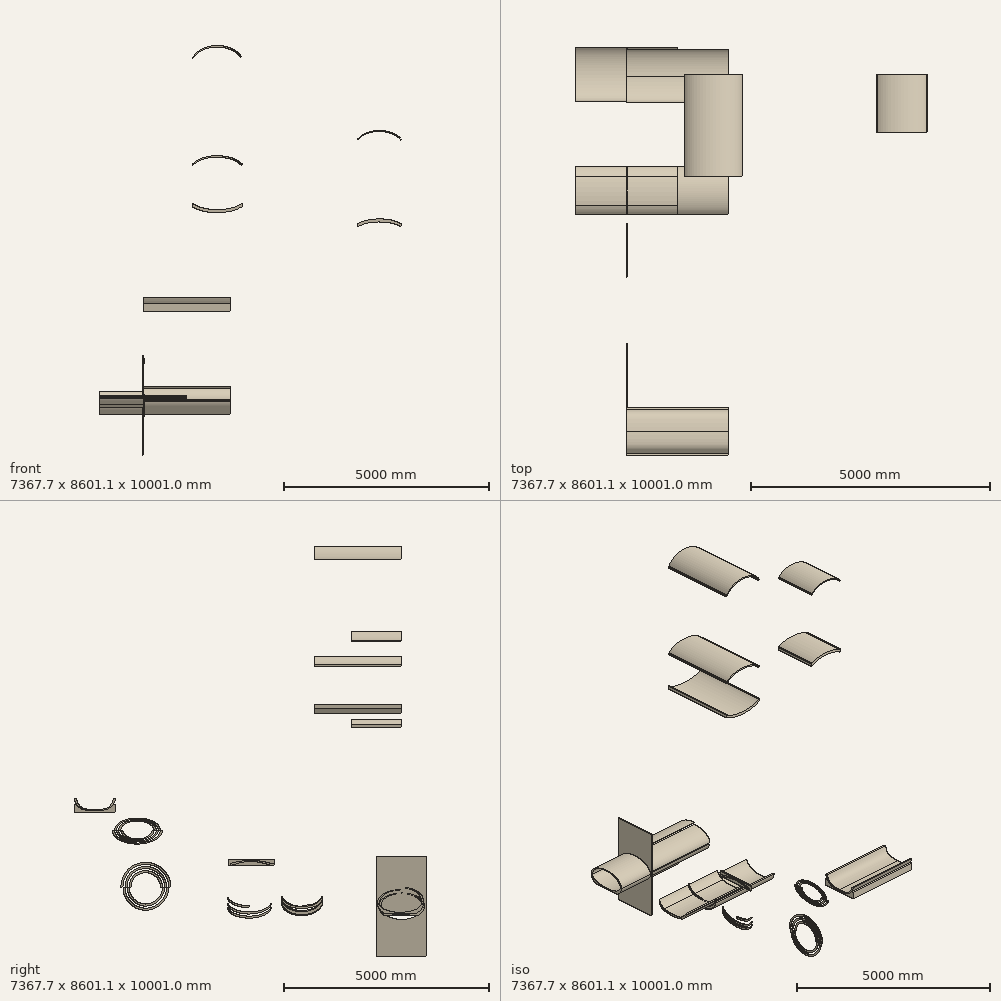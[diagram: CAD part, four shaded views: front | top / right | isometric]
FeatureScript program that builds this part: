
annotation { "Feature Type Name" : "Feature", "Feature Type Description" : "" }
export const myFeature = defineFeature(function(context is Context, id is Id, definition is map)
    precondition{}
    {
        {
            var Q0;
            Q0=qCreatedBy(makeId("Right.planeOp"),FACE);
            var sketch = newSketch(context, id + "F0", { "sketchPlane" : qUnion([Q0])});
            skLineSegment(sketch, "E0.bottom", {"start": v(-609.6, 1219.2) * mm, "end": v(609.6, 1219.2) * mm});
            skLineSegment(sketch, "E0.top", {"start": v(-609.6, -1219.2) * mm, "end": v(609.6, -1219.2) * mm});
            skLineSegment(sketch, "E0.left", {"start": v(-609.6, 1219.2) * mm, "end": v(-609.6, -1219.2) * mm});
            skLineSegment(sketch, "E0.right", {"start": v(609.6, 1219.2) * mm, "end": v(609.6, -1219.2) * mm});
            skPoint(sketch, "E0.middle", {"position": v(0, 0) * mm});
            skEllipse(sketch, "E1", {"center": v(0, 0) * mm, "majorRadius": 558.8 * mm, "minorRadius": 330.2 * mm, "majorAxis": v(1, 0)});
            skEllipse(sketch, "E2", {"center": v(0, 0) * mm, "majorRadius": 508 * mm, "minorRadius": 203.2 * mm, "majorAxis": v(1, 0)});
            skEllipse(sketch, "E3", {"center": v(0, 0) * mm, "majorRadius": 508 * mm, "minorRadius": 317.5 * mm, "majorAxis": v(1, 0)});
            skLineSegment(sketch, "E4", {"start": v(-558.8, 0) * mm, "end": v(558.8, 0) * mm, "construction": true});
            skLineSegment(sketch, "E5.bottom", {"start": v(571.5, -329.86) * mm, "end": v(-571.5, -329.86) * mm});
            skLineSegment(sketch, "E5.top", {"start": v(571.5, -228.26) * mm, "end": v(-571.5, -228.26) * mm});
            skLineSegment(sketch, "E5.left", {"start": v(571.5, -329.86) * mm, "end": v(571.5, -228.26) * mm});
            skLineSegment(sketch, "E5.right", {"start": v(-571.5, -329.86) * mm, "end": v(-571.5, -228.26) * mm});
            skPoint(sketch, "E5.middle", {"position": v(0, -279.06) * mm});
            skLineSegment(sketch, "E6", {"start": v(508, 0) * mm, "end": v(558.8, 0) * mm});
            skCircle(sketch, "E7", {"center": v(533.4, 0) * mm, "radius": 25.4 * mm});
            skLineSegment(sketch, "E8", {"start": v(-508, 0) * mm, "end": v(-558.8, 0) * mm});
            skSolve(sketch);
        }
        {
            var Q0;
            {var subQ0=sQuery(id+"F0.wireOp",EDGE,"E3");var subQ1=sQuery(id+"F0.wireOp",EDGE,"E2");var subQ2=makeQuery(id+"F0.imprint","INTERSECT",VERTEX,{"disambiguationData":[OD(0.0)],"derivedFrom":[subQ1,subQ0]});Q0=makeQuery(id+"F0.imprint","IMPRINT",FACE,{"disambiguationData":[TD([[makeQuery(id+"F0.imprint","IMPRINT",EDGE,{"disambiguationData":[TD([[subQ2,-1.0]])],"derivedFrom":subQ1}),-1.0]])]});}
            var Q1;
            {var subQ2=sQuery(id+"F0.wireOp",EDGE,"E1");var subQ4=sQuery(id+"F0.wireOp",EDGE,"E5.top");var subQ5=makeQuery(id+"F0.imprint","INTERSECT",VERTEX,{"disambiguationData":[OD(1.0)],"derivedFrom":[subQ2,subQ4]});Q1=makeQuery(id+"F0.imprint","IMPRINT",FACE,{"disambiguationData":[TD([[makeQuery(id+"F0.imprint","IMPRINT",EDGE,{"disambiguationData":[TD([[subQ5,-1.0]])],"derivedFrom":subQ4}),-1.0]])]});}
            var Q2;
            {var subQ0=sQuery(id+"F0.wireOp",EDGE,"E8");Q2=makeQuery(id+"F0.imprint","IMPRINT",FACE,{"disambiguationData":[TD([[makeQuery(id+"F0.imprint","IMPRINT",EDGE,{"derivedFrom":subQ0}),1.0]])]});}
            extrude(context, id + "F1", {"entities" : qUnion([Q0, Q1, Q2]), "endBound" : BoundingType.SYMMETRIC, "depth" : 2133.6 * mm});
        }
        {
            var Q0;
            {var subQ4=sQuery(id+"F0.wireOp",EDGE,"E8");Q0=makeQuery(id+"F0.imprint","IMPRINT",FACE,{"disambiguationData":[TD([[makeQuery(id+"F0.imprint","IMPRINT",EDGE,{"derivedFrom":subQ4}),-1.0]])]});}
            var Q1;
            {var subQ0=sQuery(id+"F0.wireOp",EDGE,"E6");Q1=makeQuery(id+"F0.imprint","IMPRINT",FACE,{"disambiguationData":[TD([[makeQuery(id+"F0.imprint","IMPRINT",EDGE,{"derivedFrom":subQ0}),1.0]])]});}
            var Q2;
            {var subQ0=sQuery(id+"F0.wireOp",EDGE,"E6");Q2=makeQuery(id+"F0.imprint","IMPRINT",FACE,{"disambiguationData":[TD([[makeQuery(id+"F0.imprint","IMPRINT",EDGE,{"derivedFrom":subQ0}),-1.0]])]});}
            extrude(context, id + "F2", {"entities" : qUnion([Q0, Q1, Q2]), "endBound" : BoundingType.SYMMETRIC, "depth" : 2133.6 * mm});
        }
        {
            var Q0;
            {var subQ5=sQuery(id+"F0.wireOp",EDGE,"E5.left");Q0=makeQuery(id+"F0.imprint","IMPRINT",FACE,{"disambiguationData":[TD([[makeQuery(id+"F0.imprint","IMPRINT",EDGE,{"derivedFrom":subQ5}),1.0]])]});}
            var Q1;
            {var subQ0=sQuery(id+"F0.wireOp",EDGE,"E3");var subQ1=sQuery(id+"F0.wireOp",EDGE,"E2");var subQ3=makeQuery(id+"F0.imprint","INTERSECT",VERTEX,{"derivedFrom":[subQ1,subQ0,sQuery(id+"F0.wireOp",EDGE,"E8")]});Q1=makeQuery(id+"F0.imprint","IMPRINT",FACE,{"disambiguationData":[TD([[makeQuery(id+"F0.imprint","IMPRINT",EDGE,{"disambiguationData":[TD([[subQ3,1.0]])],"derivedFrom":subQ1}),-1.0]])]});}
            var Q2;
            {var subQ0=sQuery(id+"F0.wireOp",EDGE,"E3");var subQ1=sQuery(id+"F0.wireOp",EDGE,"E2");var subQ3=makeQuery(id+"F0.imprint","INTERSECT",VERTEX,{"derivedFrom":[subQ1,subQ0,sQuery(id+"F0.wireOp",EDGE,"E8")]});Q2=makeQuery(id+"F0.imprint","IMPRINT",FACE,{"disambiguationData":[TD([[makeQuery(id+"F0.imprint","IMPRINT",EDGE,{"disambiguationData":[TD([[subQ3,1.0]])],"derivedFrom":subQ1}),1.0]])]});}
            var Q3;
            {var subQ0=sQuery(id+"F0.wireOp",EDGE,"E5.top");var subQ1=sQuery(id+"F0.wireOp",EDGE,"E3");var subQ2=makeQuery(id+"F0.imprint","INTERSECT",VERTEX,{"disambiguationData":[OD(0.0)],"derivedFrom":[subQ1,subQ0]});Q3=makeQuery(id+"F0.imprint","IMPRINT",FACE,{"disambiguationData":[TD([[makeQuery(id+"F0.imprint","IMPRINT",EDGE,{"disambiguationData":[TD([[subQ2,-1.0]])],"derivedFrom":subQ1}),1.0]])]});}
            var Q4;
            {var subQ5=sQuery(id+"F0.wireOp",EDGE,"E5.right");Q4=makeQuery(id+"F0.imprint","IMPRINT",FACE,{"disambiguationData":[TD([[makeQuery(id+"F0.imprint","IMPRINT",EDGE,{"derivedFrom":subQ5}),-1.0]])]});}
            var Q5;
            {var subQ1=sQuery(id+"F0.wireOp",EDGE,"E1");var subQ4=sQuery(id+"F0.wireOp",EDGE,"E5.top");var subQ5=makeQuery(id+"F0.imprint","INTERSECT",VERTEX,{"disambiguationData":[OD(0.0)],"derivedFrom":[subQ1,subQ4]});Q5=makeQuery(id+"F0.imprint","IMPRINT",FACE,{"disambiguationData":[TD([[makeQuery(id+"F0.imprint","IMPRINT",EDGE,{"disambiguationData":[TD([[subQ5,-1.0]])],"derivedFrom":subQ1}),1.0]])]});}
            var Q6;
            {var subQ4=sQuery(id+"F0.wireOp",EDGE,"E8");Q6=makeQuery(id+"F0.imprint","IMPRINT",FACE,{"disambiguationData":[TD([[makeQuery(id+"F0.imprint","IMPRINT",EDGE,{"derivedFrom":subQ4}),-1.0]])]});}
            var Q7;
            {var subQ0=sQuery(id+"F0.wireOp",EDGE,"E8");Q7=makeQuery(id+"F0.imprint","IMPRINT",FACE,{"disambiguationData":[TD([[makeQuery(id+"F0.imprint","IMPRINT",EDGE,{"derivedFrom":subQ0}),1.0]])]});}
            var Q8;
            {var subQ2=sQuery(id+"F0.wireOp",EDGE,"E1");var subQ4=sQuery(id+"F0.wireOp",EDGE,"E5.top");var subQ5=makeQuery(id+"F0.imprint","INTERSECT",VERTEX,{"disambiguationData":[OD(1.0)],"derivedFrom":[subQ2,subQ4]});Q8=makeQuery(id+"F0.imprint","IMPRINT",FACE,{"disambiguationData":[TD([[makeQuery(id+"F0.imprint","IMPRINT",EDGE,{"disambiguationData":[TD([[subQ5,-1.0]])],"derivedFrom":subQ4}),-1.0]])]});}
            var Q9;
            {var subQ0=sQuery(id+"F0.wireOp",EDGE,"E3");var subQ4=sQuery(id+"F0.wireOp",EDGE,"E5.top");var subQ5=makeQuery(id+"F0.imprint","INTERSECT",VERTEX,{"disambiguationData":[OD(0.0)],"derivedFrom":[subQ0,subQ4]});Q9=makeQuery(id+"F0.imprint","IMPRINT",FACE,{"disambiguationData":[TD([[makeQuery(id+"F0.imprint","IMPRINT",EDGE,{"disambiguationData":[TD([[subQ5,1.0]])],"derivedFrom":subQ4}),-1.0]])]});}
            var Q10;
            Q10=makeQuery(id+"F0.imprint","IMPRINT",FACE,{"disambiguationData":[TD([[makeQuery(id+"F0.imprint","IMPRINT",EDGE,{"derivedFrom":sQuery(id+"F0.wireOp",EDGE,"E0.bottom")}),-1.0]])]});
            var Q11;
            {var subQ0=sQuery(id+"F0.wireOp",EDGE,"E5.bottom");var subQ1=sQuery(id+"F0.wireOp",EDGE,"E1");var subQ2=makeQuery(id+"F0.imprint","INTERSECT",VERTEX,{"disambiguationData":[OD(0.0)],"derivedFrom":[subQ1,subQ0]});Q11=makeQuery(id+"F0.imprint","IMPRINT",FACE,{"disambiguationData":[TD([[makeQuery(id+"F0.imprint","IMPRINT",EDGE,{"disambiguationData":[TD([[subQ2,-1.0]])],"derivedFrom":subQ1}),1.0]])]});}
            var Q12;
            {var subQ0=sQuery(id+"F0.wireOp",EDGE,"E6");Q12=makeQuery(id+"F0.imprint","IMPRINT",FACE,{"disambiguationData":[TD([[makeQuery(id+"F0.imprint","IMPRINT",EDGE,{"derivedFrom":subQ0}),1.0]])]});}
            var Q13;
            {var subQ0=sQuery(id+"F0.wireOp",EDGE,"E6");Q13=makeQuery(id+"F0.imprint","IMPRINT",FACE,{"disambiguationData":[TD([[makeQuery(id+"F0.imprint","IMPRINT",EDGE,{"derivedFrom":subQ0}),-1.0]])]});}
            extrude(context, id + "F3", {"entities" : qUnion([Q0, Q1, Q2, Q3, Q4, Q5, Q6, Q7, Q8, Q9, Q10, Q11, Q12, Q13]), "oppositeDirection" : true, "depth" : 11.9 * mm});
        }
        {
            var Q0;
            {var subQ0=sQuery(id+"F0.wireOp",EDGE,"E8");Q0=makeQuery(id+"F0.imprint","IMPRINT",FACE,{"disambiguationData":[TD([[makeQuery(id+"F0.imprint","IMPRINT",EDGE,{"derivedFrom":subQ0}),1.0]])]});}
            var Q1;
            {var subQ0=sQuery(id+"F0.wireOp",EDGE,"E3");var subQ4=sQuery(id+"F0.wireOp",EDGE,"E5.top");var subQ5=makeQuery(id+"F0.imprint","INTERSECT",VERTEX,{"disambiguationData":[OD(0.0)],"derivedFrom":[subQ0,subQ4]});Q1=makeQuery(id+"F0.imprint","IMPRINT",FACE,{"disambiguationData":[TD([[makeQuery(id+"F0.imprint","IMPRINT",EDGE,{"disambiguationData":[TD([[subQ5,1.0]])],"derivedFrom":subQ4}),-1.0]])]});}
            var Q2;
            {var subQ2=sQuery(id+"F0.wireOp",EDGE,"E1");var subQ4=sQuery(id+"F0.wireOp",EDGE,"E5.top");var subQ5=makeQuery(id+"F0.imprint","INTERSECT",VERTEX,{"disambiguationData":[OD(1.0)],"derivedFrom":[subQ2,subQ4]});Q2=makeQuery(id+"F0.imprint","IMPRINT",FACE,{"disambiguationData":[TD([[makeQuery(id+"F0.imprint","IMPRINT",EDGE,{"disambiguationData":[TD([[subQ5,-1.0]])],"derivedFrom":subQ4}),-1.0]])]});}
            extrude(context, id + "F4", {"entities" : qUnion([Q0, Q1, Q2]), "depth" : 11.9 * mm});
        }
        {
            var Q0;
            {var subQ4=sQuery(id+"F0.wireOp",EDGE,"E8");Q0=makeQuery(id+"F0.imprint","IMPRINT",FACE,{"disambiguationData":[TD([[makeQuery(id+"F0.imprint","IMPRINT",EDGE,{"derivedFrom":subQ4}),-1.0]])]});}
            var Q1;
            {var subQ0=sQuery(id+"F0.wireOp",EDGE,"E6");Q1=makeQuery(id+"F0.imprint","IMPRINT",FACE,{"disambiguationData":[TD([[makeQuery(id+"F0.imprint","IMPRINT",EDGE,{"derivedFrom":subQ0}),1.0]])]});}
            var Q2;
            {var subQ0=sQuery(id+"F0.wireOp",EDGE,"E6");Q2=makeQuery(id+"F0.imprint","IMPRINT",FACE,{"disambiguationData":[TD([[makeQuery(id+"F0.imprint","IMPRINT",EDGE,{"derivedFrom":subQ0}),-1.0]])]});}
            extrude(context, id + "F5", {"entities" : qUnion([Q0, Q1, Q2]), "depth" : 11.9 * mm});
        }
        {
            var Q0;
            Q0=qCreatedBy(makeId("Right.planeOp"),FACE);
            var sketch = newSketch(context, id + "F6", { "sketchPlane" : qUnion([Q0])});
            skEllipse(sketch, "E9", {"center": v(-3717.75, -31.09) * mm, "majorRadius": 533.4 * mm, "minorRadius": 254 * mm, "majorAxis": v(1, 0)});
            skLineSegment(sketch, "E10", {"start": v(-3717.75, -31.09) * mm, "end": v(-3717.75, 922.12) * mm});
            skEllipse(sketch, "E11.0.1.0", {"center": v(-3717.75, 19.71) * mm, "majorRadius": 533.4 * mm, "minorRadius": 254 * mm, "majorAxis": v(1, 0)});
            skEllipse(sketch, "E11.0.2.0", {"center": v(-3717.75, 70.51) * mm, "majorRadius": 533.4 * mm, "minorRadius": 254 * mm, "majorAxis": v(1, 0)});
            skEllipse(sketch, "E11.0.3.0", {"center": v(-3717.75, 121.31) * mm, "majorRadius": 533.4 * mm, "minorRadius": 254 * mm, "majorAxis": v(1, 0)});
            skEllipse(sketch, "E11.0.4.0", {"center": v(-3717.75, 172.11) * mm, "majorRadius": 533.4 * mm, "minorRadius": 254 * mm, "majorAxis": v(1, 0)});
            skEllipse(sketch, "E11.0.5.0", {"center": v(-3717.75, 222.91) * mm, "majorRadius": 533.4 * mm, "minorRadius": 254 * mm, "majorAxis": v(1, 0)});
            skEllipse(sketch, "E11.0.6.0", {"center": v(-3717.75, 273.71) * mm, "majorRadius": 533.4 * mm, "minorRadius": 254 * mm, "majorAxis": v(1, 0)});
            skEllipse(sketch, "E11.0.7.0", {"center": v(-3717.75, 324.51) * mm, "majorRadius": 533.4 * mm, "minorRadius": 254 * mm, "majorAxis": v(1, 0)});
            skEllipse(sketch, "E11.0.8.0", {"center": v(-3717.75, 375.31) * mm, "majorRadius": 533.4 * mm, "minorRadius": 254 * mm, "majorAxis": v(1, 0)});
            skEllipse(sketch, "E11.0.9.0", {"center": v(-3717.75, 426.11) * mm, "majorRadius": 533.4 * mm, "minorRadius": 254 * mm, "majorAxis": v(1, 0)});
            skLineSegment(sketch, "E11.direction1", {"start": v(-3717.75, -31.09) * mm, "end": v(-3743.15, -31.09) * mm, "construction": true});
            skLineSegment(sketch, "E11.direction2", {"start": v(-3717.75, -31.09) * mm, "end": v(-3717.75, 19.71) * mm, "construction": true});
            skSolve(sketch);
        }
        {
            var Q0;
            {var subQ0=sQuery(id+"F6.wireOp",EDGE,"E11.0.1.0");var subQ1=sQuery(id+"F6.wireOp",EDGE,"E9");var subQ2=makeQuery(id+"F6.imprint","INTERSECT",VERTEX,{"disambiguationData":[OD(0.0)],"derivedFrom":[subQ1,subQ0]});Q0=makeQuery(id+"F6.imprint","IMPRINT",FACE,{"disambiguationData":[TD([[makeQuery(id+"F6.imprint","IMPRINT",EDGE,{"disambiguationData":[TD([[subQ2,1.0]])],"derivedFrom":subQ1}),1.0]])]});}
            extrude(context, id + "F7", {"entities" : qUnion([Q0]), "depth" : 25.4 * mm});
        }
        {
            var Q0;
            {var subQ0=sQuery(id+"F6.wireOp",EDGE,"E11.0.2.0");var subQ1=sQuery(id+"F6.wireOp",EDGE,"E9");var subQ2=makeQuery(id+"F6.imprint","INTERSECT",VERTEX,{"disambiguationData":[OD(0.0)],"derivedFrom":[subQ1,subQ0]});Q0=makeQuery(id+"F6.imprint","IMPRINT",FACE,{"disambiguationData":[TD([[makeQuery(id+"F6.imprint","IMPRINT",EDGE,{"disambiguationData":[TD([[subQ2,-1.0]])],"derivedFrom":subQ1}),1.0]])]});}
            var Q1;
            {var subQ0=sQuery(id+"F6.wireOp",EDGE,"E11.0.3.0");var subQ1=sQuery(id+"F6.wireOp",EDGE,"E9");var subQ2=makeQuery(id+"F6.imprint","INTERSECT",VERTEX,{"disambiguationData":[OD(1.0)],"derivedFrom":[subQ1,subQ0]});Q1=makeQuery(id+"F6.imprint","IMPRINT",FACE,{"disambiguationData":[TD([[makeQuery(id+"F6.imprint","IMPRINT",EDGE,{"disambiguationData":[TD([[subQ2,-1.0]])],"derivedFrom":subQ1}),-1.0]])]});}
            var Q2;
            {var subQ0=sQuery(id+"F6.wireOp",EDGE,"E11.0.2.0");var subQ1=sQuery(id+"F6.wireOp",EDGE,"E11.0.1.0");var subQ2=makeQuery(id+"F6.imprint","INTERSECT",VERTEX,{"disambiguationData":[OD(1.0)],"derivedFrom":[subQ1,subQ0]});Q2=makeQuery(id+"F6.imprint","IMPRINT",FACE,{"disambiguationData":[TD([[makeQuery(id+"F6.imprint","IMPRINT",EDGE,{"disambiguationData":[TD([[subQ2,1.0]])],"derivedFrom":subQ1}),-1.0]])]});}
            var Q3;
            {var subQ0=sQuery(id+"F6.wireOp",EDGE,"E11.0.2.0");var subQ1=sQuery(id+"F6.wireOp",EDGE,"E9");var subQ2=makeQuery(id+"F6.imprint","INTERSECT",VERTEX,{"disambiguationData":[OD(0.0)],"derivedFrom":[subQ1,subQ0]});Q3=makeQuery(id+"F6.imprint","IMPRINT",FACE,{"disambiguationData":[TD([[makeQuery(id+"F6.imprint","IMPRINT",EDGE,{"disambiguationData":[TD([[subQ2,-1.0]])],"derivedFrom":subQ1}),-1.0]])]});}
            var Q4;
            {var subQ0=sQuery(id+"F6.wireOp",EDGE,"E11.0.2.0");var subQ1=sQuery(id+"F6.wireOp",EDGE,"E11.0.1.0");var subQ2=makeQuery(id+"F6.imprint","INTERSECT",VERTEX,{"disambiguationData":[OD(0.0)],"derivedFrom":[subQ1,subQ0]});Q4=makeQuery(id+"F6.imprint","IMPRINT",FACE,{"disambiguationData":[TD([[makeQuery(id+"F6.imprint","IMPRINT",EDGE,{"disambiguationData":[TD([[subQ2,-1.0]])],"derivedFrom":subQ1}),-1.0]])]});}
            extrude(context, id + "F8", {"entities" : qUnion([Q0, Q1, Q2, Q3, Q4]), "depth" : 25.4 * mm});
        }
        {
            var Q0;
            Q0=qCreatedBy(makeId("Right.planeOp"),FACE);
            var sketch = newSketch(context, id + "F9", { "sketchPlane" : qUnion([Q0])});
            skLineSegment(sketch, "E12", {"start": v(-2434.14, 662.12) * mm, "end": v(-2434.14, -346.82) * mm, "construction": true});
            skEllipse(sketch, "E13", {"center": v(-2434.14, 104.15) * mm, "majorRadius": 508 * mm, "minorRadius": 203.2 * mm, "majorAxis": v(1, 0)});
            skEllipse(sketch, "E14.0.1.0", {"center": v(-2434.14, 129.55) * mm, "majorRadius": 508 * mm, "minorRadius": 203.2 * mm, "majorAxis": v(1, 0)});
            skEllipse(sketch, "E14.0.2.0", {"center": v(-2434.14, 154.95) * mm, "majorRadius": 508 * mm, "minorRadius": 203.2 * mm, "majorAxis": v(1, 0)});
            skEllipse(sketch, "E14.0.3.0", {"center": v(-2434.14, 180.35) * mm, "majorRadius": 508 * mm, "minorRadius": 203.2 * mm, "majorAxis": v(1, 0)});
            skLineSegment(sketch, "E14.direction1", {"start": v(-2434.14, 104.15) * mm, "end": v(-2434.14, 104.15) * mm});
            skLineSegment(sketch, "E14.direction2", {"start": v(-2434.14, 104.15) * mm, "end": v(-2434.14, 129.55) * mm, "construction": true});
            skEllipse(sketch, "E15", {"center": v(-2434.14, 104.15) * mm, "majorRadius": 508 * mm, "minorRadius": 330.2 * mm, "majorAxis": v(1, 0)});
            skEllipse(sketch, "E16.0.1.0", {"center": v(-2434.14, 129.55) * mm, "majorRadius": 508 * mm, "minorRadius": 330.2 * mm, "majorAxis": v(1, 0)});
            skEllipse(sketch, "E16.0.2.0", {"center": v(-2434.14, 154.95) * mm, "majorRadius": 508 * mm, "minorRadius": 330.2 * mm, "majorAxis": v(1, 0)});
            skEllipse(sketch, "E16.0.3.0", {"center": v(-2434.14, 180.35) * mm, "majorRadius": 508 * mm, "minorRadius": 330.2 * mm, "majorAxis": v(1, 0)});
            skEllipse(sketch, "E17.0.0.4", {"center": v(-2434.14, 205.75) * mm, "majorRadius": 508 * mm, "minorRadius": 330.2 * mm, "majorAxis": v(1, 0)});
            skEllipse(sketch, "E17.0.0.5", {"center": v(-2434.14, 231.15) * mm, "majorRadius": 508 * mm, "minorRadius": 330.2 * mm, "majorAxis": v(1, 0)});
            skEllipse(sketch, "E17.0.0.6", {"center": v(-2434.14, 256.55) * mm, "majorRadius": 508 * mm, "minorRadius": 330.2 * mm, "majorAxis": v(1, 0)});
            skEllipse(sketch, "E17.0.0.7", {"center": v(-2434.14, 281.95) * mm, "majorRadius": 508 * mm, "minorRadius": 330.2 * mm, "majorAxis": v(1, 0)});
            skEllipse(sketch, "E17.0.0.8", {"center": v(-2434.14, 307.35) * mm, "majorRadius": 508 * mm, "minorRadius": 330.2 * mm, "majorAxis": v(1, 0)});
            skEllipse(sketch, "E17.0.0.9", {"center": v(-2434.14, 332.75) * mm, "majorRadius": 508 * mm, "minorRadius": 330.2 * mm, "majorAxis": v(1, 0)});
            skEllipse(sketch, "E18.0.0.4", {"center": v(-2434.14, 205.75) * mm, "majorRadius": 508 * mm, "minorRadius": 203.2 * mm, "majorAxis": v(1, 0)});
            skEllipse(sketch, "E18.0.0.5", {"center": v(-2434.14, 231.15) * mm, "majorRadius": 508 * mm, "minorRadius": 203.2 * mm, "majorAxis": v(1, 0)});
            skEllipse(sketch, "E18.0.0.6", {"center": v(-2434.14, 256.55) * mm, "majorRadius": 508 * mm, "minorRadius": 203.2 * mm, "majorAxis": v(1, 0)});
            skEllipse(sketch, "E18.0.0.7", {"center": v(-2434.14, 281.95) * mm, "majorRadius": 508 * mm, "minorRadius": 203.2 * mm, "majorAxis": v(1, 0)});
            skEllipse(sketch, "E18.0.0.8", {"center": v(-2434.14, 307.35) * mm, "majorRadius": 508 * mm, "minorRadius": 203.2 * mm, "majorAxis": v(1, 0)});
            skEllipse(sketch, "E18.0.0.9", {"center": v(-2434.14, 332.75) * mm, "majorRadius": 508 * mm, "minorRadius": 203.2 * mm, "majorAxis": v(1, 0)});
            skLineSegment(sketch, "E19", {"start": v(-2434.14, 27.95) * mm, "end": v(-2434.14, 2.55) * mm});
            skSolve(sketch);
        }
        {
            var Q0;
            {var subQ0=sQuery(id+"F9.wireOp",EDGE,"E15");var subQ1=sQuery(id+"F9.wireOp",EDGE,"E13");var subQ2=makeQuery(id+"F9.imprint","INTERSECT",VERTEX,{"disambiguationData":[OD(1.0)],"derivedFrom":[subQ1,subQ0]});Q0=makeQuery(id+"F9.imprint","IMPRINT",FACE,{"disambiguationData":[TD([[makeQuery(id+"F9.imprint","IMPRINT",EDGE,{"disambiguationData":[TD([[subQ2,-1.0]])],"derivedFrom":subQ1}),-1.0]])]});}
            var Q1;
            {var subQ0=sQuery(id+"F9.wireOp",EDGE,"E13");var subQ1=makeQuery(id+"F9.imprint","INTERSECT",VERTEX,{"disambiguationData":[OD(0.0)],"derivedFrom":[subQ0,sQuery(id+"F9.wireOp",EDGE,"E15")]});Q1=makeQuery(id+"F9.imprint","IMPRINT",FACE,{"disambiguationData":[TD([[makeQuery(id+"F9.imprint","IMPRINT",EDGE,{"disambiguationData":[TD([[subQ1,-1.0]])],"derivedFrom":subQ0}),1.0]])]});}
            var Q2;
            {var subQ0=sQuery(id+"F9.wireOp",EDGE,"E13");var subQ1=makeQuery(id+"F9.imprint","INTERSECT",VERTEX,{"disambiguationData":[OD(1.0)],"derivedFrom":[subQ0,sQuery(id+"F9.wireOp",EDGE,"E15")]});Q2=makeQuery(id+"F9.imprint","IMPRINT",FACE,{"disambiguationData":[TD([[makeQuery(id+"F9.imprint","IMPRINT",EDGE,{"disambiguationData":[TD([[subQ1,1.0]])],"derivedFrom":subQ0}),1.0]])]});}
            extrude(context, id + "F10", {"entities" : qUnion([Q0, Q1, Q2]), "depth" : 2133.6 * mm});
        }
        {
            var Q0;
            {var subQ0=sQuery(id+"F9.wireOp",EDGE,"E16.0.1.0");var subQ1=sQuery(id+"F9.wireOp",EDGE,"E13");var subQ2=makeQuery(id+"F9.imprint","INTERSECT",VERTEX,{"disambiguationData":[OD(0.0)],"derivedFrom":[subQ1,subQ0]});Q0=makeQuery(id+"F9.imprint","IMPRINT",FACE,{"disambiguationData":[TD([[makeQuery(id+"F9.imprint","IMPRINT",EDGE,{"disambiguationData":[TD([[subQ2,-1.0]])],"derivedFrom":subQ1}),1.0]])]});}
            var Q1;
            {var subQ0=sQuery(id+"F9.wireOp",EDGE,"E16.0.3.0");var subQ1=sQuery(id+"F9.wireOp",EDGE,"E13");var subQ2=makeQuery(id+"F9.imprint","INTERSECT",VERTEX,{"disambiguationData":[OD(3.0)],"derivedFrom":[subQ1,subQ0]});Q1=makeQuery(id+"F9.imprint","IMPRINT",FACE,{"disambiguationData":[TD([[makeQuery(id+"F9.imprint","IMPRINT",EDGE,{"disambiguationData":[TD([[subQ2,-1.0]])],"derivedFrom":subQ1}),1.0]])]});}
            var Q2;
            {var subQ0=sQuery(id+"F9.wireOp",EDGE,"E16.0.1.0");var subQ1=sQuery(id+"F9.wireOp",EDGE,"E13");var subQ2=makeQuery(id+"F9.imprint","INTERSECT",VERTEX,{"disambiguationData":[OD(2.0)],"derivedFrom":[subQ1,subQ0]});Q2=makeQuery(id+"F9.imprint","IMPRINT",FACE,{"disambiguationData":[TD([[makeQuery(id+"F9.imprint","IMPRINT",EDGE,{"disambiguationData":[TD([[subQ2,-1.0]])],"derivedFrom":subQ1}),-1.0]])]});}
            var Q3;
            {var subQ0=sQuery(id+"F9.wireOp",EDGE,"E16.0.2.0");var subQ1=sQuery(id+"F9.wireOp",EDGE,"E13");var subQ2=makeQuery(id+"F9.imprint","INTERSECT",VERTEX,{"disambiguationData":[OD(2.0)],"derivedFrom":[subQ1,subQ0]});Q3=makeQuery(id+"F9.imprint","IMPRINT",FACE,{"disambiguationData":[TD([[makeQuery(id+"F9.imprint","IMPRINT",EDGE,{"disambiguationData":[TD([[subQ2,-1.0]])],"derivedFrom":subQ1}),-1.0]])]});}
            var Q4;
            {var subQ0=sQuery(id+"F9.wireOp",EDGE,"E16.0.2.0");var subQ1=sQuery(id+"F9.wireOp",EDGE,"E13");var subQ2=makeQuery(id+"F9.imprint","INTERSECT",VERTEX,{"disambiguationData":[OD(2.0)],"derivedFrom":[subQ1,subQ0]});Q4=makeQuery(id+"F9.imprint","IMPRINT",FACE,{"disambiguationData":[TD([[makeQuery(id+"F9.imprint","IMPRINT",EDGE,{"disambiguationData":[TD([[subQ2,-1.0]])],"derivedFrom":subQ1}),1.0]])]});}
            var Q5;
            {var subQ1=sQuery(id+"F9.wireOp",EDGE,"E13");var subQ6=sQuery(id+"F9.wireOp",EDGE,"E14.0.1.0");var subQ7=makeQuery(id+"F9.imprint","INTERSECT",VERTEX,{"disambiguationData":[OD(1.0)],"derivedFrom":[subQ1,subQ6]});Q5=makeQuery(id+"F9.imprint","IMPRINT",FACE,{"disambiguationData":[TD([[makeQuery(id+"F9.imprint","IMPRINT",EDGE,{"disambiguationData":[TD([[subQ7,-1.0]])],"derivedFrom":subQ1}),1.0]])]});}
            var Q6;
            {var subQ0=sQuery(id+"F9.wireOp",EDGE,"E16.0.2.0");var subQ1=sQuery(id+"F9.wireOp",EDGE,"E13");var subQ2=makeQuery(id+"F9.imprint","INTERSECT",VERTEX,{"disambiguationData":[OD(0.0)],"derivedFrom":[subQ1,subQ0]});Q6=makeQuery(id+"F9.imprint","IMPRINT",FACE,{"disambiguationData":[TD([[makeQuery(id+"F9.imprint","IMPRINT",EDGE,{"disambiguationData":[TD([[subQ2,-1.0]])],"derivedFrom":subQ1}),1.0]])]});}
            var Q7;
            {var subQ0=sQuery(id+"F9.wireOp",EDGE,"E14.0.1.0");var subQ1=sQuery(id+"F9.wireOp",EDGE,"E13");var subQ2=makeQuery(id+"F9.imprint","INTERSECT",VERTEX,{"disambiguationData":[OD(0.0)],"derivedFrom":[subQ1,subQ0]});Q7=makeQuery(id+"F9.imprint","IMPRINT",FACE,{"disambiguationData":[TD([[makeQuery(id+"F9.imprint","IMPRINT",EDGE,{"disambiguationData":[TD([[subQ2,-1.0]])],"derivedFrom":subQ1}),1.0]])]});}
            var Q8;
            {var subQ0=sQuery(id+"F9.wireOp",EDGE,"E14.0.2.0");var subQ1=sQuery(id+"F9.wireOp",EDGE,"E13");var subQ2=makeQuery(id+"F9.imprint","INTERSECT",VERTEX,{"disambiguationData":[OD(0.0)],"derivedFrom":[subQ1,subQ0]});Q8=makeQuery(id+"F9.imprint","IMPRINT",FACE,{"disambiguationData":[TD([[makeQuery(id+"F9.imprint","IMPRINT",EDGE,{"disambiguationData":[TD([[subQ2,-1.0]])],"derivedFrom":subQ1}),1.0]])]});}
            var Q9;
            {var subQ5=sQuery(id+"F9.wireOp",EDGE,"E13");var subQ7=sQuery(id+"F9.wireOp",EDGE,"E14.0.2.0");var subQ8=makeQuery(id+"F9.imprint","INTERSECT",VERTEX,{"disambiguationData":[OD(1.0)],"derivedFrom":[subQ5,subQ7]});Q9=makeQuery(id+"F9.imprint","IMPRINT",FACE,{"disambiguationData":[TD([[makeQuery(id+"F9.imprint","IMPRINT",EDGE,{"disambiguationData":[TD([[subQ8,-1.0]])],"derivedFrom":subQ5}),1.0]])]});}
            var Q10;
            {var subQ0=sQuery(id+"F9.wireOp",EDGE,"E16.0.2.0");var subQ1=sQuery(id+"F9.wireOp",EDGE,"E13");var subQ2=makeQuery(id+"F9.imprint","INTERSECT",VERTEX,{"disambiguationData":[OD(1.0)],"derivedFrom":[subQ1,subQ0]});Q10=makeQuery(id+"F9.imprint","IMPRINT",FACE,{"disambiguationData":[TD([[makeQuery(id+"F9.imprint","IMPRINT",EDGE,{"disambiguationData":[TD([[subQ2,-1.0]])],"derivedFrom":subQ1}),1.0]])]});}
            var Q11;
            {var subQ0=sQuery(id+"F9.wireOp",EDGE,"E16.0.3.0");var subQ1=sQuery(id+"F9.wireOp",EDGE,"E13");var subQ2=makeQuery(id+"F9.imprint","INTERSECT",VERTEX,{"disambiguationData":[OD(2.0)],"derivedFrom":[subQ1,subQ0]});Q11=makeQuery(id+"F9.imprint","IMPRINT",FACE,{"disambiguationData":[TD([[makeQuery(id+"F9.imprint","IMPRINT",EDGE,{"disambiguationData":[TD([[subQ2,-1.0]])],"derivedFrom":subQ1}),-1.0]])]});}
            var Q12;
            {var subQ0=sQuery(id+"F9.wireOp",EDGE,"E16.0.3.0");var subQ1=sQuery(id+"F9.wireOp",EDGE,"E13");var subQ2=makeQuery(id+"F9.imprint","INTERSECT",VERTEX,{"disambiguationData":[OD(2.0)],"derivedFrom":[subQ1,subQ0]});Q12=makeQuery(id+"F9.imprint","IMPRINT",FACE,{"disambiguationData":[TD([[makeQuery(id+"F9.imprint","IMPRINT",EDGE,{"disambiguationData":[TD([[subQ2,-1.0]])],"derivedFrom":subQ1}),1.0]])]});}
            var Q13;
            {var subQ0=sQuery(id+"F9.wireOp",EDGE,"E16.0.3.0");var subQ1=sQuery(id+"F9.wireOp",EDGE,"E14.0.1.0");var subQ2=makeQuery(id+"F9.imprint","INTERSECT",VERTEX,{"disambiguationData":[OD(2.0)],"derivedFrom":[subQ1,subQ0]});Q13=makeQuery(id+"F9.imprint","IMPRINT",FACE,{"disambiguationData":[TD([[makeQuery(id+"F9.imprint","IMPRINT",EDGE,{"disambiguationData":[TD([[subQ2,-1.0]])],"derivedFrom":subQ1}),1.0]])]});}
            var Q14;
            {var subQ1=sQuery(id+"F9.wireOp",EDGE,"E13");var subQ7=sQuery(id+"F9.wireOp",EDGE,"E14.0.3.0");var subQ8=makeQuery(id+"F9.imprint","INTERSECT",VERTEX,{"disambiguationData":[OD(1.0)],"derivedFrom":[subQ1,subQ7]});Q14=makeQuery(id+"F9.imprint","IMPRINT",FACE,{"disambiguationData":[TD([[makeQuery(id+"F9.imprint","IMPRINT",EDGE,{"disambiguationData":[TD([[subQ8,-1.0]])],"derivedFrom":subQ1}),1.0]])]});}
            var Q15;
            {var subQ0=sQuery(id+"F9.wireOp",EDGE,"E16.0.3.0");var subQ1=sQuery(id+"F9.wireOp",EDGE,"E13");var subQ2=makeQuery(id+"F9.imprint","INTERSECT",VERTEX,{"disambiguationData":[OD(1.0)],"derivedFrom":[subQ1,subQ0]});Q15=makeQuery(id+"F9.imprint","IMPRINT",FACE,{"disambiguationData":[TD([[makeQuery(id+"F9.imprint","IMPRINT",EDGE,{"disambiguationData":[TD([[subQ2,-1.0]])],"derivedFrom":subQ1}),1.0]])]});}
            var Q16;
            {var subQ0=sQuery(id+"F9.wireOp",EDGE,"E17.0.0.4");var subQ1=sQuery(id+"F9.wireOp",EDGE,"E13");var subQ2=makeQuery(id+"F9.imprint","INTERSECT",VERTEX,{"disambiguationData":[OD(3.0)],"derivedFrom":[subQ1,subQ0]});Q16=makeQuery(id+"F9.imprint","IMPRINT",FACE,{"disambiguationData":[TD([[makeQuery(id+"F9.imprint","IMPRINT",EDGE,{"disambiguationData":[TD([[subQ2,-1.0]])],"derivedFrom":subQ1}),1.0]])]});}
            var Q17;
            {var subQ0=sQuery(id+"F9.wireOp",EDGE,"E17.0.0.4");var subQ1=sQuery(id+"F9.wireOp",EDGE,"E14.0.1.0");var subQ2=makeQuery(id+"F9.imprint","INTERSECT",VERTEX,{"disambiguationData":[OD(3.0)],"derivedFrom":[subQ1,subQ0]});Q17=makeQuery(id+"F9.imprint","IMPRINT",FACE,{"disambiguationData":[TD([[makeQuery(id+"F9.imprint","IMPRINT",EDGE,{"disambiguationData":[TD([[subQ2,-1.0]])],"derivedFrom":subQ1}),1.0]])]});}
            var Q18;
            {var subQ0=sQuery(id+"F9.wireOp",EDGE,"E16.0.3.0");var subQ1=sQuery(id+"F9.wireOp",EDGE,"E13");var subQ2=makeQuery(id+"F9.imprint","INTERSECT",VERTEX,{"disambiguationData":[OD(0.0)],"derivedFrom":[subQ1,subQ0]});Q18=makeQuery(id+"F9.imprint","IMPRINT",FACE,{"disambiguationData":[TD([[makeQuery(id+"F9.imprint","IMPRINT",EDGE,{"disambiguationData":[TD([[subQ2,-1.0]])],"derivedFrom":subQ1}),1.0]])]});}
            extrude(context, id + "F11", {"entities" : qUnion([Q0, Q1, Q2, Q3, Q4, Q5, Q6, Q7, Q8, Q9, Q10, Q11, Q12, Q13, Q14, Q15, Q16, Q17, Q18]), "depth" : 2133.6 * mm});
        }
        {
            var Q0;
            {var subQ0=sQuery(id+"F9.wireOp",EDGE,"E17.0.0.4");var subQ1=sQuery(id+"F9.wireOp",EDGE,"E14.0.2.0");var subQ2=makeQuery(id+"F9.imprint","INTERSECT",VERTEX,{"disambiguationData":[OD(2.0)],"derivedFrom":[subQ1,subQ0]});Q0=makeQuery(id+"F9.imprint","IMPRINT",FACE,{"disambiguationData":[TD([[makeQuery(id+"F9.imprint","IMPRINT",EDGE,{"disambiguationData":[TD([[subQ2,-1.0]])],"derivedFrom":subQ1}),1.0]])]});}
            var Q1;
            {var subQ0=sQuery(id+"F9.wireOp",EDGE,"E17.0.0.5");var subQ1=sQuery(id+"F9.wireOp",EDGE,"E13");var subQ2=makeQuery(id+"F9.imprint","INTERSECT",VERTEX,{"disambiguationData":[OD(1.0)],"derivedFrom":[subQ1,subQ0]});Q1=makeQuery(id+"F9.imprint","IMPRINT",FACE,{"disambiguationData":[TD([[makeQuery(id+"F9.imprint","IMPRINT",EDGE,{"disambiguationData":[TD([[subQ2,-1.0]])],"derivedFrom":subQ1}),1.0]])]});}
            var Q2;
            {var subQ0=sQuery(id+"F9.wireOp",EDGE,"E18.0.0.4");var subQ1=sQuery(id+"F9.wireOp",EDGE,"E14.0.1.0");var subQ2=makeQuery(id+"F9.imprint","INTERSECT",VERTEX,{"disambiguationData":[OD(1.0)],"derivedFrom":[subQ1,subQ0]});Q2=makeQuery(id+"F9.imprint","IMPRINT",FACE,{"disambiguationData":[TD([[makeQuery(id+"F9.imprint","IMPRINT",EDGE,{"disambiguationData":[TD([[subQ2,-1.0]])],"derivedFrom":subQ1}),-1.0]])]});}
            var Q3;
            {var subQ0=sQuery(id+"F9.wireOp",EDGE,"E17.0.0.4");var subQ1=sQuery(id+"F9.wireOp",EDGE,"E14.0.1.0");var subQ2=makeQuery(id+"F9.imprint","INTERSECT",VERTEX,{"disambiguationData":[OD(2.0)],"derivedFrom":[subQ1,subQ0]});Q3=makeQuery(id+"F9.imprint","IMPRINT",FACE,{"disambiguationData":[TD([[makeQuery(id+"F9.imprint","IMPRINT",EDGE,{"disambiguationData":[TD([[subQ2,-1.0]])],"derivedFrom":subQ1}),1.0]])]});}
            var Q4;
            {var subQ0=sQuery(id+"F9.wireOp",EDGE,"E17.0.0.4");var subQ1=sQuery(id+"F9.wireOp",EDGE,"E13");var subQ2=makeQuery(id+"F9.imprint","INTERSECT",VERTEX,{"disambiguationData":[OD(2.0)],"derivedFrom":[subQ1,subQ0]});Q4=makeQuery(id+"F9.imprint","IMPRINT",FACE,{"disambiguationData":[TD([[makeQuery(id+"F9.imprint","IMPRINT",EDGE,{"disambiguationData":[TD([[subQ2,-1.0]])],"derivedFrom":subQ1}),1.0]])]});}
            var Q5;
            {var subQ0=sQuery(id+"F9.wireOp",EDGE,"E17.0.0.4");var subQ1=sQuery(id+"F9.wireOp",EDGE,"E13");var subQ2=makeQuery(id+"F9.imprint","INTERSECT",VERTEX,{"disambiguationData":[OD(2.0)],"derivedFrom":[subQ1,subQ0]});Q5=makeQuery(id+"F9.imprint","IMPRINT",FACE,{"disambiguationData":[TD([[makeQuery(id+"F9.imprint","IMPRINT",EDGE,{"disambiguationData":[TD([[subQ2,-1.0]])],"derivedFrom":subQ1}),-1.0]])]});}
            var Q6;
            {var subQ0=sQuery(id+"F9.wireOp",EDGE,"E17.0.0.5");var subQ1=sQuery(id+"F9.wireOp",EDGE,"E13");var subQ2=makeQuery(id+"F9.imprint","INTERSECT",VERTEX,{"disambiguationData":[OD(2.0)],"derivedFrom":[subQ1,subQ0]});Q6=makeQuery(id+"F9.imprint","IMPRINT",FACE,{"disambiguationData":[TD([[makeQuery(id+"F9.imprint","IMPRINT",EDGE,{"disambiguationData":[TD([[subQ2,-1.0]])],"derivedFrom":subQ1}),1.0]])]});}
            var Q7;
            {var subQ0=sQuery(id+"F9.wireOp",EDGE,"E17.0.0.5");var subQ1=sQuery(id+"F9.wireOp",EDGE,"E14.0.1.0");var subQ2=makeQuery(id+"F9.imprint","INTERSECT",VERTEX,{"disambiguationData":[OD(3.0)],"derivedFrom":[subQ1,subQ0]});Q7=makeQuery(id+"F9.imprint","IMPRINT",FACE,{"disambiguationData":[TD([[makeQuery(id+"F9.imprint","IMPRINT",EDGE,{"disambiguationData":[TD([[subQ2,-1.0]])],"derivedFrom":subQ1}),1.0]])]});}
            var Q8;
            {var subQ0=sQuery(id+"F9.wireOp",EDGE,"E17.0.0.5");var subQ1=sQuery(id+"F9.wireOp",EDGE,"E14.0.2.0");var subQ2=makeQuery(id+"F9.imprint","INTERSECT",VERTEX,{"disambiguationData":[OD(3.0)],"derivedFrom":[subQ1,subQ0]});Q8=makeQuery(id+"F9.imprint","IMPRINT",FACE,{"disambiguationData":[TD([[makeQuery(id+"F9.imprint","IMPRINT",EDGE,{"disambiguationData":[TD([[subQ2,-1.0]])],"derivedFrom":subQ1}),1.0]])]});}
            var Q9;
            {var subQ0=sQuery(id+"F9.wireOp",EDGE,"E17.0.0.4");var subQ1=sQuery(id+"F9.wireOp",EDGE,"E13");var subQ2=makeQuery(id+"F9.imprint","INTERSECT",VERTEX,{"disambiguationData":[OD(0.0)],"derivedFrom":[subQ1,subQ0]});Q9=makeQuery(id+"F9.imprint","IMPRINT",FACE,{"disambiguationData":[TD([[makeQuery(id+"F9.imprint","IMPRINT",EDGE,{"disambiguationData":[TD([[subQ2,-1.0]])],"derivedFrom":subQ1}),1.0]])]});}
            var Q10;
            {var subQ1=sQuery(id+"F9.wireOp",EDGE,"E13");var subQ5=sQuery(id+"F9.wireOp",EDGE,"E17.0.0.4");var subQ6=makeQuery(id+"F9.imprint","INTERSECT",VERTEX,{"disambiguationData":[OD(0.0)],"derivedFrom":[subQ1,subQ5]});Q10=makeQuery(id+"F9.imprint","IMPRINT",FACE,{"disambiguationData":[TD([[makeQuery(id+"F9.imprint","IMPRINT",EDGE,{"disambiguationData":[TD([[subQ6,-1.0]])],"derivedFrom":subQ1}),-1.0]])]});}
            var Q11;
            {var subQ0=sQuery(id+"F9.wireOp",EDGE,"E17.0.0.5");var subQ1=sQuery(id+"F9.wireOp",EDGE,"E13");var subQ2=makeQuery(id+"F9.imprint","INTERSECT",VERTEX,{"disambiguationData":[OD(1.0)],"derivedFrom":[subQ1,subQ0]});Q11=makeQuery(id+"F9.imprint","IMPRINT",FACE,{"disambiguationData":[TD([[makeQuery(id+"F9.imprint","IMPRINT",EDGE,{"disambiguationData":[TD([[subQ2,-1.0]])],"derivedFrom":subQ1}),-1.0]])]});}
            var Q12;
            {var subQ0=sQuery(id+"F9.wireOp",EDGE,"E18.0.0.4");var subQ1=sQuery(id+"F9.wireOp",EDGE,"E14.0.1.0");var subQ2=makeQuery(id+"F9.imprint","INTERSECT",VERTEX,{"disambiguationData":[OD(1.0)],"derivedFrom":[subQ1,subQ0]});Q12=makeQuery(id+"F9.imprint","IMPRINT",FACE,{"disambiguationData":[TD([[makeQuery(id+"F9.imprint","IMPRINT",EDGE,{"disambiguationData":[TD([[subQ2,-1.0]])],"derivedFrom":subQ1}),1.0]])]});}
            var Q13;
            {var subQ0=sQuery(id+"F9.wireOp",EDGE,"E18.0.0.4");var subQ1=sQuery(id+"F9.wireOp",EDGE,"E14.0.2.0");var subQ2=makeQuery(id+"F9.imprint","INTERSECT",VERTEX,{"disambiguationData":[OD(1.0)],"derivedFrom":[subQ1,subQ0]});Q13=makeQuery(id+"F9.imprint","IMPRINT",FACE,{"disambiguationData":[TD([[makeQuery(id+"F9.imprint","IMPRINT",EDGE,{"disambiguationData":[TD([[subQ2,-1.0]])],"derivedFrom":subQ1}),1.0]])]});}
            var Q14;
            {var subQ0=sQuery(id+"F9.wireOp",EDGE,"E17.0.0.4");var subQ1=sQuery(id+"F9.wireOp",EDGE,"E14.0.1.0");var subQ2=makeQuery(id+"F9.imprint","INTERSECT",VERTEX,{"disambiguationData":[OD(0.0)],"derivedFrom":[subQ1,subQ0]});Q14=makeQuery(id+"F9.imprint","IMPRINT",FACE,{"disambiguationData":[TD([[makeQuery(id+"F9.imprint","IMPRINT",EDGE,{"disambiguationData":[TD([[subQ2,-1.0]])],"derivedFrom":subQ1}),-1.0]])]});}
            var Q15;
            {var subQ0=sQuery(id+"F9.wireOp",EDGE,"E17.0.0.4");var subQ1=sQuery(id+"F9.wireOp",EDGE,"E14.0.1.0");var subQ2=makeQuery(id+"F9.imprint","INTERSECT",VERTEX,{"disambiguationData":[OD(0.0)],"derivedFrom":[subQ1,subQ0]});Q15=makeQuery(id+"F9.imprint","IMPRINT",FACE,{"disambiguationData":[TD([[makeQuery(id+"F9.imprint","IMPRINT",EDGE,{"disambiguationData":[TD([[subQ2,-1.0]])],"derivedFrom":subQ1}),1.0]])]});}
            var Q16;
            {var subQ0=sQuery(id+"F9.wireOp",EDGE,"E17.0.0.4");var subQ1=sQuery(id+"F9.wireOp",EDGE,"E14.0.2.0");var subQ2=makeQuery(id+"F9.imprint","INTERSECT",VERTEX,{"disambiguationData":[OD(0.0)],"derivedFrom":[subQ1,subQ0]});Q16=makeQuery(id+"F9.imprint","IMPRINT",FACE,{"disambiguationData":[TD([[makeQuery(id+"F9.imprint","IMPRINT",EDGE,{"disambiguationData":[TD([[subQ2,-1.0]])],"derivedFrom":subQ1}),1.0]])]});}
            var Q17;
            {var subQ0=sQuery(id+"F9.wireOp",EDGE,"E18.0.0.4");var subQ1=sQuery(id+"F9.wireOp",EDGE,"E14.0.1.0");var subQ2=makeQuery(id+"F9.imprint","INTERSECT",VERTEX,{"disambiguationData":[OD(0.0)],"derivedFrom":[subQ1,subQ0]});Q17=makeQuery(id+"F9.imprint","IMPRINT",FACE,{"disambiguationData":[TD([[makeQuery(id+"F9.imprint","IMPRINT",EDGE,{"disambiguationData":[TD([[subQ2,-1.0]])],"derivedFrom":subQ1}),-1.0]])]});}
            var Q18;
            {var subQ0=sQuery(id+"F9.wireOp",EDGE,"E18.0.0.4");var subQ1=sQuery(id+"F9.wireOp",EDGE,"E14.0.1.0");var subQ2=makeQuery(id+"F9.imprint","INTERSECT",VERTEX,{"disambiguationData":[OD(0.0)],"derivedFrom":[subQ1,subQ0]});Q18=makeQuery(id+"F9.imprint","IMPRINT",FACE,{"disambiguationData":[TD([[makeQuery(id+"F9.imprint","IMPRINT",EDGE,{"disambiguationData":[TD([[subQ2,-1.0]])],"derivedFrom":subQ1}),1.0]])]});}
            var Q19;
            {var subQ0=sQuery(id+"F9.wireOp",EDGE,"E18.0.0.4");var subQ1=sQuery(id+"F9.wireOp",EDGE,"E15");var subQ2=makeQuery(id+"F9.imprint","INTERSECT",VERTEX,{"disambiguationData":[OD(0.0)],"derivedFrom":[subQ1,subQ0]});Q19=makeQuery(id+"F9.imprint","IMPRINT",FACE,{"disambiguationData":[TD([[makeQuery(id+"F9.imprint","IMPRINT",EDGE,{"disambiguationData":[TD([[subQ2,-1.0]])],"derivedFrom":subQ1}),1.0]])]});}
            var Q20;
            {var subQ0=sQuery(id+"F9.wireOp",EDGE,"E18.0.0.4");var subQ1=sQuery(id+"F9.wireOp",EDGE,"E14.0.2.0");var subQ2=makeQuery(id+"F9.imprint","INTERSECT",VERTEX,{"disambiguationData":[OD(0.0)],"derivedFrom":[subQ1,subQ0]});Q20=makeQuery(id+"F9.imprint","IMPRINT",FACE,{"disambiguationData":[TD([[makeQuery(id+"F9.imprint","IMPRINT",EDGE,{"disambiguationData":[TD([[subQ2,-1.0]])],"derivedFrom":subQ1}),1.0]])]});}
            var Q21;
            {var subQ0=sQuery(id+"F9.wireOp",EDGE,"E17.0.0.4");var subQ1=sQuery(id+"F9.wireOp",EDGE,"E14.0.2.0");var subQ2=makeQuery(id+"F9.imprint","INTERSECT",VERTEX,{"disambiguationData":[OD(0.0)],"derivedFrom":[subQ1,subQ0]});Q21=makeQuery(id+"F9.imprint","IMPRINT",FACE,{"disambiguationData":[TD([[makeQuery(id+"F9.imprint","IMPRINT",EDGE,{"disambiguationData":[TD([[subQ2,-1.0]])],"derivedFrom":subQ1}),-1.0]])]});}
            var Q22;
            {var subQ0=sQuery(id+"F9.wireOp",EDGE,"E18.0.0.4");var subQ1=sQuery(id+"F9.wireOp",EDGE,"E14.0.2.0");var subQ2=makeQuery(id+"F9.imprint","INTERSECT",VERTEX,{"disambiguationData":[OD(0.0)],"derivedFrom":[subQ1,subQ0]});Q22=makeQuery(id+"F9.imprint","IMPRINT",FACE,{"disambiguationData":[TD([[makeQuery(id+"F9.imprint","IMPRINT",EDGE,{"disambiguationData":[TD([[subQ2,-1.0]])],"derivedFrom":subQ1}),-1.0]])]});}
            var Q23;
            {var subQ0=sQuery(id+"F9.wireOp",EDGE,"E17.0.0.4");var subQ1=sQuery(id+"F9.wireOp",EDGE,"E14.0.3.0");var subQ2=makeQuery(id+"F9.imprint","INTERSECT",VERTEX,{"disambiguationData":[OD(0.0)],"derivedFrom":[subQ1,subQ0]});Q23=makeQuery(id+"F9.imprint","IMPRINT",FACE,{"disambiguationData":[TD([[makeQuery(id+"F9.imprint","IMPRINT",EDGE,{"disambiguationData":[TD([[subQ2,-1.0]])],"derivedFrom":subQ1}),1.0]])]});}
            var Q24;
            {var subQ0=sQuery(id+"F9.wireOp",EDGE,"E18.0.0.4");var subQ1=sQuery(id+"F9.wireOp",EDGE,"E14.0.3.0");var subQ2=makeQuery(id+"F9.imprint","INTERSECT",VERTEX,{"disambiguationData":[OD(0.0)],"derivedFrom":[subQ1,subQ0]});Q24=makeQuery(id+"F9.imprint","IMPRINT",FACE,{"disambiguationData":[TD([[makeQuery(id+"F9.imprint","IMPRINT",EDGE,{"disambiguationData":[TD([[subQ2,-1.0]])],"derivedFrom":subQ1}),1.0]])]});}
            var Q25;
            {var subQ0=sQuery(id+"F9.wireOp",EDGE,"E17.0.0.5");var subQ1=sQuery(id+"F9.wireOp",EDGE,"E14.0.2.0");var subQ2=makeQuery(id+"F9.imprint","INTERSECT",VERTEX,{"disambiguationData":[OD(1.0)],"derivedFrom":[subQ1,subQ0]});Q25=makeQuery(id+"F9.imprint","IMPRINT",FACE,{"disambiguationData":[TD([[makeQuery(id+"F9.imprint","IMPRINT",EDGE,{"disambiguationData":[TD([[subQ2,-1.0]])],"derivedFrom":subQ1}),1.0]])]});}
            var Q26;
            {var subQ0=sQuery(id+"F9.wireOp",EDGE,"E17.0.0.5");var subQ1=sQuery(id+"F9.wireOp",EDGE,"E14.0.1.0");var subQ2=makeQuery(id+"F9.imprint","INTERSECT",VERTEX,{"disambiguationData":[OD(1.0)],"derivedFrom":[subQ1,subQ0]});Q26=makeQuery(id+"F9.imprint","IMPRINT",FACE,{"disambiguationData":[TD([[makeQuery(id+"F9.imprint","IMPRINT",EDGE,{"disambiguationData":[TD([[subQ2,-1.0]])],"derivedFrom":subQ1}),-1.0]])]});}
            var Q27;
            {var subQ0=sQuery(id+"F9.wireOp",EDGE,"E17.0.0.5");var subQ1=sQuery(id+"F9.wireOp",EDGE,"E14.0.1.0");var subQ2=makeQuery(id+"F9.imprint","INTERSECT",VERTEX,{"disambiguationData":[OD(1.0)],"derivedFrom":[subQ1,subQ0]});Q27=makeQuery(id+"F9.imprint","IMPRINT",FACE,{"disambiguationData":[TD([[makeQuery(id+"F9.imprint","IMPRINT",EDGE,{"disambiguationData":[TD([[subQ2,-1.0]])],"derivedFrom":subQ1}),1.0]])]});}
            var Q28;
            {var subQ0=sQuery(id+"F9.wireOp",EDGE,"E17.0.0.5");var subQ1=sQuery(id+"F9.wireOp",EDGE,"E15");var subQ2=makeQuery(id+"F9.imprint","INTERSECT",VERTEX,{"disambiguationData":[OD(1.0)],"derivedFrom":[subQ1,subQ0]});Q28=makeQuery(id+"F9.imprint","IMPRINT",FACE,{"disambiguationData":[TD([[makeQuery(id+"F9.imprint","IMPRINT",EDGE,{"disambiguationData":[TD([[subQ2,-1.0]])],"derivedFrom":subQ1}),1.0]])]});}
            var Q29;
            {var subQ0=sQuery(id+"F9.wireOp",EDGE,"E18.0.0.4");var subQ1=sQuery(id+"F9.wireOp",EDGE,"E14.0.2.0");var subQ2=makeQuery(id+"F9.imprint","INTERSECT",VERTEX,{"disambiguationData":[OD(1.0)],"derivedFrom":[subQ1,subQ0]});Q29=makeQuery(id+"F9.imprint","IMPRINT",FACE,{"disambiguationData":[TD([[makeQuery(id+"F9.imprint","IMPRINT",EDGE,{"disambiguationData":[TD([[subQ2,-1.0]])],"derivedFrom":subQ1}),-1.0]])]});}
            var Q30;
            {var subQ0=sQuery(id+"F9.wireOp",EDGE,"E17.0.0.5");var subQ1=sQuery(id+"F9.wireOp",EDGE,"E14.0.2.0");var subQ2=makeQuery(id+"F9.imprint","INTERSECT",VERTEX,{"disambiguationData":[OD(1.0)],"derivedFrom":[subQ1,subQ0]});Q30=makeQuery(id+"F9.imprint","IMPRINT",FACE,{"disambiguationData":[TD([[makeQuery(id+"F9.imprint","IMPRINT",EDGE,{"disambiguationData":[TD([[subQ2,-1.0]])],"derivedFrom":subQ1}),-1.0]])]});}
            var Q31;
            {var subQ0=sQuery(id+"F9.wireOp",EDGE,"E17.0.0.5");var subQ1=sQuery(id+"F9.wireOp",EDGE,"E14.0.3.0");var subQ2=makeQuery(id+"F9.imprint","INTERSECT",VERTEX,{"disambiguationData":[OD(1.0)],"derivedFrom":[subQ1,subQ0]});Q31=makeQuery(id+"F9.imprint","IMPRINT",FACE,{"disambiguationData":[TD([[makeQuery(id+"F9.imprint","IMPRINT",EDGE,{"disambiguationData":[TD([[subQ2,-1.0]])],"derivedFrom":subQ1}),1.0]])]});}
            var Q32;
            {var subQ0=sQuery(id+"F9.wireOp",EDGE,"E18.0.0.4");var subQ1=sQuery(id+"F9.wireOp",EDGE,"E14.0.3.0");var subQ2=makeQuery(id+"F9.imprint","INTERSECT",VERTEX,{"disambiguationData":[OD(1.0)],"derivedFrom":[subQ1,subQ0]});Q32=makeQuery(id+"F9.imprint","IMPRINT",FACE,{"disambiguationData":[TD([[makeQuery(id+"F9.imprint","IMPRINT",EDGE,{"disambiguationData":[TD([[subQ2,-1.0]])],"derivedFrom":subQ1}),1.0]])]});}
            extrude(context, id + "F12", {"entities" : qUnion([Q0, Q1, Q2, Q3, Q4, Q5, Q6, Q7, Q8, Q9, Q10, Q11, Q12, Q13, Q14, Q15, Q16, Q17, Q18, Q19, Q20, Q21, Q22, Q23, Q24, Q25, Q26, Q27, Q28, Q29, Q30, Q31, Q32]), "depth" : 25.4 * mm});
        }
        {
            var Q0;
            {var subQ0=sQuery(id+"F9.wireOp",EDGE,"E17.0.0.7");var subQ1=sQuery(id+"F9.wireOp",EDGE,"E14.0.3.0");var subQ2=makeQuery(id+"F9.imprint","INTERSECT",VERTEX,{"disambiguationData":[OD(2.0)],"derivedFrom":[subQ1,subQ0]});Q0=makeQuery(id+"F9.imprint","IMPRINT",FACE,{"disambiguationData":[TD([[makeQuery(id+"F9.imprint","IMPRINT",EDGE,{"disambiguationData":[TD([[subQ2,-1.0]])],"derivedFrom":subQ1}),-1.0]])]});}
            var Q1;
            {var subQ0=sQuery(id+"F9.wireOp",EDGE,"E17.0.0.7");var subQ1=sQuery(id+"F9.wireOp",EDGE,"E14.0.2.0");var subQ2=makeQuery(id+"F9.imprint","INTERSECT",VERTEX,{"disambiguationData":[OD(2.0)],"derivedFrom":[subQ1,subQ0]});Q1=makeQuery(id+"F9.imprint","IMPRINT",FACE,{"disambiguationData":[TD([[makeQuery(id+"F9.imprint","IMPRINT",EDGE,{"disambiguationData":[TD([[subQ2,-1.0]])],"derivedFrom":subQ1}),1.0]])]});}
            var Q2;
            {var subQ0=sQuery(id+"F9.wireOp",EDGE,"E17.0.0.8");var subQ1=sQuery(id+"F9.wireOp",EDGE,"E14.0.3.0");var subQ2=makeQuery(id+"F9.imprint","INTERSECT",VERTEX,{"disambiguationData":[OD(2.0)],"derivedFrom":[subQ1,subQ0]});Q2=makeQuery(id+"F9.imprint","IMPRINT",FACE,{"disambiguationData":[TD([[makeQuery(id+"F9.imprint","IMPRINT",EDGE,{"disambiguationData":[TD([[subQ2,-1.0]])],"derivedFrom":subQ1}),1.0]])]});}
            var Q3;
            {var subQ0=sQuery(id+"F9.wireOp",EDGE,"E17.0.0.7");var subQ1=sQuery(id+"F9.wireOp",EDGE,"E14.0.3.0");var subQ2=makeQuery(id+"F9.imprint","INTERSECT",VERTEX,{"disambiguationData":[OD(3.0)],"derivedFrom":[subQ1,subQ0]});Q3=makeQuery(id+"F9.imprint","IMPRINT",FACE,{"disambiguationData":[TD([[makeQuery(id+"F9.imprint","IMPRINT",EDGE,{"disambiguationData":[TD([[subQ2,-1.0]])],"derivedFrom":subQ1}),1.0]])]});}
            var Q4;
            {var subQ3=sQuery(id+"F9.wireOp",EDGE,"E17.0.0.5");var subQ7=sQuery(id+"F9.wireOp",EDGE,"E13");var subQ8=makeQuery(id+"F9.imprint","INTERSECT",VERTEX,{"disambiguationData":[OD(0.0)],"derivedFrom":[subQ7,subQ3]});Q4=makeQuery(id+"F9.imprint","IMPRINT",FACE,{"disambiguationData":[TD([[makeQuery(id+"F9.imprint","IMPRINT",EDGE,{"disambiguationData":[TD([[subQ8,-1.0]])],"derivedFrom":subQ7}),1.0]])]});}
            var Q5;
            {var subQ0=sQuery(id+"F9.wireOp",EDGE,"E18.0.0.4");var subQ1=sQuery(id+"F9.wireOp",EDGE,"E17.0.0.7");var subQ2=makeQuery(id+"F9.imprint","INTERSECT",VERTEX,{"disambiguationData":[OD(2.0)],"derivedFrom":[subQ1,subQ0]});Q5=makeQuery(id+"F9.imprint","IMPRINT",FACE,{"disambiguationData":[TD([[makeQuery(id+"F9.imprint","IMPRINT",EDGE,{"disambiguationData":[TD([[subQ2,-1.0]])],"derivedFrom":subQ1}),1.0]])]});}
            var Q6;
            {var subQ5=sQuery(id+"F9.wireOp",EDGE,"E17.0.0.6");var subQ7=sQuery(id+"F9.wireOp",EDGE,"E13");var subQ8=makeQuery(id+"F9.imprint","INTERSECT",VERTEX,{"disambiguationData":[OD(0.0)],"derivedFrom":[subQ7,subQ5]});Q6=makeQuery(id+"F9.imprint","IMPRINT",FACE,{"disambiguationData":[TD([[makeQuery(id+"F9.imprint","IMPRINT",EDGE,{"disambiguationData":[TD([[subQ8,-1.0]])],"derivedFrom":subQ7}),1.0]])]});}
            var Q7;
            {var subQ0=sQuery(id+"F9.wireOp",EDGE,"E17.0.0.6");var subQ1=sQuery(id+"F9.wireOp",EDGE,"E14.0.2.0");var subQ2=makeQuery(id+"F9.imprint","INTERSECT",VERTEX,{"disambiguationData":[OD(3.0)],"derivedFrom":[subQ1,subQ0]});Q7=makeQuery(id+"F9.imprint","IMPRINT",FACE,{"disambiguationData":[TD([[makeQuery(id+"F9.imprint","IMPRINT",EDGE,{"disambiguationData":[TD([[subQ2,-1.0]])],"derivedFrom":subQ1}),1.0]])]});}
            var Q8;
            {var subQ0=sQuery(id+"F9.wireOp",EDGE,"E17.0.0.6");var subQ1=sQuery(id+"F9.wireOp",EDGE,"E14.0.2.0");var subQ2=makeQuery(id+"F9.imprint","INTERSECT",VERTEX,{"disambiguationData":[OD(2.0)],"derivedFrom":[subQ1,subQ0]});Q8=makeQuery(id+"F9.imprint","IMPRINT",FACE,{"disambiguationData":[TD([[makeQuery(id+"F9.imprint","IMPRINT",EDGE,{"disambiguationData":[TD([[subQ2,-1.0]])],"derivedFrom":subQ1}),1.0]])]});}
            var Q9;
            {var subQ0=sQuery(id+"F9.wireOp",EDGE,"E17.0.0.7");var subQ1=sQuery(id+"F9.wireOp",EDGE,"E14.0.3.0");var subQ2=makeQuery(id+"F9.imprint","INTERSECT",VERTEX,{"disambiguationData":[OD(2.0)],"derivedFrom":[subQ1,subQ0]});Q9=makeQuery(id+"F9.imprint","IMPRINT",FACE,{"disambiguationData":[TD([[makeQuery(id+"F9.imprint","IMPRINT",EDGE,{"disambiguationData":[TD([[subQ2,-1.0]])],"derivedFrom":subQ1}),1.0]])]});}
            var Q10;
            {var subQ0=sQuery(id+"F9.wireOp",EDGE,"E17.0.0.5");var subQ1=sQuery(id+"F9.wireOp",EDGE,"E14.0.2.0");var subQ2=makeQuery(id+"F9.imprint","INTERSECT",VERTEX,{"disambiguationData":[OD(2.0)],"derivedFrom":[subQ1,subQ0]});Q10=makeQuery(id+"F9.imprint","IMPRINT",FACE,{"disambiguationData":[TD([[makeQuery(id+"F9.imprint","IMPRINT",EDGE,{"disambiguationData":[TD([[subQ2,-1.0]])],"derivedFrom":subQ1}),1.0]])]});}
            var Q11;
            {var subQ0=sQuery(id+"F9.wireOp",EDGE,"E17.0.0.6");var subQ1=sQuery(id+"F9.wireOp",EDGE,"E14.0.3.0");var subQ2=makeQuery(id+"F9.imprint","INTERSECT",VERTEX,{"disambiguationData":[OD(2.0)],"derivedFrom":[subQ1,subQ0]});Q11=makeQuery(id+"F9.imprint","IMPRINT",FACE,{"disambiguationData":[TD([[makeQuery(id+"F9.imprint","IMPRINT",EDGE,{"disambiguationData":[TD([[subQ2,-1.0]])],"derivedFrom":subQ1}),1.0]])]});}
            var Q12;
            {var subQ0=sQuery(id+"F9.wireOp",EDGE,"E18.0.0.5");var subQ1=sQuery(id+"F9.wireOp",EDGE,"E17.0.0.7");var subQ2=makeQuery(id+"F9.imprint","INTERSECT",VERTEX,{"disambiguationData":[OD(1.0)],"derivedFrom":[subQ1,subQ0]});Q12=makeQuery(id+"F9.imprint","IMPRINT",FACE,{"disambiguationData":[TD([[makeQuery(id+"F9.imprint","IMPRINT",EDGE,{"disambiguationData":[TD([[subQ2,-1.0]])],"derivedFrom":subQ1}),1.0]])]});}
            var Q13;
            {var subQ0=sQuery(id+"F9.wireOp",EDGE,"E18.0.0.4");var subQ1=sQuery(id+"F9.wireOp",EDGE,"E13");var subQ2=makeQuery(id+"F9.imprint","INTERSECT",VERTEX,{"disambiguationData":[OD(0.0)],"derivedFrom":[subQ1,subQ0]});Q13=makeQuery(id+"F9.imprint","IMPRINT",FACE,{"disambiguationData":[TD([[makeQuery(id+"F9.imprint","IMPRINT",EDGE,{"disambiguationData":[TD([[subQ2,-1.0]])],"derivedFrom":subQ1}),1.0]])]});}
            var Q14;
            {var subQ0=sQuery(id+"F9.wireOp",EDGE,"E18.0.0.5");var subQ1=sQuery(id+"F9.wireOp",EDGE,"E13");var subQ2=makeQuery(id+"F9.imprint","INTERSECT",VERTEX,{"disambiguationData":[OD(0.0)],"derivedFrom":[subQ1,subQ0]});Q14=makeQuery(id+"F9.imprint","IMPRINT",FACE,{"disambiguationData":[TD([[makeQuery(id+"F9.imprint","IMPRINT",EDGE,{"disambiguationData":[TD([[subQ2,-1.0]])],"derivedFrom":subQ1}),1.0]])]});}
            var Q15;
            {var subQ0=sQuery(id+"F9.wireOp",EDGE,"E17.0.0.7");var subQ1=sQuery(id+"F9.wireOp",EDGE,"E13");var subQ2=makeQuery(id+"F9.imprint","INTERSECT",VERTEX,{"disambiguationData":[OD(0.0)],"derivedFrom":[subQ1,subQ0]});Q15=makeQuery(id+"F9.imprint","IMPRINT",FACE,{"disambiguationData":[TD([[makeQuery(id+"F9.imprint","IMPRINT",EDGE,{"disambiguationData":[TD([[subQ2,-1.0]])],"derivedFrom":subQ1}),-1.0]])]});}
            var Q16;
            {var subQ0=sQuery(id+"F9.wireOp",EDGE,"E18.0.0.6");var subQ1=sQuery(id+"F9.wireOp",EDGE,"E13");var subQ2=makeQuery(id+"F9.imprint","INTERSECT",VERTEX,{"disambiguationData":[OD(0.0)],"derivedFrom":[subQ1,subQ0]});Q16=makeQuery(id+"F9.imprint","IMPRINT",FACE,{"disambiguationData":[TD([[makeQuery(id+"F9.imprint","IMPRINT",EDGE,{"disambiguationData":[TD([[subQ2,-1.0]])],"derivedFrom":subQ1}),-1.0]])]});}
            var Q17;
            {var subQ0=sQuery(id+"F9.wireOp",EDGE,"E18.0.0.5");var subQ1=sQuery(id+"F9.wireOp",EDGE,"E13");var subQ2=makeQuery(id+"F9.imprint","INTERSECT",VERTEX,{"disambiguationData":[OD(0.0)],"derivedFrom":[subQ1,subQ0]});Q17=makeQuery(id+"F9.imprint","IMPRINT",FACE,{"disambiguationData":[TD([[makeQuery(id+"F9.imprint","IMPRINT",EDGE,{"disambiguationData":[TD([[subQ2,-1.0]])],"derivedFrom":subQ1}),-1.0]])]});}
            var Q18;
            {var subQ0=sQuery(id+"F9.wireOp",EDGE,"E17.0.0.6");var subQ1=sQuery(id+"F9.wireOp",EDGE,"E13");var subQ2=makeQuery(id+"F9.imprint","INTERSECT",VERTEX,{"disambiguationData":[OD(0.0)],"derivedFrom":[subQ1,subQ0]});Q18=makeQuery(id+"F9.imprint","IMPRINT",FACE,{"disambiguationData":[TD([[makeQuery(id+"F9.imprint","IMPRINT",EDGE,{"disambiguationData":[TD([[subQ2,-1.0]])],"derivedFrom":subQ1}),-1.0]])]});}
            var Q19;
            {var subQ3=sQuery(id+"F9.wireOp",EDGE,"E18.0.0.4");var subQ9=sQuery(id+"F9.wireOp",EDGE,"E13");var subQ11=makeQuery(id+"F9.imprint","INTERSECT",VERTEX,{"disambiguationData":[OD(0.0)],"derivedFrom":[subQ9,subQ3]});Q19=makeQuery(id+"F9.imprint","IMPRINT",FACE,{"disambiguationData":[TD([[makeQuery(id+"F9.imprint","IMPRINT",EDGE,{"disambiguationData":[TD([[subQ11,-1.0]])],"derivedFrom":subQ9}),-1.0]])]});}
            var Q20;
            {var subQ0=sQuery(id+"F9.wireOp",EDGE,"E17.0.0.5");var subQ1=sQuery(id+"F9.wireOp",EDGE,"E13");var subQ2=makeQuery(id+"F9.imprint","INTERSECT",VERTEX,{"disambiguationData":[OD(0.0)],"derivedFrom":[subQ1,subQ0]});Q20=makeQuery(id+"F9.imprint","IMPRINT",FACE,{"disambiguationData":[TD([[makeQuery(id+"F9.imprint","IMPRINT",EDGE,{"disambiguationData":[TD([[subQ2,-1.0]])],"derivedFrom":subQ1}),-1.0]])]});}
            var Q21;
            {var subQ0=sQuery(id+"F9.wireOp",EDGE,"E18.0.0.6");var subQ1=sQuery(id+"F9.wireOp",EDGE,"E13");var subQ2=makeQuery(id+"F9.imprint","INTERSECT",VERTEX,{"disambiguationData":[OD(0.0)],"derivedFrom":[subQ1,subQ0]});Q21=makeQuery(id+"F9.imprint","IMPRINT",FACE,{"disambiguationData":[TD([[makeQuery(id+"F9.imprint","IMPRINT",EDGE,{"disambiguationData":[TD([[subQ2,-1.0]])],"derivedFrom":subQ1}),1.0]])]});}
            var Q22;
            {var subQ1=sQuery(id+"F9.wireOp",EDGE,"E13");var subQ7=sQuery(id+"F9.wireOp",EDGE,"E18.0.0.4");var subQ9=makeQuery(id+"F9.imprint","INTERSECT",VERTEX,{"disambiguationData":[OD(1.0)],"derivedFrom":[subQ1,subQ7]});Q22=makeQuery(id+"F9.imprint","IMPRINT",FACE,{"disambiguationData":[TD([[makeQuery(id+"F9.imprint","IMPRINT",EDGE,{"disambiguationData":[TD([[subQ9,-1.0]])],"derivedFrom":subQ1}),1.0]])]});}
            var Q23;
            {var subQ5=sQuery(id+"F9.wireOp",EDGE,"E18.0.0.5");var subQ7=sQuery(id+"F9.wireOp",EDGE,"E13");var subQ9=makeQuery(id+"F9.imprint","INTERSECT",VERTEX,{"disambiguationData":[OD(1.0)],"derivedFrom":[subQ7,subQ5]});Q23=makeQuery(id+"F9.imprint","IMPRINT",FACE,{"disambiguationData":[TD([[makeQuery(id+"F9.imprint","IMPRINT",EDGE,{"disambiguationData":[TD([[subQ9,-1.0]])],"derivedFrom":subQ7}),1.0]])]});}
            var Q24;
            {var subQ5=sQuery(id+"F9.wireOp",EDGE,"E13");var subQ7=sQuery(id+"F9.wireOp",EDGE,"E18.0.0.6");var subQ8=makeQuery(id+"F9.imprint","INTERSECT",VERTEX,{"disambiguationData":[OD(1.0)],"derivedFrom":[subQ5,subQ7]});Q24=makeQuery(id+"F9.imprint","IMPRINT",FACE,{"disambiguationData":[TD([[makeQuery(id+"F9.imprint","IMPRINT",EDGE,{"disambiguationData":[TD([[subQ8,-1.0]])],"derivedFrom":subQ5}),1.0]])]});}
            var Q25;
            {var subQ0=sQuery(id+"F9.wireOp",EDGE,"E17.0.0.7");var subQ1=sQuery(id+"F9.wireOp",EDGE,"E13");var subQ2=makeQuery(id+"F9.imprint","INTERSECT",VERTEX,{"disambiguationData":[OD(1.0)],"derivedFrom":[subQ1,subQ0]});Q25=makeQuery(id+"F9.imprint","IMPRINT",FACE,{"disambiguationData":[TD([[makeQuery(id+"F9.imprint","IMPRINT",EDGE,{"disambiguationData":[TD([[subQ2,-1.0]])],"derivedFrom":subQ1}),1.0]])]});}
            var Q26;
            {var subQ0=sQuery(id+"F9.wireOp",EDGE,"E17.0.0.6");var subQ1=sQuery(id+"F9.wireOp",EDGE,"E13");var subQ2=makeQuery(id+"F9.imprint","INTERSECT",VERTEX,{"disambiguationData":[OD(1.0)],"derivedFrom":[subQ1,subQ0]});Q26=makeQuery(id+"F9.imprint","IMPRINT",FACE,{"disambiguationData":[TD([[makeQuery(id+"F9.imprint","IMPRINT",EDGE,{"disambiguationData":[TD([[subQ2,-1.0]])],"derivedFrom":subQ1}),1.0]])]});}
            var Q27;
            {var subQ0=sQuery(id+"F9.wireOp",EDGE,"E18.0.0.4");var subQ1=sQuery(id+"F9.wireOp",EDGE,"E13");var subQ2=makeQuery(id+"F9.imprint","INTERSECT",VERTEX,{"disambiguationData":[OD(1.0)],"derivedFrom":[subQ1,subQ0]});Q27=makeQuery(id+"F9.imprint","IMPRINT",FACE,{"disambiguationData":[TD([[makeQuery(id+"F9.imprint","IMPRINT",EDGE,{"disambiguationData":[TD([[subQ2,-1.0]])],"derivedFrom":subQ1}),-1.0]])]});}
            var Q28;
            {var subQ7=sQuery(id+"F9.wireOp",EDGE,"E17.0.0.6");var subQ8=sQuery(id+"F9.wireOp",EDGE,"E13");var subQ9=makeQuery(id+"F9.imprint","INTERSECT",VERTEX,{"disambiguationData":[OD(1.0)],"derivedFrom":[subQ8,subQ7]});Q28=makeQuery(id+"F9.imprint","IMPRINT",FACE,{"disambiguationData":[TD([[makeQuery(id+"F9.imprint","IMPRINT",EDGE,{"disambiguationData":[TD([[subQ9,-1.0]])],"derivedFrom":subQ8}),-1.0]])]});}
            var Q29;
            {var subQ0=sQuery(id+"F9.wireOp",EDGE,"E18.0.0.5");var subQ1=sQuery(id+"F9.wireOp",EDGE,"E13");var subQ2=makeQuery(id+"F9.imprint","INTERSECT",VERTEX,{"disambiguationData":[OD(1.0)],"derivedFrom":[subQ1,subQ0]});Q29=makeQuery(id+"F9.imprint","IMPRINT",FACE,{"disambiguationData":[TD([[makeQuery(id+"F9.imprint","IMPRINT",EDGE,{"disambiguationData":[TD([[subQ2,-1.0]])],"derivedFrom":subQ1}),-1.0]])]});}
            var Q30;
            {var subQ0=sQuery(id+"F9.wireOp",EDGE,"E17.0.0.7");var subQ1=sQuery(id+"F9.wireOp",EDGE,"E13");var subQ2=makeQuery(id+"F9.imprint","INTERSECT",VERTEX,{"disambiguationData":[OD(1.0)],"derivedFrom":[subQ1,subQ0]});Q30=makeQuery(id+"F9.imprint","IMPRINT",FACE,{"disambiguationData":[TD([[makeQuery(id+"F9.imprint","IMPRINT",EDGE,{"disambiguationData":[TD([[subQ2,-1.0]])],"derivedFrom":subQ1}),-1.0]])]});}
            var Q31;
            {var subQ0=sQuery(id+"F9.wireOp",EDGE,"E18.0.0.6");var subQ1=sQuery(id+"F9.wireOp",EDGE,"E13");var subQ2=makeQuery(id+"F9.imprint","INTERSECT",VERTEX,{"disambiguationData":[OD(1.0)],"derivedFrom":[subQ1,subQ0]});Q31=makeQuery(id+"F9.imprint","IMPRINT",FACE,{"disambiguationData":[TD([[makeQuery(id+"F9.imprint","IMPRINT",EDGE,{"disambiguationData":[TD([[subQ2,-1.0]])],"derivedFrom":subQ1}),-1.0]])]});}
            var Q32;
            {var subQ0=sQuery(id+"F9.wireOp",EDGE,"E17.0.0.8");var subQ1=sQuery(id+"F9.wireOp",EDGE,"E13");var subQ2=makeQuery(id+"F9.imprint","INTERSECT",VERTEX,{"disambiguationData":[OD(1.0)],"derivedFrom":[subQ1,subQ0]});Q32=makeQuery(id+"F9.imprint","IMPRINT",FACE,{"disambiguationData":[TD([[makeQuery(id+"F9.imprint","IMPRINT",EDGE,{"disambiguationData":[TD([[subQ2,-1.0]])],"derivedFrom":subQ1}),1.0]])]});}
            var Q33;
            {var subQ0=sQuery(id+"F9.wireOp",EDGE,"E17.0.0.8");var subQ1=sQuery(id+"F9.wireOp",EDGE,"E13");var subQ2=makeQuery(id+"F9.imprint","INTERSECT",VERTEX,{"disambiguationData":[OD(1.0)],"derivedFrom":[subQ1,subQ0]});Q33=makeQuery(id+"F9.imprint","IMPRINT",FACE,{"disambiguationData":[TD([[makeQuery(id+"F9.imprint","IMPRINT",EDGE,{"disambiguationData":[TD([[subQ2,-1.0]])],"derivedFrom":subQ1}),-1.0]])]});}
            var Q34;
            {var subQ0=sQuery(id+"F9.wireOp",EDGE,"E17.0.0.8");var subQ1=sQuery(id+"F9.wireOp",EDGE,"E14.0.1.0");var subQ2=makeQuery(id+"F9.imprint","INTERSECT",VERTEX,{"disambiguationData":[OD(1.0)],"derivedFrom":[subQ1,subQ0]});Q34=makeQuery(id+"F9.imprint","IMPRINT",FACE,{"disambiguationData":[TD([[makeQuery(id+"F9.imprint","IMPRINT",EDGE,{"disambiguationData":[TD([[subQ2,-1.0]])],"derivedFrom":subQ1}),-1.0]])]});}
            var Q35;
            {var subQ0=sQuery(id+"F9.wireOp",EDGE,"E18.0.0.6");var subQ1=sQuery(id+"F9.wireOp",EDGE,"E14.0.1.0");var subQ2=makeQuery(id+"F9.imprint","INTERSECT",VERTEX,{"disambiguationData":[OD(1.0)],"derivedFrom":[subQ1,subQ0]});Q35=makeQuery(id+"F9.imprint","IMPRINT",FACE,{"disambiguationData":[TD([[makeQuery(id+"F9.imprint","IMPRINT",EDGE,{"disambiguationData":[TD([[subQ2,-1.0]])],"derivedFrom":subQ1}),-1.0]])]});}
            var Q36;
            {var subQ0=sQuery(id+"F9.wireOp",EDGE,"E17.0.0.7");var subQ1=sQuery(id+"F9.wireOp",EDGE,"E14.0.1.0");var subQ2=makeQuery(id+"F9.imprint","INTERSECT",VERTEX,{"disambiguationData":[OD(1.0)],"derivedFrom":[subQ1,subQ0]});Q36=makeQuery(id+"F9.imprint","IMPRINT",FACE,{"disambiguationData":[TD([[makeQuery(id+"F9.imprint","IMPRINT",EDGE,{"disambiguationData":[TD([[subQ2,-1.0]])],"derivedFrom":subQ1}),-1.0]])]});}
            var Q37;
            {var subQ0=sQuery(id+"F9.wireOp",EDGE,"E18.0.0.5");var subQ1=sQuery(id+"F9.wireOp",EDGE,"E14.0.1.0");var subQ2=makeQuery(id+"F9.imprint","INTERSECT",VERTEX,{"disambiguationData":[OD(1.0)],"derivedFrom":[subQ1,subQ0]});Q37=makeQuery(id+"F9.imprint","IMPRINT",FACE,{"disambiguationData":[TD([[makeQuery(id+"F9.imprint","IMPRINT",EDGE,{"disambiguationData":[TD([[subQ2,-1.0]])],"derivedFrom":subQ1}),-1.0]])]});}
            var Q38;
            {var subQ0=sQuery(id+"F9.wireOp",EDGE,"E17.0.0.6");var subQ1=sQuery(id+"F9.wireOp",EDGE,"E14.0.1.0");var subQ2=makeQuery(id+"F9.imprint","INTERSECT",VERTEX,{"disambiguationData":[OD(1.0)],"derivedFrom":[subQ1,subQ0]});Q38=makeQuery(id+"F9.imprint","IMPRINT",FACE,{"disambiguationData":[TD([[makeQuery(id+"F9.imprint","IMPRINT",EDGE,{"disambiguationData":[TD([[subQ2,-1.0]])],"derivedFrom":subQ1}),-1.0]])]});}
            var Q39;
            {var subQ1=sQuery(id+"F9.wireOp",EDGE,"E14.0.1.0");var subQ9=sQuery(id+"F9.wireOp",EDGE,"E15");var subQ10=makeQuery(id+"F9.imprint","INTERSECT",VERTEX,{"disambiguationData":[OD(1.0)],"derivedFrom":[subQ1,subQ9]});Q39=makeQuery(id+"F9.imprint","IMPRINT",FACE,{"disambiguationData":[TD([[makeQuery(id+"F9.imprint","IMPRINT",EDGE,{"disambiguationData":[TD([[subQ10,-1.0]])],"derivedFrom":subQ1}),-1.0]])]});}
            var Q40;
            {var subQ1=sQuery(id+"F9.wireOp",EDGE,"E14.0.2.0");var subQ7=sQuery(id+"F9.wireOp",EDGE,"E17.0.0.7");var subQ8=makeQuery(id+"F9.imprint","INTERSECT",VERTEX,{"disambiguationData":[OD(1.0)],"derivedFrom":[subQ1,subQ7]});Q40=makeQuery(id+"F9.imprint","IMPRINT",FACE,{"disambiguationData":[TD([[makeQuery(id+"F9.imprint","IMPRINT",EDGE,{"disambiguationData":[TD([[subQ8,-1.0]])],"derivedFrom":subQ1}),1.0]])]});}
            var Q41;
            {var subQ0=sQuery(id+"F9.wireOp",EDGE,"E18.0.0.6");var subQ1=sQuery(id+"F9.wireOp",EDGE,"E14.0.2.0");var subQ2=makeQuery(id+"F9.imprint","INTERSECT",VERTEX,{"disambiguationData":[OD(1.0)],"derivedFrom":[subQ1,subQ0]});Q41=makeQuery(id+"F9.imprint","IMPRINT",FACE,{"disambiguationData":[TD([[makeQuery(id+"F9.imprint","IMPRINT",EDGE,{"disambiguationData":[TD([[subQ2,-1.0]])],"derivedFrom":subQ1}),1.0]])]});}
            var Q42;
            {var subQ0=sQuery(id+"F9.wireOp",EDGE,"E17.0.0.8");var subQ1=sQuery(id+"F9.wireOp",EDGE,"E14.0.2.0");var subQ2=makeQuery(id+"F9.imprint","INTERSECT",VERTEX,{"disambiguationData":[OD(1.0)],"derivedFrom":[subQ1,subQ0]});Q42=makeQuery(id+"F9.imprint","IMPRINT",FACE,{"disambiguationData":[TD([[makeQuery(id+"F9.imprint","IMPRINT",EDGE,{"disambiguationData":[TD([[subQ2,-1.0]])],"derivedFrom":subQ1}),1.0]])]});}
            var Q43;
            {var subQ0=sQuery(id+"F9.wireOp",EDGE,"E17.0.0.8");var subQ1=sQuery(id+"F9.wireOp",EDGE,"E14.0.2.0");var subQ2=makeQuery(id+"F9.imprint","INTERSECT",VERTEX,{"disambiguationData":[OD(1.0)],"derivedFrom":[subQ1,subQ0]});Q43=makeQuery(id+"F9.imprint","IMPRINT",FACE,{"disambiguationData":[TD([[makeQuery(id+"F9.imprint","IMPRINT",EDGE,{"disambiguationData":[TD([[subQ2,-1.0]])],"derivedFrom":subQ1}),-1.0]])]});}
            var Q44;
            {var subQ5=sQuery(id+"F9.wireOp",EDGE,"E17.0.0.8");var subQ9=sQuery(id+"F9.wireOp",EDGE,"E14.0.3.0");var subQ11=makeQuery(id+"F9.imprint","INTERSECT",VERTEX,{"disambiguationData":[OD(1.0)],"derivedFrom":[subQ9,subQ5]});Q44=makeQuery(id+"F9.imprint","IMPRINT",FACE,{"disambiguationData":[TD([[makeQuery(id+"F9.imprint","IMPRINT",EDGE,{"disambiguationData":[TD([[subQ11,-1.0]])],"derivedFrom":subQ9}),1.0]])]});}
            var Q45;
            {var subQ0=sQuery(id+"F9.wireOp",EDGE,"E18.0.0.6");var subQ1=sQuery(id+"F9.wireOp",EDGE,"E14.0.2.0");var subQ2=makeQuery(id+"F9.imprint","INTERSECT",VERTEX,{"disambiguationData":[OD(1.0)],"derivedFrom":[subQ1,subQ0]});Q45=makeQuery(id+"F9.imprint","IMPRINT",FACE,{"disambiguationData":[TD([[makeQuery(id+"F9.imprint","IMPRINT",EDGE,{"disambiguationData":[TD([[subQ2,-1.0]])],"derivedFrom":subQ1}),-1.0]])]});}
            var Q46;
            {var subQ0=sQuery(id+"F9.wireOp",EDGE,"E18.0.0.6");var subQ1=sQuery(id+"F9.wireOp",EDGE,"E16.0.1.0");var subQ2=makeQuery(id+"F9.imprint","INTERSECT",VERTEX,{"disambiguationData":[OD(2.0)],"derivedFrom":[subQ1,subQ0]});Q46=makeQuery(id+"F9.imprint","IMPRINT",FACE,{"disambiguationData":[TD([[makeQuery(id+"F9.imprint","IMPRINT",EDGE,{"disambiguationData":[TD([[subQ2,-1.0]])],"derivedFrom":subQ1}),-1.0]])]});}
            var Q47;
            {var subQ0=sQuery(id+"F9.wireOp",EDGE,"E16.0.1.0");var subQ1=sQuery(id+"F9.wireOp",EDGE,"E14.0.2.0");var subQ2=makeQuery(id+"F9.imprint","INTERSECT",VERTEX,{"disambiguationData":[OD(1.0)],"derivedFrom":[subQ1,subQ0]});Q47=makeQuery(id+"F9.imprint","IMPRINT",FACE,{"disambiguationData":[TD([[makeQuery(id+"F9.imprint","IMPRINT",EDGE,{"disambiguationData":[TD([[subQ2,-1.0]])],"derivedFrom":subQ1}),-1.0]])]});}
            var Q48;
            {var subQ0=sQuery(id+"F9.wireOp",EDGE,"E17.0.0.7");var subQ1=sQuery(id+"F9.wireOp",EDGE,"E14.0.2.0");var subQ2=makeQuery(id+"F9.imprint","INTERSECT",VERTEX,{"disambiguationData":[OD(1.0)],"derivedFrom":[subQ1,subQ0]});Q48=makeQuery(id+"F9.imprint","IMPRINT",FACE,{"disambiguationData":[TD([[makeQuery(id+"F9.imprint","IMPRINT",EDGE,{"disambiguationData":[TD([[subQ2,-1.0]])],"derivedFrom":subQ1}),-1.0]])]});}
            var Q49;
            {var subQ0=sQuery(id+"F9.wireOp",EDGE,"E18.0.0.5");var subQ1=sQuery(id+"F9.wireOp",EDGE,"E15");var subQ2=makeQuery(id+"F9.imprint","INTERSECT",VERTEX,{"disambiguationData":[OD(2.0)],"derivedFrom":[subQ1,subQ0]});Q49=makeQuery(id+"F9.imprint","IMPRINT",FACE,{"disambiguationData":[TD([[makeQuery(id+"F9.imprint","IMPRINT",EDGE,{"disambiguationData":[TD([[subQ2,-1.0]])],"derivedFrom":subQ1}),-1.0]])]});}
            var Q50;
            {var subQ0=sQuery(id+"F9.wireOp",EDGE,"E18.0.0.5");var subQ1=sQuery(id+"F9.wireOp",EDGE,"E14.0.2.0");var subQ2=makeQuery(id+"F9.imprint","INTERSECT",VERTEX,{"disambiguationData":[OD(1.0)],"derivedFrom":[subQ1,subQ0]});Q50=makeQuery(id+"F9.imprint","IMPRINT",FACE,{"disambiguationData":[TD([[makeQuery(id+"F9.imprint","IMPRINT",EDGE,{"disambiguationData":[TD([[subQ2,-1.0]])],"derivedFrom":subQ1}),-1.0]])]});}
            var Q51;
            {var subQ0=sQuery(id+"F9.wireOp",EDGE,"E17.0.0.6");var subQ1=sQuery(id+"F9.wireOp",EDGE,"E14.0.2.0");var subQ2=makeQuery(id+"F9.imprint","INTERSECT",VERTEX,{"disambiguationData":[OD(1.0)],"derivedFrom":[subQ1,subQ0]});Q51=makeQuery(id+"F9.imprint","IMPRINT",FACE,{"disambiguationData":[TD([[makeQuery(id+"F9.imprint","IMPRINT",EDGE,{"disambiguationData":[TD([[subQ2,-1.0]])],"derivedFrom":subQ1}),-1.0]])]});}
            var Q52;
            {var subQ0=sQuery(id+"F9.wireOp",EDGE,"E18.0.0.5");var subQ1=sQuery(id+"F9.wireOp",EDGE,"E14.0.2.0");var subQ2=makeQuery(id+"F9.imprint","INTERSECT",VERTEX,{"disambiguationData":[OD(1.0)],"derivedFrom":[subQ1,subQ0]});Q52=makeQuery(id+"F9.imprint","IMPRINT",FACE,{"disambiguationData":[TD([[makeQuery(id+"F9.imprint","IMPRINT",EDGE,{"disambiguationData":[TD([[subQ2,-1.0]])],"derivedFrom":subQ1}),1.0]])]});}
            var Q53;
            {var subQ0=sQuery(id+"F9.wireOp",EDGE,"E18.0.0.5");var subQ1=sQuery(id+"F9.wireOp",EDGE,"E14.0.3.0");var subQ2=makeQuery(id+"F9.imprint","INTERSECT",VERTEX,{"disambiguationData":[OD(1.0)],"derivedFrom":[subQ1,subQ0]});Q53=makeQuery(id+"F9.imprint","IMPRINT",FACE,{"disambiguationData":[TD([[makeQuery(id+"F9.imprint","IMPRINT",EDGE,{"disambiguationData":[TD([[subQ2,-1.0]])],"derivedFrom":subQ1}),1.0]])]});}
            var Q54;
            {var subQ0=sQuery(id+"F9.wireOp",EDGE,"E17.0.0.6");var subQ1=sQuery(id+"F9.wireOp",EDGE,"E14.0.3.0");var subQ2=makeQuery(id+"F9.imprint","INTERSECT",VERTEX,{"disambiguationData":[OD(1.0)],"derivedFrom":[subQ1,subQ0]});Q54=makeQuery(id+"F9.imprint","IMPRINT",FACE,{"disambiguationData":[TD([[makeQuery(id+"F9.imprint","IMPRINT",EDGE,{"disambiguationData":[TD([[subQ2,-1.0]])],"derivedFrom":subQ1}),1.0]])]});}
            var Q55;
            {var subQ0=sQuery(id+"F9.wireOp",EDGE,"E18.0.0.6");var subQ1=sQuery(id+"F9.wireOp",EDGE,"E14.0.3.0");var subQ2=makeQuery(id+"F9.imprint","INTERSECT",VERTEX,{"disambiguationData":[OD(1.0)],"derivedFrom":[subQ1,subQ0]});Q55=makeQuery(id+"F9.imprint","IMPRINT",FACE,{"disambiguationData":[TD([[makeQuery(id+"F9.imprint","IMPRINT",EDGE,{"disambiguationData":[TD([[subQ2,-1.0]])],"derivedFrom":subQ1}),1.0]])]});}
            var Q56;
            {var subQ0=sQuery(id+"F9.wireOp",EDGE,"E17.0.0.6");var subQ1=sQuery(id+"F9.wireOp",EDGE,"E14.0.2.0");var subQ2=makeQuery(id+"F9.imprint","INTERSECT",VERTEX,{"disambiguationData":[OD(1.0)],"derivedFrom":[subQ1,subQ0]});Q56=makeQuery(id+"F9.imprint","IMPRINT",FACE,{"disambiguationData":[TD([[makeQuery(id+"F9.imprint","IMPRINT",EDGE,{"disambiguationData":[TD([[subQ2,-1.0]])],"derivedFrom":subQ1}),1.0]])]});}
            var Q57;
            {var subQ0=sQuery(id+"F9.wireOp",EDGE,"E16.0.1.0");var subQ1=sQuery(id+"F9.wireOp",EDGE,"E14.0.2.0");var subQ2=makeQuery(id+"F9.imprint","INTERSECT",VERTEX,{"disambiguationData":[OD(1.0)],"derivedFrom":[subQ1,subQ0]});Q57=makeQuery(id+"F9.imprint","IMPRINT",FACE,{"disambiguationData":[TD([[makeQuery(id+"F9.imprint","IMPRINT",EDGE,{"disambiguationData":[TD([[subQ2,-1.0]])],"derivedFrom":subQ1}),1.0]])]});}
            var Q58;
            {var subQ0=sQuery(id+"F9.wireOp",EDGE,"E17.0.0.6");var subQ1=sQuery(id+"F9.wireOp",EDGE,"E16.0.1.0");var subQ2=makeQuery(id+"F9.imprint","INTERSECT",VERTEX,{"disambiguationData":[OD(1.0)],"derivedFrom":[subQ1,subQ0]});Q58=makeQuery(id+"F9.imprint","IMPRINT",FACE,{"disambiguationData":[TD([[makeQuery(id+"F9.imprint","IMPRINT",EDGE,{"disambiguationData":[TD([[subQ2,-1.0]])],"derivedFrom":subQ1}),1.0]])]});}
            var Q59;
            {var subQ0=sQuery(id+"F9.wireOp",EDGE,"E17.0.0.7");var subQ1=sQuery(id+"F9.wireOp",EDGE,"E14.0.3.0");var subQ2=makeQuery(id+"F9.imprint","INTERSECT",VERTEX,{"disambiguationData":[OD(1.0)],"derivedFrom":[subQ1,subQ0]});Q59=makeQuery(id+"F9.imprint","IMPRINT",FACE,{"disambiguationData":[TD([[makeQuery(id+"F9.imprint","IMPRINT",EDGE,{"disambiguationData":[TD([[subQ2,-1.0]])],"derivedFrom":subQ1}),1.0]])]});}
            var Q60;
            {var subQ0=sQuery(id+"F9.wireOp",EDGE,"E16.0.2.0");var subQ1=sQuery(id+"F9.wireOp",EDGE,"E14.0.3.0");var subQ2=makeQuery(id+"F9.imprint","INTERSECT",VERTEX,{"disambiguationData":[OD(1.0)],"derivedFrom":[subQ1,subQ0]});Q60=makeQuery(id+"F9.imprint","IMPRINT",FACE,{"disambiguationData":[TD([[makeQuery(id+"F9.imprint","IMPRINT",EDGE,{"disambiguationData":[TD([[subQ2,-1.0]])],"derivedFrom":subQ1}),1.0]])]});}
            var Q61;
            {var subQ0=sQuery(id+"F9.wireOp",EDGE,"E17.0.0.7");var subQ1=sQuery(id+"F9.wireOp",EDGE,"E16.0.2.0");var subQ2=makeQuery(id+"F9.imprint","INTERSECT",VERTEX,{"disambiguationData":[OD(1.0)],"derivedFrom":[subQ1,subQ0]});Q61=makeQuery(id+"F9.imprint","IMPRINT",FACE,{"disambiguationData":[TD([[makeQuery(id+"F9.imprint","IMPRINT",EDGE,{"disambiguationData":[TD([[subQ2,-1.0]])],"derivedFrom":subQ1}),1.0]])]});}
            var Q62;
            {var subQ0=sQuery(id+"F9.wireOp",EDGE,"E18.0.0.6");var subQ1=sQuery(id+"F9.wireOp",EDGE,"E14.0.1.0");var subQ2=makeQuery(id+"F9.imprint","INTERSECT",VERTEX,{"disambiguationData":[OD(0.0)],"derivedFrom":[subQ1,subQ0]});Q62=makeQuery(id+"F9.imprint","IMPRINT",FACE,{"disambiguationData":[TD([[makeQuery(id+"F9.imprint","IMPRINT",EDGE,{"disambiguationData":[TD([[subQ2,-1.0]])],"derivedFrom":subQ1}),-1.0]])]});}
            var Q63;
            {var subQ0=sQuery(id+"F9.wireOp",EDGE,"E18.0.0.6");var subQ1=sQuery(id+"F9.wireOp",EDGE,"E14.0.2.0");var subQ2=makeQuery(id+"F9.imprint","INTERSECT",VERTEX,{"disambiguationData":[OD(0.0)],"derivedFrom":[subQ1,subQ0]});Q63=makeQuery(id+"F9.imprint","IMPRINT",FACE,{"disambiguationData":[TD([[makeQuery(id+"F9.imprint","IMPRINT",EDGE,{"disambiguationData":[TD([[subQ2,-1.0]])],"derivedFrom":subQ1}),1.0]])]});}
            var Q64;
            {var subQ0=sQuery(id+"F9.wireOp",EDGE,"E17.0.0.7");var subQ1=sQuery(id+"F9.wireOp",EDGE,"E14.0.2.0");var subQ2=makeQuery(id+"F9.imprint","INTERSECT",VERTEX,{"disambiguationData":[OD(0.0)],"derivedFrom":[subQ1,subQ0]});Q64=makeQuery(id+"F9.imprint","IMPRINT",FACE,{"disambiguationData":[TD([[makeQuery(id+"F9.imprint","IMPRINT",EDGE,{"disambiguationData":[TD([[subQ2,-1.0]])],"derivedFrom":subQ1}),1.0]])]});}
            var Q65;
            {var subQ1=sQuery(id+"F9.wireOp",EDGE,"E16.0.1.0");var subQ5=sQuery(id+"F9.wireOp",EDGE,"E14.0.2.0");var subQ6=makeQuery(id+"F9.imprint","INTERSECT",VERTEX,{"disambiguationData":[OD(0.0)],"derivedFrom":[subQ5,subQ1]});Q65=makeQuery(id+"F9.imprint","IMPRINT",FACE,{"disambiguationData":[TD([[makeQuery(id+"F9.imprint","IMPRINT",EDGE,{"disambiguationData":[TD([[subQ6,-1.0]])],"derivedFrom":subQ5}),1.0]])]});}
            var Q66;
            {var subQ0=sQuery(id+"F9.wireOp",EDGE,"E18.0.0.5");var subQ1=sQuery(id+"F9.wireOp",EDGE,"E14.0.1.0");var subQ2=makeQuery(id+"F9.imprint","INTERSECT",VERTEX,{"disambiguationData":[OD(0.0)],"derivedFrom":[subQ1,subQ0]});Q66=makeQuery(id+"F9.imprint","IMPRINT",FACE,{"disambiguationData":[TD([[makeQuery(id+"F9.imprint","IMPRINT",EDGE,{"disambiguationData":[TD([[subQ2,-1.0]])],"derivedFrom":subQ1}),-1.0]])]});}
            var Q67;
            {var subQ0=sQuery(id+"F9.wireOp",EDGE,"E17.0.0.6");var subQ1=sQuery(id+"F9.wireOp",EDGE,"E14.0.1.0");var subQ2=makeQuery(id+"F9.imprint","INTERSECT",VERTEX,{"disambiguationData":[OD(0.0)],"derivedFrom":[subQ1,subQ0]});Q67=makeQuery(id+"F9.imprint","IMPRINT",FACE,{"disambiguationData":[TD([[makeQuery(id+"F9.imprint","IMPRINT",EDGE,{"disambiguationData":[TD([[subQ2,-1.0]])],"derivedFrom":subQ1}),-1.0]])]});}
            var Q68;
            {var subQ0=sQuery(id+"F9.wireOp",EDGE,"E17.0.0.6");var subQ1=sQuery(id+"F9.wireOp",EDGE,"E15");var subQ2=makeQuery(id+"F9.imprint","INTERSECT",VERTEX,{"disambiguationData":[OD(0.0)],"derivedFrom":[subQ1,subQ0]});Q68=makeQuery(id+"F9.imprint","IMPRINT",FACE,{"disambiguationData":[TD([[makeQuery(id+"F9.imprint","IMPRINT",EDGE,{"disambiguationData":[TD([[subQ2,-1.0]])],"derivedFrom":subQ1}),-1.0]])]});}
            var Q69;
            {var subQ0=sQuery(id+"F9.wireOp",EDGE,"E17.0.0.5");var subQ1=sQuery(id+"F9.wireOp",EDGE,"E14.0.1.0");var subQ2=makeQuery(id+"F9.imprint","INTERSECT",VERTEX,{"disambiguationData":[OD(0.0)],"derivedFrom":[subQ1,subQ0]});Q69=makeQuery(id+"F9.imprint","IMPRINT",FACE,{"disambiguationData":[TD([[makeQuery(id+"F9.imprint","IMPRINT",EDGE,{"disambiguationData":[TD([[subQ2,-1.0]])],"derivedFrom":subQ1}),-1.0]])]});}
            var Q70;
            {var subQ0=sQuery(id+"F9.wireOp",EDGE,"E15");var subQ1=sQuery(id+"F9.wireOp",EDGE,"E14.0.1.0");var subQ2=makeQuery(id+"F9.imprint","INTERSECT",VERTEX,{"disambiguationData":[OD(0.0)],"derivedFrom":[subQ1,subQ0]});Q70=makeQuery(id+"F9.imprint","IMPRINT",FACE,{"disambiguationData":[TD([[makeQuery(id+"F9.imprint","IMPRINT",EDGE,{"disambiguationData":[TD([[subQ2,-1.0]])],"derivedFrom":subQ1}),-1.0]])]});}
            var Q71;
            {var subQ0=sQuery(id+"F9.wireOp",EDGE,"E17.0.0.7");var subQ1=sQuery(id+"F9.wireOp",EDGE,"E14.0.1.0");var subQ2=makeQuery(id+"F9.imprint","INTERSECT",VERTEX,{"disambiguationData":[OD(0.0)],"derivedFrom":[subQ1,subQ0]});Q71=makeQuery(id+"F9.imprint","IMPRINT",FACE,{"disambiguationData":[TD([[makeQuery(id+"F9.imprint","IMPRINT",EDGE,{"disambiguationData":[TD([[subQ2,-1.0]])],"derivedFrom":subQ1}),-1.0]])]});}
            var Q72;
            {var subQ1=sQuery(id+"F9.wireOp",EDGE,"E16.0.2.0");var subQ9=sQuery(id+"F9.wireOp",EDGE,"E14.0.3.0");var subQ10=makeQuery(id+"F9.imprint","INTERSECT",VERTEX,{"disambiguationData":[OD(0.0)],"derivedFrom":[subQ9,subQ1]});Q72=makeQuery(id+"F9.imprint","IMPRINT",FACE,{"disambiguationData":[TD([[makeQuery(id+"F9.imprint","IMPRINT",EDGE,{"disambiguationData":[TD([[subQ10,-1.0]])],"derivedFrom":subQ9}),1.0]])]});}
            var Q73;
            {var subQ0=sQuery(id+"F9.wireOp",EDGE,"E18.0.0.5");var subQ1=sQuery(id+"F9.wireOp",EDGE,"E14.0.3.0");var subQ2=makeQuery(id+"F9.imprint","INTERSECT",VERTEX,{"disambiguationData":[OD(0.0)],"derivedFrom":[subQ1,subQ0]});Q73=makeQuery(id+"F9.imprint","IMPRINT",FACE,{"disambiguationData":[TD([[makeQuery(id+"F9.imprint","IMPRINT",EDGE,{"disambiguationData":[TD([[subQ2,-1.0]])],"derivedFrom":subQ1}),1.0]])]});}
            var Q74;
            {var subQ0=sQuery(id+"F9.wireOp",EDGE,"E17.0.0.7");var subQ1=sQuery(id+"F9.wireOp",EDGE,"E14.0.2.0");var subQ2=makeQuery(id+"F9.imprint","INTERSECT",VERTEX,{"disambiguationData":[OD(0.0)],"derivedFrom":[subQ1,subQ0]});Q74=makeQuery(id+"F9.imprint","IMPRINT",FACE,{"disambiguationData":[TD([[makeQuery(id+"F9.imprint","IMPRINT",EDGE,{"disambiguationData":[TD([[subQ2,-1.0]])],"derivedFrom":subQ1}),-1.0]])]});}
            var Q75;
            {var subQ0=sQuery(id+"F9.wireOp",EDGE,"E17.0.0.6");var subQ1=sQuery(id+"F9.wireOp",EDGE,"E14.0.3.0");var subQ2=makeQuery(id+"F9.imprint","INTERSECT",VERTEX,{"disambiguationData":[OD(0.0)],"derivedFrom":[subQ1,subQ0]});Q75=makeQuery(id+"F9.imprint","IMPRINT",FACE,{"disambiguationData":[TD([[makeQuery(id+"F9.imprint","IMPRINT",EDGE,{"disambiguationData":[TD([[subQ2,-1.0]])],"derivedFrom":subQ1}),1.0]])]});}
            var Q76;
            {var subQ0=sQuery(id+"F9.wireOp",EDGE,"E18.0.0.6");var subQ1=sQuery(id+"F9.wireOp",EDGE,"E14.0.2.0");var subQ2=makeQuery(id+"F9.imprint","INTERSECT",VERTEX,{"disambiguationData":[OD(0.0)],"derivedFrom":[subQ1,subQ0]});Q76=makeQuery(id+"F9.imprint","IMPRINT",FACE,{"disambiguationData":[TD([[makeQuery(id+"F9.imprint","IMPRINT",EDGE,{"disambiguationData":[TD([[subQ2,-1.0]])],"derivedFrom":subQ1}),-1.0]])]});}
            var Q77;
            {var subQ0=sQuery(id+"F9.wireOp",EDGE,"E17.0.0.7");var subQ1=sQuery(id+"F9.wireOp",EDGE,"E16.0.1.0");var subQ2=makeQuery(id+"F9.imprint","INTERSECT",VERTEX,{"disambiguationData":[OD(0.0)],"derivedFrom":[subQ1,subQ0]});Q77=makeQuery(id+"F9.imprint","IMPRINT",FACE,{"disambiguationData":[TD([[makeQuery(id+"F9.imprint","IMPRINT",EDGE,{"disambiguationData":[TD([[subQ2,-1.0]])],"derivedFrom":subQ1}),-1.0]])]});}
            var Q78;
            {var subQ0=sQuery(id+"F9.wireOp",EDGE,"E18.0.0.5");var subQ1=sQuery(id+"F9.wireOp",EDGE,"E14.0.2.0");var subQ2=makeQuery(id+"F9.imprint","INTERSECT",VERTEX,{"disambiguationData":[OD(0.0)],"derivedFrom":[subQ1,subQ0]});Q78=makeQuery(id+"F9.imprint","IMPRINT",FACE,{"disambiguationData":[TD([[makeQuery(id+"F9.imprint","IMPRINT",EDGE,{"disambiguationData":[TD([[subQ2,-1.0]])],"derivedFrom":subQ1}),-1.0]])]});}
            var Q79;
            {var subQ0=sQuery(id+"F9.wireOp",EDGE,"E16.0.1.0");var subQ1=sQuery(id+"F9.wireOp",EDGE,"E14.0.2.0");var subQ2=makeQuery(id+"F9.imprint","INTERSECT",VERTEX,{"disambiguationData":[OD(0.0)],"derivedFrom":[subQ1,subQ0]});Q79=makeQuery(id+"F9.imprint","IMPRINT",FACE,{"disambiguationData":[TD([[makeQuery(id+"F9.imprint","IMPRINT",EDGE,{"disambiguationData":[TD([[subQ2,-1.0]])],"derivedFrom":subQ1}),-1.0]])]});}
            var Q80;
            {var subQ0=sQuery(id+"F9.wireOp",EDGE,"E17.0.0.6");var subQ1=sQuery(id+"F9.wireOp",EDGE,"E14.0.2.0");var subQ2=makeQuery(id+"F9.imprint","INTERSECT",VERTEX,{"disambiguationData":[OD(0.0)],"derivedFrom":[subQ1,subQ0]});Q80=makeQuery(id+"F9.imprint","IMPRINT",FACE,{"disambiguationData":[TD([[makeQuery(id+"F9.imprint","IMPRINT",EDGE,{"disambiguationData":[TD([[subQ2,-1.0]])],"derivedFrom":subQ1}),-1.0]])]});}
            var Q81;
            {var subQ0=sQuery(id+"F9.wireOp",EDGE,"E17.0.0.6");var subQ1=sQuery(id+"F9.wireOp",EDGE,"E14.0.3.0");var subQ2=makeQuery(id+"F9.imprint","INTERSECT",VERTEX,{"disambiguationData":[OD(0.0)],"derivedFrom":[subQ1,subQ0]});Q81=makeQuery(id+"F9.imprint","IMPRINT",FACE,{"disambiguationData":[TD([[makeQuery(id+"F9.imprint","IMPRINT",EDGE,{"disambiguationData":[TD([[subQ2,-1.0]])],"derivedFrom":subQ1}),-1.0]])]});}
            var Q82;
            {var subQ0=sQuery(id+"F9.wireOp",EDGE,"E17.0.0.5");var subQ1=sQuery(id+"F9.wireOp",EDGE,"E14.0.2.0");var subQ2=makeQuery(id+"F9.imprint","INTERSECT",VERTEX,{"disambiguationData":[OD(0.0)],"derivedFrom":[subQ1,subQ0]});Q82=makeQuery(id+"F9.imprint","IMPRINT",FACE,{"disambiguationData":[TD([[makeQuery(id+"F9.imprint","IMPRINT",EDGE,{"disambiguationData":[TD([[subQ2,-1.0]])],"derivedFrom":subQ1}),-1.0]])]});}
            var Q83;
            {var subQ0=sQuery(id+"F9.wireOp",EDGE,"E18.0.0.6");var subQ1=sQuery(id+"F9.wireOp",EDGE,"E16.0.2.0");var subQ2=makeQuery(id+"F9.imprint","INTERSECT",VERTEX,{"disambiguationData":[OD(0.0)],"derivedFrom":[subQ1,subQ0]});Q83=makeQuery(id+"F9.imprint","IMPRINT",FACE,{"disambiguationData":[TD([[makeQuery(id+"F9.imprint","IMPRINT",EDGE,{"disambiguationData":[TD([[subQ2,-1.0]])],"derivedFrom":subQ1}),1.0]])]});}
            var Q84;
            {var subQ0=sQuery(id+"F9.wireOp",EDGE,"E18.0.0.6");var subQ1=sQuery(id+"F9.wireOp",EDGE,"E14.0.3.0");var subQ2=makeQuery(id+"F9.imprint","INTERSECT",VERTEX,{"disambiguationData":[OD(0.0)],"derivedFrom":[subQ1,subQ0]});Q84=makeQuery(id+"F9.imprint","IMPRINT",FACE,{"disambiguationData":[TD([[makeQuery(id+"F9.imprint","IMPRINT",EDGE,{"disambiguationData":[TD([[subQ2,-1.0]])],"derivedFrom":subQ1}),1.0]])]});}
            var Q85;
            {var subQ0=sQuery(id+"F9.wireOp",EDGE,"E18.0.0.5");var subQ1=sQuery(id+"F9.wireOp",EDGE,"E14.0.3.0");var subQ2=makeQuery(id+"F9.imprint","INTERSECT",VERTEX,{"disambiguationData":[OD(0.0)],"derivedFrom":[subQ1,subQ0]});Q85=makeQuery(id+"F9.imprint","IMPRINT",FACE,{"disambiguationData":[TD([[makeQuery(id+"F9.imprint","IMPRINT",EDGE,{"disambiguationData":[TD([[subQ2,-1.0]])],"derivedFrom":subQ1}),-1.0]])]});}
            var Q86;
            {var subQ0=sQuery(id+"F9.wireOp",EDGE,"E17.0.0.5");var subQ1=sQuery(id+"F9.wireOp",EDGE,"E14.0.2.0");var subQ2=makeQuery(id+"F9.imprint","INTERSECT",VERTEX,{"disambiguationData":[OD(0.0)],"derivedFrom":[subQ1,subQ0]});Q86=makeQuery(id+"F9.imprint","IMPRINT",FACE,{"disambiguationData":[TD([[makeQuery(id+"F9.imprint","IMPRINT",EDGE,{"disambiguationData":[TD([[subQ2,-1.0]])],"derivedFrom":subQ1}),1.0]])]});}
            var Q87;
            {var subQ0=sQuery(id+"F9.wireOp",EDGE,"E17.0.0.6");var subQ1=sQuery(id+"F9.wireOp",EDGE,"E14.0.2.0");var subQ2=makeQuery(id+"F9.imprint","INTERSECT",VERTEX,{"disambiguationData":[OD(0.0)],"derivedFrom":[subQ1,subQ0]});Q87=makeQuery(id+"F9.imprint","IMPRINT",FACE,{"disambiguationData":[TD([[makeQuery(id+"F9.imprint","IMPRINT",EDGE,{"disambiguationData":[TD([[subQ2,-1.0]])],"derivedFrom":subQ1}),1.0]])]});}
            var Q88;
            {var subQ0=sQuery(id+"F9.wireOp",EDGE,"E18.0.0.5");var subQ1=sQuery(id+"F9.wireOp",EDGE,"E14.0.2.0");var subQ2=makeQuery(id+"F9.imprint","INTERSECT",VERTEX,{"disambiguationData":[OD(0.0)],"derivedFrom":[subQ1,subQ0]});Q88=makeQuery(id+"F9.imprint","IMPRINT",FACE,{"disambiguationData":[TD([[makeQuery(id+"F9.imprint","IMPRINT",EDGE,{"disambiguationData":[TD([[subQ2,-1.0]])],"derivedFrom":subQ1}),1.0]])]});}
            var Q89;
            {var subQ0=sQuery(id+"F9.wireOp",EDGE,"E17.0.0.5");var subQ1=sQuery(id+"F9.wireOp",EDGE,"E14.0.3.0");var subQ2=makeQuery(id+"F9.imprint","INTERSECT",VERTEX,{"disambiguationData":[OD(0.0)],"derivedFrom":[subQ1,subQ0]});Q89=makeQuery(id+"F9.imprint","IMPRINT",FACE,{"disambiguationData":[TD([[makeQuery(id+"F9.imprint","IMPRINT",EDGE,{"disambiguationData":[TD([[subQ2,-1.0]])],"derivedFrom":subQ1}),1.0]])]});}
            var Q90;
            {var subQ0=sQuery(id+"F9.wireOp",EDGE,"E18.0.0.5");var subQ1=sQuery(id+"F9.wireOp",EDGE,"E16.0.1.0");var subQ2=makeQuery(id+"F9.imprint","INTERSECT",VERTEX,{"disambiguationData":[OD(0.0)],"derivedFrom":[subQ1,subQ0]});Q90=makeQuery(id+"F9.imprint","IMPRINT",FACE,{"disambiguationData":[TD([[makeQuery(id+"F9.imprint","IMPRINT",EDGE,{"disambiguationData":[TD([[subQ2,-1.0]])],"derivedFrom":subQ1}),1.0]])]});}
            var Q91;
            {var subQ0=sQuery(id+"F9.wireOp",EDGE,"E18.0.0.6");var subQ1=sQuery(id+"F9.wireOp",EDGE,"E14.0.3.0");var subQ2=makeQuery(id+"F9.imprint","INTERSECT",VERTEX,{"disambiguationData":[OD(0.0)],"derivedFrom":[subQ1,subQ0]});Q91=makeQuery(id+"F9.imprint","IMPRINT",FACE,{"disambiguationData":[TD([[makeQuery(id+"F9.imprint","IMPRINT",EDGE,{"disambiguationData":[TD([[subQ2,-1.0]])],"derivedFrom":subQ1}),-1.0]])]});}
            var Q92;
            {var subQ0=sQuery(id+"F9.wireOp",EDGE,"E17.0.0.7");var subQ1=sQuery(id+"F9.wireOp",EDGE,"E14.0.3.0");var subQ2=makeQuery(id+"F9.imprint","INTERSECT",VERTEX,{"disambiguationData":[OD(0.0)],"derivedFrom":[subQ1,subQ0]});Q92=makeQuery(id+"F9.imprint","IMPRINT",FACE,{"disambiguationData":[TD([[makeQuery(id+"F9.imprint","IMPRINT",EDGE,{"disambiguationData":[TD([[subQ2,-1.0]])],"derivedFrom":subQ1}),1.0]])]});}
            var Q93;
            {var subQ0=sQuery(id+"F9.wireOp",EDGE,"E17.0.0.7");var subQ1=sQuery(id+"F9.wireOp",EDGE,"E14.0.3.0");var subQ2=makeQuery(id+"F9.imprint","INTERSECT",VERTEX,{"disambiguationData":[OD(0.0)],"derivedFrom":[subQ1,subQ0]});Q93=makeQuery(id+"F9.imprint","IMPRINT",FACE,{"disambiguationData":[TD([[makeQuery(id+"F9.imprint","IMPRINT",EDGE,{"disambiguationData":[TD([[subQ2,-1.0]])],"derivedFrom":subQ1}),-1.0]])]});}
            var Q94;
            {var subQ0=sQuery(id+"F9.wireOp",EDGE,"E16.0.2.0");var subQ1=sQuery(id+"F9.wireOp",EDGE,"E14.0.3.0");var subQ2=makeQuery(id+"F9.imprint","INTERSECT",VERTEX,{"disambiguationData":[OD(0.0)],"derivedFrom":[subQ1,subQ0]});Q94=makeQuery(id+"F9.imprint","IMPRINT",FACE,{"disambiguationData":[TD([[makeQuery(id+"F9.imprint","IMPRINT",EDGE,{"disambiguationData":[TD([[subQ2,-1.0]])],"derivedFrom":subQ1}),-1.0]])]});}
            var Q95;
            {var subQ0=sQuery(id+"F9.wireOp",EDGE,"E17.0.0.5");var subQ1=sQuery(id+"F9.wireOp",EDGE,"E14.0.3.0");var subQ2=makeQuery(id+"F9.imprint","INTERSECT",VERTEX,{"disambiguationData":[OD(0.0)],"derivedFrom":[subQ1,subQ0]});Q95=makeQuery(id+"F9.imprint","IMPRINT",FACE,{"disambiguationData":[TD([[makeQuery(id+"F9.imprint","IMPRINT",EDGE,{"disambiguationData":[TD([[subQ2,-1.0]])],"derivedFrom":subQ1}),-1.0]])]});}
            var Q96;
            {var subQ0=sQuery(id+"F9.wireOp",EDGE,"E17.0.0.8");var subQ1=makeQuery(id+"F9.imprint","INTERSECT",VERTEX,{"disambiguationData":[OD(2.0)],"derivedFrom":[sQuery(id+"F9.wireOp",EDGE,"E14.0.3.0"),subQ0]});Q96=makeQuery(id+"F9.imprint","IMPRINT",FACE,{"disambiguationData":[TD([[makeQuery(id+"F9.imprint","IMPRINT",EDGE,{"disambiguationData":[TD([[subQ1,1.0]])],"derivedFrom":subQ0}),1.0]])]});}
            var Q97;
            {var subQ5=sQuery(id+"F9.wireOp",EDGE,"E17.0.0.7");var subQ7=sQuery(id+"F9.wireOp",EDGE,"E13");var subQ8=makeQuery(id+"F9.imprint","INTERSECT",VERTEX,{"disambiguationData":[OD(0.0)],"derivedFrom":[subQ7,subQ5]});Q97=makeQuery(id+"F9.imprint","IMPRINT",FACE,{"disambiguationData":[TD([[makeQuery(id+"F9.imprint","IMPRINT",EDGE,{"disambiguationData":[TD([[subQ8,-1.0]])],"derivedFrom":subQ7}),1.0]])]});}
            extrude(context, id + "F13", {"entities" : qUnion([Q0, Q1, Q2, Q3, Q4, Q5, Q6, Q7, Q8, Q9, Q10, Q11, Q12, Q13, Q14, Q15, Q16, Q17, Q18, Q19, Q20, Q21, Q22, Q23, Q24, Q25, Q26, Q27, Q28, Q29, Q30, Q31, Q32, Q33, Q34, Q35, Q36, Q37, Q38, Q39, Q40, Q41, Q42, Q43, Q44, Q45, Q46, Q47, Q48, Q49, Q50, Q51, Q52, Q53, Q54, Q55, Q56, Q57, Q58, Q59, Q60, Q61, Q62, Q63, Q64, Q65, Q66, Q67, Q68, Q69, Q70, Q71, Q72, Q73, Q74, Q75, Q76, Q77, Q78, Q79, Q80, Q81, Q82, Q83, Q84, Q85, Q86, Q87, Q88, Q89, Q90, Q91, Q92, Q93, Q94, Q95, Q96, Q97]), "endBound" : BoundingType.SYMMETRIC, "depth" : 2133.6 * mm});
        }
        {
            var Q0;
            {var subQ0=sQuery(id+"F9.wireOp",EDGE,"E19");Q0=makeQuery(id+"F9.imprint","IMPRINT",FACE,{"disambiguationData":[TD([[makeQuery(id+"F9.imprint","IMPRINT",EDGE,{"derivedFrom":subQ0}),1.0]])]});}
            var Q1;
            {var subQ0=sQuery(id+"F9.wireOp",EDGE,"E18.0.0.4");var subQ1=sQuery(id+"F9.wireOp",EDGE,"E17.0.0.8");var subQ2=makeQuery(id+"F9.imprint","INTERSECT",VERTEX,{"disambiguationData":[OD(2.0)],"derivedFrom":[subQ1,subQ0]});Q1=makeQuery(id+"F9.imprint","IMPRINT",FACE,{"disambiguationData":[TD([[makeQuery(id+"F9.imprint","IMPRINT",EDGE,{"disambiguationData":[TD([[subQ2,-1.0]])],"derivedFrom":subQ1}),1.0]])]});}
            var Q2;
            {var subQ0=sQuery(id+"F9.wireOp",EDGE,"E18.0.0.5");var subQ1=sQuery(id+"F9.wireOp",EDGE,"E17.0.0.8");var subQ2=makeQuery(id+"F9.imprint","INTERSECT",VERTEX,{"disambiguationData":[OD(2.0)],"derivedFrom":[subQ1,subQ0]});Q2=makeQuery(id+"F9.imprint","IMPRINT",FACE,{"disambiguationData":[TD([[makeQuery(id+"F9.imprint","IMPRINT",EDGE,{"disambiguationData":[TD([[subQ2,-1.0]])],"derivedFrom":subQ1}),1.0]])]});}
            var Q3;
            {var subQ0=sQuery(id+"F9.wireOp",EDGE,"E17.0.0.8");var subQ1=sQuery(id+"F9.wireOp",EDGE,"E13");var subQ2=makeQuery(id+"F9.imprint","INTERSECT",VERTEX,{"disambiguationData":[OD(0.0)],"derivedFrom":[subQ1,subQ0]});Q3=makeQuery(id+"F9.imprint","IMPRINT",FACE,{"disambiguationData":[TD([[makeQuery(id+"F9.imprint","IMPRINT",EDGE,{"disambiguationData":[TD([[subQ2,-1.0]])],"derivedFrom":subQ1}),1.0]])]});}
            var Q4;
            {var subQ0=sQuery(id+"F9.wireOp",EDGE,"E17.0.0.8");var subQ1=sQuery(id+"F9.wireOp",EDGE,"E13");var subQ2=makeQuery(id+"F9.imprint","INTERSECT",VERTEX,{"disambiguationData":[OD(0.0)],"derivedFrom":[subQ1,subQ0]});Q4=makeQuery(id+"F9.imprint","IMPRINT",FACE,{"disambiguationData":[TD([[makeQuery(id+"F9.imprint","IMPRINT",EDGE,{"disambiguationData":[TD([[subQ2,-1.0]])],"derivedFrom":subQ1}),-1.0]])]});}
            var Q5;
            {var subQ0=sQuery(id+"F9.wireOp",EDGE,"E18.0.0.7");var subQ1=sQuery(id+"F9.wireOp",EDGE,"E14.0.1.0");var subQ2=makeQuery(id+"F9.imprint","INTERSECT",VERTEX,{"disambiguationData":[OD(0.0)],"derivedFrom":[subQ1,subQ0]});Q5=makeQuery(id+"F9.imprint","IMPRINT",FACE,{"disambiguationData":[TD([[makeQuery(id+"F9.imprint","IMPRINT",EDGE,{"disambiguationData":[TD([[subQ2,-1.0]])],"derivedFrom":subQ1}),1.0]])]});}
            var Q6;
            {var subQ0=sQuery(id+"F9.wireOp",EDGE,"E18.0.0.7");var subQ1=sQuery(id+"F9.wireOp",EDGE,"E14.0.1.0");var subQ2=makeQuery(id+"F9.imprint","INTERSECT",VERTEX,{"disambiguationData":[OD(0.0)],"derivedFrom":[subQ1,subQ0]});Q6=makeQuery(id+"F9.imprint","IMPRINT",FACE,{"disambiguationData":[TD([[makeQuery(id+"F9.imprint","IMPRINT",EDGE,{"disambiguationData":[TD([[subQ2,-1.0]])],"derivedFrom":subQ1}),-1.0]])]});}
            var Q7;
            {var subQ0=sQuery(id+"F9.wireOp",EDGE,"E17.0.0.8");var subQ1=sQuery(id+"F9.wireOp",EDGE,"E14.0.1.0");var subQ2=makeQuery(id+"F9.imprint","INTERSECT",VERTEX,{"disambiguationData":[OD(0.0)],"derivedFrom":[subQ1,subQ0]});Q7=makeQuery(id+"F9.imprint","IMPRINT",FACE,{"disambiguationData":[TD([[makeQuery(id+"F9.imprint","IMPRINT",EDGE,{"disambiguationData":[TD([[subQ2,-1.0]])],"derivedFrom":subQ1}),-1.0]])]});}
            var Q8;
            {var subQ0=sQuery(id+"F9.wireOp",EDGE,"E17.0.0.8");var subQ1=sQuery(id+"F9.wireOp",EDGE,"E14.0.2.0");var subQ2=makeQuery(id+"F9.imprint","INTERSECT",VERTEX,{"disambiguationData":[OD(0.0)],"derivedFrom":[subQ1,subQ0]});Q8=makeQuery(id+"F9.imprint","IMPRINT",FACE,{"disambiguationData":[TD([[makeQuery(id+"F9.imprint","IMPRINT",EDGE,{"disambiguationData":[TD([[subQ2,-1.0]])],"derivedFrom":subQ1}),1.0]])]});}
            var Q9;
            {var subQ0=sQuery(id+"F9.wireOp",EDGE,"E18.0.0.7");var subQ1=sQuery(id+"F9.wireOp",EDGE,"E14.0.2.0");var subQ2=makeQuery(id+"F9.imprint","INTERSECT",VERTEX,{"disambiguationData":[OD(0.0)],"derivedFrom":[subQ1,subQ0]});Q9=makeQuery(id+"F9.imprint","IMPRINT",FACE,{"disambiguationData":[TD([[makeQuery(id+"F9.imprint","IMPRINT",EDGE,{"disambiguationData":[TD([[subQ2,-1.0]])],"derivedFrom":subQ1}),1.0]])]});}
            var Q10;
            {var subQ0=sQuery(id+"F9.wireOp",EDGE,"E18.0.0.7");var subQ1=sQuery(id+"F9.wireOp",EDGE,"E14.0.2.0");var subQ2=makeQuery(id+"F9.imprint","INTERSECT",VERTEX,{"disambiguationData":[OD(0.0)],"derivedFrom":[subQ1,subQ0]});Q10=makeQuery(id+"F9.imprint","IMPRINT",FACE,{"disambiguationData":[TD([[makeQuery(id+"F9.imprint","IMPRINT",EDGE,{"disambiguationData":[TD([[subQ2,-1.0]])],"derivedFrom":subQ1}),-1.0]])]});}
            var Q11;
            {var subQ0=sQuery(id+"F9.wireOp",EDGE,"E17.0.0.8");var subQ1=sQuery(id+"F9.wireOp",EDGE,"E14.0.2.0");var subQ2=makeQuery(id+"F9.imprint","INTERSECT",VERTEX,{"disambiguationData":[OD(0.0)],"derivedFrom":[subQ1,subQ0]});Q11=makeQuery(id+"F9.imprint","IMPRINT",FACE,{"disambiguationData":[TD([[makeQuery(id+"F9.imprint","IMPRINT",EDGE,{"disambiguationData":[TD([[subQ2,-1.0]])],"derivedFrom":subQ1}),-1.0]])]});}
            var Q12;
            {var subQ0=sQuery(id+"F9.wireOp",EDGE,"E17.0.0.8");var subQ1=sQuery(id+"F9.wireOp",EDGE,"E14.0.3.0");var subQ2=makeQuery(id+"F9.imprint","INTERSECT",VERTEX,{"disambiguationData":[OD(0.0)],"derivedFrom":[subQ1,subQ0]});Q12=makeQuery(id+"F9.imprint","IMPRINT",FACE,{"disambiguationData":[TD([[makeQuery(id+"F9.imprint","IMPRINT",EDGE,{"disambiguationData":[TD([[subQ2,-1.0]])],"derivedFrom":subQ1}),1.0]])]});}
            var Q13;
            {var subQ0=sQuery(id+"F9.wireOp",EDGE,"E18.0.0.7");var subQ1=sQuery(id+"F9.wireOp",EDGE,"E14.0.3.0");var subQ2=makeQuery(id+"F9.imprint","INTERSECT",VERTEX,{"disambiguationData":[OD(0.0)],"derivedFrom":[subQ1,subQ0]});Q13=makeQuery(id+"F9.imprint","IMPRINT",FACE,{"disambiguationData":[TD([[makeQuery(id+"F9.imprint","IMPRINT",EDGE,{"disambiguationData":[TD([[subQ2,-1.0]])],"derivedFrom":subQ1}),1.0]])]});}
            var Q14;
            {var subQ0=sQuery(id+"F9.wireOp",EDGE,"E17.0.0.8");var subQ1=sQuery(id+"F9.wireOp",EDGE,"E14.0.3.0");var subQ2=makeQuery(id+"F9.imprint","INTERSECT",VERTEX,{"disambiguationData":[OD(0.0)],"derivedFrom":[subQ1,subQ0]});Q14=makeQuery(id+"F9.imprint","IMPRINT",FACE,{"disambiguationData":[TD([[makeQuery(id+"F9.imprint","IMPRINT",EDGE,{"disambiguationData":[TD([[subQ2,-1.0]])],"derivedFrom":subQ1}),-1.0]])]});}
            var Q15;
            {var subQ0=sQuery(id+"F9.wireOp",EDGE,"E18.0.0.7");var subQ1=sQuery(id+"F9.wireOp",EDGE,"E14.0.3.0");var subQ2=makeQuery(id+"F9.imprint","INTERSECT",VERTEX,{"disambiguationData":[OD(0.0)],"derivedFrom":[subQ1,subQ0]});Q15=makeQuery(id+"F9.imprint","IMPRINT",FACE,{"disambiguationData":[TD([[makeQuery(id+"F9.imprint","IMPRINT",EDGE,{"disambiguationData":[TD([[subQ2,-1.0]])],"derivedFrom":subQ1}),-1.0]])]});}
            var Q16;
            {var subQ1=sQuery(id+"F9.wireOp",EDGE,"E16.0.2.0");var subQ9=sQuery(id+"F9.wireOp",EDGE,"E18.0.0.7");var subQ11=makeQuery(id+"F9.imprint","INTERSECT",VERTEX,{"disambiguationData":[OD(0.0)],"derivedFrom":[subQ1,subQ9]});Q16=makeQuery(id+"F9.imprint","IMPRINT",FACE,{"disambiguationData":[TD([[makeQuery(id+"F9.imprint","IMPRINT",EDGE,{"disambiguationData":[TD([[subQ11,-1.0]])],"derivedFrom":subQ1}),-1.0]])]});}
            var Q17;
            {var subQ0=sQuery(id+"F9.wireOp",EDGE,"E18.0.0.4");var subQ1=sQuery(id+"F9.wireOp",EDGE,"E16.0.3.0");var subQ2=makeQuery(id+"F9.imprint","INTERSECT",VERTEX,{"disambiguationData":[OD(1.0)],"derivedFrom":[subQ1,subQ0]});Q17=makeQuery(id+"F9.imprint","IMPRINT",FACE,{"disambiguationData":[TD([[makeQuery(id+"F9.imprint","IMPRINT",EDGE,{"disambiguationData":[TD([[subQ2,-1.0]])],"derivedFrom":subQ1}),1.0]])]});}
            var Q18;
            {var subQ1=sQuery(id+"F9.wireOp",EDGE,"E16.0.3.0");var subQ8=sQuery(id+"F9.wireOp",EDGE,"E18.0.0.4");var subQ11=makeQuery(id+"F9.imprint","INTERSECT",VERTEX,{"disambiguationData":[OD(1.0)],"derivedFrom":[subQ1,subQ8]});Q18=makeQuery(id+"F9.imprint","IMPRINT",FACE,{"disambiguationData":[TD([[makeQuery(id+"F9.imprint","IMPRINT",EDGE,{"disambiguationData":[TD([[subQ11,-1.0]])],"derivedFrom":subQ1}),-1.0]])]});}
            var Q19;
            {var subQ0=sQuery(id+"F9.wireOp",EDGE,"E17.0.0.8");var subQ1=sQuery(id+"F9.wireOp",EDGE,"E16.0.2.0");var subQ2=makeQuery(id+"F9.imprint","INTERSECT",VERTEX,{"disambiguationData":[OD(0.0)],"derivedFrom":[subQ1,subQ0]});Q19=makeQuery(id+"F9.imprint","IMPRINT",FACE,{"disambiguationData":[TD([[makeQuery(id+"F9.imprint","IMPRINT",EDGE,{"disambiguationData":[TD([[subQ2,-1.0]])],"derivedFrom":subQ1}),-1.0]])]});}
            var Q20;
            {var subQ0=sQuery(id+"F9.wireOp",EDGE,"E17.0.0.8");var subQ1=sQuery(id+"F9.wireOp",EDGE,"E16.0.3.0");var subQ2=makeQuery(id+"F9.imprint","INTERSECT",VERTEX,{"disambiguationData":[OD(0.0)],"derivedFrom":[subQ1,subQ0]});Q20=makeQuery(id+"F9.imprint","IMPRINT",FACE,{"disambiguationData":[TD([[makeQuery(id+"F9.imprint","IMPRINT",EDGE,{"disambiguationData":[TD([[subQ2,-1.0]])],"derivedFrom":subQ1}),-1.0]])]});}
            var Q21;
            {var subQ0=sQuery(id+"F9.wireOp",EDGE,"E17.0.0.8");var subQ1=sQuery(id+"F9.wireOp",EDGE,"E17.0.0.4");var subQ2=makeQuery(id+"F9.imprint","INTERSECT",VERTEX,{"disambiguationData":[OD(0.0)],"derivedFrom":[subQ1,subQ0]});Q21=makeQuery(id+"F9.imprint","IMPRINT",FACE,{"disambiguationData":[TD([[makeQuery(id+"F9.imprint","IMPRINT",EDGE,{"disambiguationData":[TD([[subQ2,-1.0]])],"derivedFrom":subQ1}),-1.0]])]});}
            extrude(context, id + "F14", {"entities" : qUnion([Q0, Q1, Q2, Q3, Q4, Q5, Q6, Q7, Q8, Q9, Q10, Q11, Q12, Q13, Q14, Q15, Q16, Q17, Q18, Q19, Q20, Q21]), "depth" : 25.4 * mm});
        }
        {
            var Q0;
            {var subQ0=sQuery(id+"F9.wireOp",EDGE,"E17.0.0.8");var subQ1=makeQuery(id+"F9.imprint","INTERSECT",VERTEX,{"disambiguationData":[OD(2.0)],"derivedFrom":[sQuery(id+"F9.wireOp",EDGE,"E14.0.3.0"),subQ0]});Q0=makeQuery(id+"F9.imprint","IMPRINT",FACE,{"disambiguationData":[TD([[makeQuery(id+"F9.imprint","IMPRINT",EDGE,{"disambiguationData":[TD([[subQ1,1.0]])],"derivedFrom":subQ0}),1.0]])]});}
            var Q1;
            {var subQ0=sQuery(id+"F9.wireOp",EDGE,"E17.0.0.8");var subQ1=sQuery(id+"F9.wireOp",EDGE,"E14.0.3.0");var subQ2=makeQuery(id+"F9.imprint","INTERSECT",VERTEX,{"disambiguationData":[OD(2.0)],"derivedFrom":[subQ1,subQ0]});Q1=makeQuery(id+"F9.imprint","IMPRINT",FACE,{"disambiguationData":[TD([[makeQuery(id+"F9.imprint","IMPRINT",EDGE,{"disambiguationData":[TD([[subQ2,-1.0]])],"derivedFrom":subQ1}),1.0]])]});}
            var Q2;
            {var subQ0=sQuery(id+"F9.wireOp",EDGE,"E17.0.0.7");var subQ1=sQuery(id+"F9.wireOp",EDGE,"E14.0.3.0");var subQ2=makeQuery(id+"F9.imprint","INTERSECT",VERTEX,{"disambiguationData":[OD(3.0)],"derivedFrom":[subQ1,subQ0]});Q2=makeQuery(id+"F9.imprint","IMPRINT",FACE,{"disambiguationData":[TD([[makeQuery(id+"F9.imprint","IMPRINT",EDGE,{"disambiguationData":[TD([[subQ2,-1.0]])],"derivedFrom":subQ1}),1.0]])]});}
            var Q3;
            {var subQ0=sQuery(id+"F9.wireOp",EDGE,"E18.0.0.4");var subQ1=sQuery(id+"F9.wireOp",EDGE,"E17.0.0.7");var subQ2=makeQuery(id+"F9.imprint","INTERSECT",VERTEX,{"disambiguationData":[OD(2.0)],"derivedFrom":[subQ1,subQ0]});Q3=makeQuery(id+"F9.imprint","IMPRINT",FACE,{"disambiguationData":[TD([[makeQuery(id+"F9.imprint","IMPRINT",EDGE,{"disambiguationData":[TD([[subQ2,-1.0]])],"derivedFrom":subQ1}),1.0]])]});}
            var Q4;
            {var subQ5=sQuery(id+"F9.wireOp",EDGE,"E17.0.0.6");var subQ7=sQuery(id+"F9.wireOp",EDGE,"E13");var subQ9=makeQuery(id+"F9.imprint","INTERSECT",VERTEX,{"disambiguationData":[OD(0.0)],"derivedFrom":[subQ7,subQ5]});Q4=makeQuery(id+"F9.imprint","IMPRINT",FACE,{"disambiguationData":[TD([[makeQuery(id+"F9.imprint","IMPRINT",EDGE,{"disambiguationData":[TD([[subQ9,-1.0]])],"derivedFrom":subQ7}),1.0]])]});}
            var Q5;
            {var subQ5=sQuery(id+"F9.wireOp",EDGE,"E17.0.0.7");var subQ7=sQuery(id+"F9.wireOp",EDGE,"E13");var subQ8=makeQuery(id+"F9.imprint","INTERSECT",VERTEX,{"disambiguationData":[OD(0.0)],"derivedFrom":[subQ7,subQ5]});Q5=makeQuery(id+"F9.imprint","IMPRINT",FACE,{"disambiguationData":[TD([[makeQuery(id+"F9.imprint","IMPRINT",EDGE,{"disambiguationData":[TD([[subQ8,-1.0]])],"derivedFrom":subQ7}),1.0]])]});}
            var Q6;
            {var subQ0=sQuery(id+"F9.wireOp",EDGE,"E17.0.0.7");var subQ1=sQuery(id+"F9.wireOp",EDGE,"E14.0.3.0");var subQ2=makeQuery(id+"F9.imprint","INTERSECT",VERTEX,{"disambiguationData":[OD(2.0)],"derivedFrom":[subQ1,subQ0]});Q6=makeQuery(id+"F9.imprint","IMPRINT",FACE,{"disambiguationData":[TD([[makeQuery(id+"F9.imprint","IMPRINT",EDGE,{"disambiguationData":[TD([[subQ2,-1.0]])],"derivedFrom":subQ1}),1.0]])]});}
            var Q7;
            {var subQ0=sQuery(id+"F9.wireOp",EDGE,"E18.0.0.5");var subQ1=sQuery(id+"F9.wireOp",EDGE,"E17.0.0.8");var subQ2=makeQuery(id+"F9.imprint","INTERSECT",VERTEX,{"disambiguationData":[OD(1.0)],"derivedFrom":[subQ1,subQ0]});Q7=makeQuery(id+"F9.imprint","IMPRINT",FACE,{"disambiguationData":[TD([[makeQuery(id+"F9.imprint","IMPRINT",EDGE,{"disambiguationData":[TD([[subQ2,-1.0]])],"derivedFrom":subQ1}),1.0]])]});}
            var Q8;
            {var subQ0=sQuery(id+"F9.wireOp",EDGE,"E18.0.0.5");var subQ1=sQuery(id+"F9.wireOp",EDGE,"E13");var subQ2=makeQuery(id+"F9.imprint","INTERSECT",VERTEX,{"disambiguationData":[OD(0.0)],"derivedFrom":[subQ1,subQ0]});Q8=makeQuery(id+"F9.imprint","IMPRINT",FACE,{"disambiguationData":[TD([[makeQuery(id+"F9.imprint","IMPRINT",EDGE,{"disambiguationData":[TD([[subQ2,-1.0]])],"derivedFrom":subQ1}),1.0]])]});}
            var Q9;
            {var subQ0=sQuery(id+"F9.wireOp",EDGE,"E18.0.0.5");var subQ1=sQuery(id+"F9.wireOp",EDGE,"E13");var subQ2=makeQuery(id+"F9.imprint","INTERSECT",VERTEX,{"disambiguationData":[OD(0.0)],"derivedFrom":[subQ1,subQ0]});Q9=makeQuery(id+"F9.imprint","IMPRINT",FACE,{"disambiguationData":[TD([[makeQuery(id+"F9.imprint","IMPRINT",EDGE,{"disambiguationData":[TD([[subQ2,-1.0]])],"derivedFrom":subQ1}),-1.0]])]});}
            var Q10;
            {var subQ0=sQuery(id+"F9.wireOp",EDGE,"E17.0.0.6");var subQ1=sQuery(id+"F9.wireOp",EDGE,"E13");var subQ2=makeQuery(id+"F9.imprint","INTERSECT",VERTEX,{"disambiguationData":[OD(0.0)],"derivedFrom":[subQ1,subQ0]});Q10=makeQuery(id+"F9.imprint","IMPRINT",FACE,{"disambiguationData":[TD([[makeQuery(id+"F9.imprint","IMPRINT",EDGE,{"disambiguationData":[TD([[subQ2,-1.0]])],"derivedFrom":subQ1}),-1.0]])]});}
            var Q11;
            {var subQ0=sQuery(id+"F9.wireOp",EDGE,"E17.0.0.7");var subQ1=sQuery(id+"F9.wireOp",EDGE,"E13");var subQ2=makeQuery(id+"F9.imprint","INTERSECT",VERTEX,{"disambiguationData":[OD(0.0)],"derivedFrom":[subQ1,subQ0]});Q11=makeQuery(id+"F9.imprint","IMPRINT",FACE,{"disambiguationData":[TD([[makeQuery(id+"F9.imprint","IMPRINT",EDGE,{"disambiguationData":[TD([[subQ2,-1.0]])],"derivedFrom":subQ1}),-1.0]])]});}
            var Q12;
            {var subQ0=sQuery(id+"F9.wireOp",EDGE,"E18.0.0.6");var subQ1=sQuery(id+"F9.wireOp",EDGE,"E13");var subQ2=makeQuery(id+"F9.imprint","INTERSECT",VERTEX,{"disambiguationData":[OD(0.0)],"derivedFrom":[subQ1,subQ0]});Q12=makeQuery(id+"F9.imprint","IMPRINT",FACE,{"disambiguationData":[TD([[makeQuery(id+"F9.imprint","IMPRINT",EDGE,{"disambiguationData":[TD([[subQ2,-1.0]])],"derivedFrom":subQ1}),-1.0]])]});}
            var Q13;
            {var subQ0=sQuery(id+"F9.wireOp",EDGE,"E18.0.0.6");var subQ1=sQuery(id+"F9.wireOp",EDGE,"E13");var subQ2=makeQuery(id+"F9.imprint","INTERSECT",VERTEX,{"disambiguationData":[OD(0.0)],"derivedFrom":[subQ1,subQ0]});Q13=makeQuery(id+"F9.imprint","IMPRINT",FACE,{"disambiguationData":[TD([[makeQuery(id+"F9.imprint","IMPRINT",EDGE,{"disambiguationData":[TD([[subQ2,-1.0]])],"derivedFrom":subQ1}),1.0]])]});}
            var Q14;
            {var subQ0=sQuery(id+"F9.wireOp",EDGE,"E18.0.0.6");var subQ1=sQuery(id+"F9.wireOp",EDGE,"E14.0.1.0");var subQ2=makeQuery(id+"F9.imprint","INTERSECT",VERTEX,{"disambiguationData":[OD(0.0)],"derivedFrom":[subQ1,subQ0]});Q14=makeQuery(id+"F9.imprint","IMPRINT",FACE,{"disambiguationData":[TD([[makeQuery(id+"F9.imprint","IMPRINT",EDGE,{"disambiguationData":[TD([[subQ2,-1.0]])],"derivedFrom":subQ1}),-1.0]])]});}
            var Q15;
            {var subQ0=sQuery(id+"F9.wireOp",EDGE,"E17.0.0.7");var subQ1=sQuery(id+"F9.wireOp",EDGE,"E14.0.1.0");var subQ2=makeQuery(id+"F9.imprint","INTERSECT",VERTEX,{"disambiguationData":[OD(0.0)],"derivedFrom":[subQ1,subQ0]});Q15=makeQuery(id+"F9.imprint","IMPRINT",FACE,{"disambiguationData":[TD([[makeQuery(id+"F9.imprint","IMPRINT",EDGE,{"disambiguationData":[TD([[subQ2,-1.0]])],"derivedFrom":subQ1}),-1.0]])]});}
            var Q16;
            {var subQ0=sQuery(id+"F9.wireOp",EDGE,"E18.0.0.5");var subQ1=sQuery(id+"F9.wireOp",EDGE,"E14.0.1.0");var subQ2=makeQuery(id+"F9.imprint","INTERSECT",VERTEX,{"disambiguationData":[OD(0.0)],"derivedFrom":[subQ1,subQ0]});Q16=makeQuery(id+"F9.imprint","IMPRINT",FACE,{"disambiguationData":[TD([[makeQuery(id+"F9.imprint","IMPRINT",EDGE,{"disambiguationData":[TD([[subQ2,-1.0]])],"derivedFrom":subQ1}),-1.0]])]});}
            var Q17;
            {var subQ0=sQuery(id+"F9.wireOp",EDGE,"E17.0.0.6");var subQ1=sQuery(id+"F9.wireOp",EDGE,"E14.0.1.0");var subQ2=makeQuery(id+"F9.imprint","INTERSECT",VERTEX,{"disambiguationData":[OD(0.0)],"derivedFrom":[subQ1,subQ0]});Q17=makeQuery(id+"F9.imprint","IMPRINT",FACE,{"disambiguationData":[TD([[makeQuery(id+"F9.imprint","IMPRINT",EDGE,{"disambiguationData":[TD([[subQ2,-1.0]])],"derivedFrom":subQ1}),-1.0]])]});}
            var Q18;
            {var subQ0=sQuery(id+"F9.wireOp",EDGE,"E17.0.0.6");var subQ1=sQuery(id+"F9.wireOp",EDGE,"E15");var subQ2=makeQuery(id+"F9.imprint","INTERSECT",VERTEX,{"disambiguationData":[OD(0.0)],"derivedFrom":[subQ1,subQ0]});Q18=makeQuery(id+"F9.imprint","IMPRINT",FACE,{"disambiguationData":[TD([[makeQuery(id+"F9.imprint","IMPRINT",EDGE,{"disambiguationData":[TD([[subQ2,-1.0]])],"derivedFrom":subQ1}),-1.0]])]});}
            var Q19;
            {var subQ1=sQuery(id+"F9.wireOp",EDGE,"E16.0.1.0");var subQ5=sQuery(id+"F9.wireOp",EDGE,"E14.0.2.0");var subQ6=makeQuery(id+"F9.imprint","INTERSECT",VERTEX,{"disambiguationData":[OD(0.0)],"derivedFrom":[subQ5,subQ1]});Q19=makeQuery(id+"F9.imprint","IMPRINT",FACE,{"disambiguationData":[TD([[makeQuery(id+"F9.imprint","IMPRINT",EDGE,{"disambiguationData":[TD([[subQ6,-1.0]])],"derivedFrom":subQ5}),1.0]])]});}
            var Q20;
            {var subQ0=sQuery(id+"F9.wireOp",EDGE,"E17.0.0.7");var subQ1=sQuery(id+"F9.wireOp",EDGE,"E14.0.2.0");var subQ2=makeQuery(id+"F9.imprint","INTERSECT",VERTEX,{"disambiguationData":[OD(0.0)],"derivedFrom":[subQ1,subQ0]});Q20=makeQuery(id+"F9.imprint","IMPRINT",FACE,{"disambiguationData":[TD([[makeQuery(id+"F9.imprint","IMPRINT",EDGE,{"disambiguationData":[TD([[subQ2,-1.0]])],"derivedFrom":subQ1}),1.0]])]});}
            var Q21;
            {var subQ0=sQuery(id+"F9.wireOp",EDGE,"E18.0.0.6");var subQ1=sQuery(id+"F9.wireOp",EDGE,"E14.0.2.0");var subQ2=makeQuery(id+"F9.imprint","INTERSECT",VERTEX,{"disambiguationData":[OD(0.0)],"derivedFrom":[subQ1,subQ0]});Q21=makeQuery(id+"F9.imprint","IMPRINT",FACE,{"disambiguationData":[TD([[makeQuery(id+"F9.imprint","IMPRINT",EDGE,{"disambiguationData":[TD([[subQ2,-1.0]])],"derivedFrom":subQ1}),1.0]])]});}
            var Q22;
            {var subQ0=sQuery(id+"F9.wireOp",EDGE,"E17.0.0.6");var subQ1=sQuery(id+"F9.wireOp",EDGE,"E14.0.2.0");var subQ2=makeQuery(id+"F9.imprint","INTERSECT",VERTEX,{"disambiguationData":[OD(0.0)],"derivedFrom":[subQ1,subQ0]});Q22=makeQuery(id+"F9.imprint","IMPRINT",FACE,{"disambiguationData":[TD([[makeQuery(id+"F9.imprint","IMPRINT",EDGE,{"disambiguationData":[TD([[subQ2,-1.0]])],"derivedFrom":subQ1}),-1.0]])]});}
            var Q23;
            {var subQ0=sQuery(id+"F9.wireOp",EDGE,"E17.0.0.7");var subQ1=sQuery(id+"F9.wireOp",EDGE,"E16.0.1.0");var subQ2=makeQuery(id+"F9.imprint","INTERSECT",VERTEX,{"disambiguationData":[OD(0.0)],"derivedFrom":[subQ1,subQ0]});Q23=makeQuery(id+"F9.imprint","IMPRINT",FACE,{"disambiguationData":[TD([[makeQuery(id+"F9.imprint","IMPRINT",EDGE,{"disambiguationData":[TD([[subQ2,-1.0]])],"derivedFrom":subQ1}),-1.0]])]});}
            var Q24;
            {var subQ1=sQuery(id+"F9.wireOp",EDGE,"E16.0.2.0");var subQ9=sQuery(id+"F9.wireOp",EDGE,"E14.0.3.0");var subQ10=makeQuery(id+"F9.imprint","INTERSECT",VERTEX,{"disambiguationData":[OD(0.0)],"derivedFrom":[subQ9,subQ1]});Q24=makeQuery(id+"F9.imprint","IMPRINT",FACE,{"disambiguationData":[TD([[makeQuery(id+"F9.imprint","IMPRINT",EDGE,{"disambiguationData":[TD([[subQ10,-1.0]])],"derivedFrom":subQ9}),1.0]])]});}
            var Q25;
            {var subQ0=sQuery(id+"F9.wireOp",EDGE,"E18.0.0.6");var subQ1=sQuery(id+"F9.wireOp",EDGE,"E14.0.2.0");var subQ2=makeQuery(id+"F9.imprint","INTERSECT",VERTEX,{"disambiguationData":[OD(0.0)],"derivedFrom":[subQ1,subQ0]});Q25=makeQuery(id+"F9.imprint","IMPRINT",FACE,{"disambiguationData":[TD([[makeQuery(id+"F9.imprint","IMPRINT",EDGE,{"disambiguationData":[TD([[subQ2,-1.0]])],"derivedFrom":subQ1}),-1.0]])]});}
            var Q26;
            {var subQ0=sQuery(id+"F9.wireOp",EDGE,"E17.0.0.7");var subQ1=sQuery(id+"F9.wireOp",EDGE,"E14.0.2.0");var subQ2=makeQuery(id+"F9.imprint","INTERSECT",VERTEX,{"disambiguationData":[OD(0.0)],"derivedFrom":[subQ1,subQ0]});Q26=makeQuery(id+"F9.imprint","IMPRINT",FACE,{"disambiguationData":[TD([[makeQuery(id+"F9.imprint","IMPRINT",EDGE,{"disambiguationData":[TD([[subQ2,-1.0]])],"derivedFrom":subQ1}),-1.0]])]});}
            var Q27;
            {var subQ0=sQuery(id+"F9.wireOp",EDGE,"E16.0.1.0");var subQ1=sQuery(id+"F9.wireOp",EDGE,"E14.0.2.0");var subQ2=makeQuery(id+"F9.imprint","INTERSECT",VERTEX,{"disambiguationData":[OD(0.0)],"derivedFrom":[subQ1,subQ0]});Q27=makeQuery(id+"F9.imprint","IMPRINT",FACE,{"disambiguationData":[TD([[makeQuery(id+"F9.imprint","IMPRINT",EDGE,{"disambiguationData":[TD([[subQ2,-1.0]])],"derivedFrom":subQ1}),-1.0]])]});}
            var Q28;
            {var subQ0=sQuery(id+"F9.wireOp",EDGE,"E17.0.0.6");var subQ1=sQuery(id+"F9.wireOp",EDGE,"E14.0.2.0");var subQ2=makeQuery(id+"F9.imprint","INTERSECT",VERTEX,{"disambiguationData":[OD(0.0)],"derivedFrom":[subQ1,subQ0]});Q28=makeQuery(id+"F9.imprint","IMPRINT",FACE,{"disambiguationData":[TD([[makeQuery(id+"F9.imprint","IMPRINT",EDGE,{"disambiguationData":[TD([[subQ2,-1.0]])],"derivedFrom":subQ1}),1.0]])]});}
            var Q29;
            {var subQ0=sQuery(id+"F9.wireOp",EDGE,"E17.0.0.6");var subQ1=sQuery(id+"F9.wireOp",EDGE,"E14.0.3.0");var subQ2=makeQuery(id+"F9.imprint","INTERSECT",VERTEX,{"disambiguationData":[OD(0.0)],"derivedFrom":[subQ1,subQ0]});Q29=makeQuery(id+"F9.imprint","IMPRINT",FACE,{"disambiguationData":[TD([[makeQuery(id+"F9.imprint","IMPRINT",EDGE,{"disambiguationData":[TD([[subQ2,-1.0]])],"derivedFrom":subQ1}),1.0]])]});}
            var Q30;
            {var subQ0=sQuery(id+"F9.wireOp",EDGE,"E17.0.0.6");var subQ1=sQuery(id+"F9.wireOp",EDGE,"E14.0.3.0");var subQ2=makeQuery(id+"F9.imprint","INTERSECT",VERTEX,{"disambiguationData":[OD(0.0)],"derivedFrom":[subQ1,subQ0]});Q30=makeQuery(id+"F9.imprint","IMPRINT",FACE,{"disambiguationData":[TD([[makeQuery(id+"F9.imprint","IMPRINT",EDGE,{"disambiguationData":[TD([[subQ2,-1.0]])],"derivedFrom":subQ1}),-1.0]])]});}
            var Q31;
            {var subQ0=sQuery(id+"F9.wireOp",EDGE,"E16.0.2.0");var subQ1=sQuery(id+"F9.wireOp",EDGE,"E14.0.3.0");var subQ2=makeQuery(id+"F9.imprint","INTERSECT",VERTEX,{"disambiguationData":[OD(0.0)],"derivedFrom":[subQ1,subQ0]});Q31=makeQuery(id+"F9.imprint","IMPRINT",FACE,{"disambiguationData":[TD([[makeQuery(id+"F9.imprint","IMPRINT",EDGE,{"disambiguationData":[TD([[subQ2,-1.0]])],"derivedFrom":subQ1}),-1.0]])]});}
            var Q32;
            {var subQ0=sQuery(id+"F9.wireOp",EDGE,"E17.0.0.7");var subQ1=sQuery(id+"F9.wireOp",EDGE,"E14.0.3.0");var subQ2=makeQuery(id+"F9.imprint","INTERSECT",VERTEX,{"disambiguationData":[OD(0.0)],"derivedFrom":[subQ1,subQ0]});Q32=makeQuery(id+"F9.imprint","IMPRINT",FACE,{"disambiguationData":[TD([[makeQuery(id+"F9.imprint","IMPRINT",EDGE,{"disambiguationData":[TD([[subQ2,-1.0]])],"derivedFrom":subQ1}),-1.0]])]});}
            var Q33;
            {var subQ0=sQuery(id+"F9.wireOp",EDGE,"E18.0.0.6");var subQ1=sQuery(id+"F9.wireOp",EDGE,"E14.0.3.0");var subQ2=makeQuery(id+"F9.imprint","INTERSECT",VERTEX,{"disambiguationData":[OD(0.0)],"derivedFrom":[subQ1,subQ0]});Q33=makeQuery(id+"F9.imprint","IMPRINT",FACE,{"disambiguationData":[TD([[makeQuery(id+"F9.imprint","IMPRINT",EDGE,{"disambiguationData":[TD([[subQ2,-1.0]])],"derivedFrom":subQ1}),-1.0]])]});}
            var Q34;
            {var subQ0=sQuery(id+"F9.wireOp",EDGE,"E18.0.0.6");var subQ1=sQuery(id+"F9.wireOp",EDGE,"E14.0.3.0");var subQ2=makeQuery(id+"F9.imprint","INTERSECT",VERTEX,{"disambiguationData":[OD(0.0)],"derivedFrom":[subQ1,subQ0]});Q34=makeQuery(id+"F9.imprint","IMPRINT",FACE,{"disambiguationData":[TD([[makeQuery(id+"F9.imprint","IMPRINT",EDGE,{"disambiguationData":[TD([[subQ2,-1.0]])],"derivedFrom":subQ1}),1.0]])]});}
            var Q35;
            {var subQ0=sQuery(id+"F9.wireOp",EDGE,"E18.0.0.6");var subQ1=sQuery(id+"F9.wireOp",EDGE,"E16.0.2.0");var subQ2=makeQuery(id+"F9.imprint","INTERSECT",VERTEX,{"disambiguationData":[OD(0.0)],"derivedFrom":[subQ1,subQ0]});Q35=makeQuery(id+"F9.imprint","IMPRINT",FACE,{"disambiguationData":[TD([[makeQuery(id+"F9.imprint","IMPRINT",EDGE,{"disambiguationData":[TD([[subQ2,-1.0]])],"derivedFrom":subQ1}),1.0]])]});}
            var Q36;
            {var subQ0=sQuery(id+"F9.wireOp",EDGE,"E17.0.0.7");var subQ1=sQuery(id+"F9.wireOp",EDGE,"E14.0.3.0");var subQ2=makeQuery(id+"F9.imprint","INTERSECT",VERTEX,{"disambiguationData":[OD(0.0)],"derivedFrom":[subQ1,subQ0]});Q36=makeQuery(id+"F9.imprint","IMPRINT",FACE,{"disambiguationData":[TD([[makeQuery(id+"F9.imprint","IMPRINT",EDGE,{"disambiguationData":[TD([[subQ2,-1.0]])],"derivedFrom":subQ1}),1.0]])]});}
            var Q37;
            {var subQ0=sQuery(id+"F9.wireOp",EDGE,"E18.0.0.5");var subQ1=sQuery(id+"F9.wireOp",EDGE,"E17.0.0.7");var subQ2=makeQuery(id+"F9.imprint","INTERSECT",VERTEX,{"disambiguationData":[OD(1.0)],"derivedFrom":[subQ1,subQ0]});Q37=makeQuery(id+"F9.imprint","IMPRINT",FACE,{"disambiguationData":[TD([[makeQuery(id+"F9.imprint","IMPRINT",EDGE,{"disambiguationData":[TD([[subQ2,-1.0]])],"derivedFrom":subQ1}),1.0]])]});}
            var Q38;
            {var subQ0=sQuery(id+"F9.wireOp",EDGE,"E18.0.0.6");var subQ1=sQuery(id+"F9.wireOp",EDGE,"E17.0.0.8");var subQ2=makeQuery(id+"F9.imprint","INTERSECT",VERTEX,{"disambiguationData":[OD(1.0)],"derivedFrom":[subQ1,subQ0]});Q38=makeQuery(id+"F9.imprint","IMPRINT",FACE,{"disambiguationData":[TD([[makeQuery(id+"F9.imprint","IMPRINT",EDGE,{"disambiguationData":[TD([[subQ2,-1.0]])],"derivedFrom":subQ1}),1.0]])]});}
            var Q39;
            {var subQ5=sQuery(id+"F9.wireOp",EDGE,"E13");var subQ7=sQuery(id+"F9.wireOp",EDGE,"E18.0.0.6");var subQ9=makeQuery(id+"F9.imprint","INTERSECT",VERTEX,{"disambiguationData":[OD(1.0)],"derivedFrom":[subQ5,subQ7]});Q39=makeQuery(id+"F9.imprint","IMPRINT",FACE,{"disambiguationData":[TD([[makeQuery(id+"F9.imprint","IMPRINT",EDGE,{"disambiguationData":[TD([[subQ9,-1.0]])],"derivedFrom":subQ5}),1.0]])]});}
            var Q40;
            {var subQ0=sQuery(id+"F9.wireOp",EDGE,"E17.0.0.9");var subQ1=sQuery(id+"F9.wireOp",EDGE,"E13");var subQ2=makeQuery(id+"F9.imprint","INTERSECT",VERTEX,{"disambiguationData":[OD(1.0)],"derivedFrom":[subQ1,subQ0]});Q40=makeQuery(id+"F9.imprint","IMPRINT",FACE,{"disambiguationData":[TD([[makeQuery(id+"F9.imprint","IMPRINT",EDGE,{"disambiguationData":[TD([[subQ2,-1.0]])],"derivedFrom":subQ1}),1.0]])]});}
            var Q41;
            {var subQ0=sQuery(id+"F9.wireOp",EDGE,"E17.0.0.9");var subQ1=sQuery(id+"F9.wireOp",EDGE,"E13");var subQ2=makeQuery(id+"F9.imprint","INTERSECT",VERTEX,{"disambiguationData":[OD(1.0)],"derivedFrom":[subQ1,subQ0]});Q41=makeQuery(id+"F9.imprint","IMPRINT",FACE,{"disambiguationData":[TD([[makeQuery(id+"F9.imprint","IMPRINT",EDGE,{"disambiguationData":[TD([[subQ2,-1.0]])],"derivedFrom":subQ1}),-1.0]])]});}
            var Q42;
            {var subQ0=sQuery(id+"F9.wireOp",EDGE,"E18.0.0.6");var subQ1=sQuery(id+"F9.wireOp",EDGE,"E13");var subQ2=makeQuery(id+"F9.imprint","INTERSECT",VERTEX,{"disambiguationData":[OD(1.0)],"derivedFrom":[subQ1,subQ0]});Q42=makeQuery(id+"F9.imprint","IMPRINT",FACE,{"disambiguationData":[TD([[makeQuery(id+"F9.imprint","IMPRINT",EDGE,{"disambiguationData":[TD([[subQ2,-1.0]])],"derivedFrom":subQ1}),-1.0]])]});}
            var Q43;
            {var subQ0=sQuery(id+"F9.wireOp",EDGE,"E17.0.0.8");var subQ1=sQuery(id+"F9.wireOp",EDGE,"E13");var subQ2=makeQuery(id+"F9.imprint","INTERSECT",VERTEX,{"disambiguationData":[OD(1.0)],"derivedFrom":[subQ1,subQ0]});Q43=makeQuery(id+"F9.imprint","IMPRINT",FACE,{"disambiguationData":[TD([[makeQuery(id+"F9.imprint","IMPRINT",EDGE,{"disambiguationData":[TD([[subQ2,-1.0]])],"derivedFrom":subQ1}),-1.0]])]});}
            var Q44;
            {var subQ0=sQuery(id+"F9.wireOp",EDGE,"E17.0.0.8");var subQ1=sQuery(id+"F9.wireOp",EDGE,"E13");var subQ2=makeQuery(id+"F9.imprint","INTERSECT",VERTEX,{"disambiguationData":[OD(1.0)],"derivedFrom":[subQ1,subQ0]});Q44=makeQuery(id+"F9.imprint","IMPRINT",FACE,{"disambiguationData":[TD([[makeQuery(id+"F9.imprint","IMPRINT",EDGE,{"disambiguationData":[TD([[subQ2,-1.0]])],"derivedFrom":subQ1}),1.0]])]});}
            var Q45;
            {var subQ0=sQuery(id+"F9.wireOp",EDGE,"E18.0.0.6");var subQ1=sQuery(id+"F9.wireOp",EDGE,"E14.0.1.0");var subQ2=makeQuery(id+"F9.imprint","INTERSECT",VERTEX,{"disambiguationData":[OD(1.0)],"derivedFrom":[subQ1,subQ0]});Q45=makeQuery(id+"F9.imprint","IMPRINT",FACE,{"disambiguationData":[TD([[makeQuery(id+"F9.imprint","IMPRINT",EDGE,{"disambiguationData":[TD([[subQ2,-1.0]])],"derivedFrom":subQ1}),-1.0]])]});}
            var Q46;
            {var subQ0=sQuery(id+"F9.wireOp",EDGE,"E17.0.0.8");var subQ1=sQuery(id+"F9.wireOp",EDGE,"E14.0.1.0");var subQ2=makeQuery(id+"F9.imprint","INTERSECT",VERTEX,{"disambiguationData":[OD(1.0)],"derivedFrom":[subQ1,subQ0]});Q46=makeQuery(id+"F9.imprint","IMPRINT",FACE,{"disambiguationData":[TD([[makeQuery(id+"F9.imprint","IMPRINT",EDGE,{"disambiguationData":[TD([[subQ2,-1.0]])],"derivedFrom":subQ1}),-1.0]])]});}
            var Q47;
            {var subQ0=sQuery(id+"F9.wireOp",EDGE,"E18.0.0.7");var subQ1=sQuery(id+"F9.wireOp",EDGE,"E14.0.1.0");var subQ2=makeQuery(id+"F9.imprint","INTERSECT",VERTEX,{"disambiguationData":[OD(1.0)],"derivedFrom":[subQ1,subQ0]});Q47=makeQuery(id+"F9.imprint","IMPRINT",FACE,{"disambiguationData":[TD([[makeQuery(id+"F9.imprint","IMPRINT",EDGE,{"disambiguationData":[TD([[subQ2,-1.0]])],"derivedFrom":subQ1}),-1.0]])]});}
            var Q48;
            {var subQ0=sQuery(id+"F9.wireOp",EDGE,"E17.0.0.9");var subQ1=sQuery(id+"F9.wireOp",EDGE,"E14.0.1.0");var subQ2=makeQuery(id+"F9.imprint","INTERSECT",VERTEX,{"disambiguationData":[OD(1.0)],"derivedFrom":[subQ1,subQ0]});Q48=makeQuery(id+"F9.imprint","IMPRINT",FACE,{"disambiguationData":[TD([[makeQuery(id+"F9.imprint","IMPRINT",EDGE,{"disambiguationData":[TD([[subQ2,-1.0]])],"derivedFrom":subQ1}),1.0]])]});}
            var Q49;
            {var subQ0=sQuery(id+"F9.wireOp",EDGE,"E17.0.0.9");var subQ1=sQuery(id+"F9.wireOp",EDGE,"E14.0.1.0");var subQ2=makeQuery(id+"F9.imprint","INTERSECT",VERTEX,{"disambiguationData":[OD(1.0)],"derivedFrom":[subQ1,subQ0]});Q49=makeQuery(id+"F9.imprint","IMPRINT",FACE,{"disambiguationData":[TD([[makeQuery(id+"F9.imprint","IMPRINT",EDGE,{"disambiguationData":[TD([[subQ2,-1.0]])],"derivedFrom":subQ1}),-1.0]])]});}
            var Q50;
            {var subQ0=sQuery(id+"F9.wireOp",EDGE,"E17.0.0.9");var subQ1=sQuery(id+"F9.wireOp",EDGE,"E14.0.2.0");var subQ2=makeQuery(id+"F9.imprint","INTERSECT",VERTEX,{"disambiguationData":[OD(1.0)],"derivedFrom":[subQ1,subQ0]});Q50=makeQuery(id+"F9.imprint","IMPRINT",FACE,{"disambiguationData":[TD([[makeQuery(id+"F9.imprint","IMPRINT",EDGE,{"disambiguationData":[TD([[subQ2,-1.0]])],"derivedFrom":subQ1}),1.0]])]});}
            var Q51;
            {var subQ0=sQuery(id+"F9.wireOp",EDGE,"E18.0.0.7");var subQ1=sQuery(id+"F9.wireOp",EDGE,"E14.0.2.0");var subQ2=makeQuery(id+"F9.imprint","INTERSECT",VERTEX,{"disambiguationData":[OD(1.0)],"derivedFrom":[subQ1,subQ0]});Q51=makeQuery(id+"F9.imprint","IMPRINT",FACE,{"disambiguationData":[TD([[makeQuery(id+"F9.imprint","IMPRINT",EDGE,{"disambiguationData":[TD([[subQ2,-1.0]])],"derivedFrom":subQ1}),1.0]])]});}
            var Q52;
            {var subQ0=sQuery(id+"F9.wireOp",EDGE,"E17.0.0.8");var subQ1=sQuery(id+"F9.wireOp",EDGE,"E14.0.2.0");var subQ2=makeQuery(id+"F9.imprint","INTERSECT",VERTEX,{"disambiguationData":[OD(1.0)],"derivedFrom":[subQ1,subQ0]});Q52=makeQuery(id+"F9.imprint","IMPRINT",FACE,{"disambiguationData":[TD([[makeQuery(id+"F9.imprint","IMPRINT",EDGE,{"disambiguationData":[TD([[subQ2,-1.0]])],"derivedFrom":subQ1}),1.0]])]});}
            var Q53;
            {var subQ0=sQuery(id+"F9.wireOp",EDGE,"E18.0.0.6");var subQ1=sQuery(id+"F9.wireOp",EDGE,"E14.0.2.0");var subQ2=makeQuery(id+"F9.imprint","INTERSECT",VERTEX,{"disambiguationData":[OD(1.0)],"derivedFrom":[subQ1,subQ0]});Q53=makeQuery(id+"F9.imprint","IMPRINT",FACE,{"disambiguationData":[TD([[makeQuery(id+"F9.imprint","IMPRINT",EDGE,{"disambiguationData":[TD([[subQ2,-1.0]])],"derivedFrom":subQ1}),1.0]])]});}
            var Q54;
            {var subQ0=sQuery(id+"F9.wireOp",EDGE,"E18.0.0.6");var subQ1=sQuery(id+"F9.wireOp",EDGE,"E14.0.2.0");var subQ2=makeQuery(id+"F9.imprint","INTERSECT",VERTEX,{"disambiguationData":[OD(1.0)],"derivedFrom":[subQ1,subQ0]});Q54=makeQuery(id+"F9.imprint","IMPRINT",FACE,{"disambiguationData":[TD([[makeQuery(id+"F9.imprint","IMPRINT",EDGE,{"disambiguationData":[TD([[subQ2,-1.0]])],"derivedFrom":subQ1}),-1.0]])]});}
            var Q55;
            {var subQ0=sQuery(id+"F9.wireOp",EDGE,"E17.0.0.8");var subQ1=sQuery(id+"F9.wireOp",EDGE,"E14.0.2.0");var subQ2=makeQuery(id+"F9.imprint","INTERSECT",VERTEX,{"disambiguationData":[OD(1.0)],"derivedFrom":[subQ1,subQ0]});Q55=makeQuery(id+"F9.imprint","IMPRINT",FACE,{"disambiguationData":[TD([[makeQuery(id+"F9.imprint","IMPRINT",EDGE,{"disambiguationData":[TD([[subQ2,-1.0]])],"derivedFrom":subQ1}),-1.0]])]});}
            var Q56;
            {var subQ0=sQuery(id+"F9.wireOp",EDGE,"E18.0.0.7");var subQ1=sQuery(id+"F9.wireOp",EDGE,"E14.0.2.0");var subQ2=makeQuery(id+"F9.imprint","INTERSECT",VERTEX,{"disambiguationData":[OD(1.0)],"derivedFrom":[subQ1,subQ0]});Q56=makeQuery(id+"F9.imprint","IMPRINT",FACE,{"disambiguationData":[TD([[makeQuery(id+"F9.imprint","IMPRINT",EDGE,{"disambiguationData":[TD([[subQ2,-1.0]])],"derivedFrom":subQ1}),-1.0]])]});}
            var Q57;
            {var subQ0=sQuery(id+"F9.wireOp",EDGE,"E17.0.0.9");var subQ1=sQuery(id+"F9.wireOp",EDGE,"E14.0.2.0");var subQ2=makeQuery(id+"F9.imprint","INTERSECT",VERTEX,{"disambiguationData":[OD(1.0)],"derivedFrom":[subQ1,subQ0]});Q57=makeQuery(id+"F9.imprint","IMPRINT",FACE,{"disambiguationData":[TD([[makeQuery(id+"F9.imprint","IMPRINT",EDGE,{"disambiguationData":[TD([[subQ2,-1.0]])],"derivedFrom":subQ1}),-1.0]])]});}
            var Q58;
            {var subQ0=sQuery(id+"F9.wireOp",EDGE,"E17.0.0.9");var subQ1=sQuery(id+"F9.wireOp",EDGE,"E14.0.3.0");var subQ2=makeQuery(id+"F9.imprint","INTERSECT",VERTEX,{"disambiguationData":[OD(1.0)],"derivedFrom":[subQ1,subQ0]});Q58=makeQuery(id+"F9.imprint","IMPRINT",FACE,{"disambiguationData":[TD([[makeQuery(id+"F9.imprint","IMPRINT",EDGE,{"disambiguationData":[TD([[subQ2,-1.0]])],"derivedFrom":subQ1}),1.0]])]});}
            var Q59;
            {var subQ0=sQuery(id+"F9.wireOp",EDGE,"E18.0.0.7");var subQ1=sQuery(id+"F9.wireOp",EDGE,"E14.0.3.0");var subQ2=makeQuery(id+"F9.imprint","INTERSECT",VERTEX,{"disambiguationData":[OD(1.0)],"derivedFrom":[subQ1,subQ0]});Q59=makeQuery(id+"F9.imprint","IMPRINT",FACE,{"disambiguationData":[TD([[makeQuery(id+"F9.imprint","IMPRINT",EDGE,{"disambiguationData":[TD([[subQ2,-1.0]])],"derivedFrom":subQ1}),1.0]])]});}
            var Q60;
            {var subQ5=sQuery(id+"F9.wireOp",EDGE,"E17.0.0.8");var subQ9=sQuery(id+"F9.wireOp",EDGE,"E14.0.3.0");var subQ11=makeQuery(id+"F9.imprint","INTERSECT",VERTEX,{"disambiguationData":[OD(1.0)],"derivedFrom":[subQ9,subQ5]});Q60=makeQuery(id+"F9.imprint","IMPRINT",FACE,{"disambiguationData":[TD([[makeQuery(id+"F9.imprint","IMPRINT",EDGE,{"disambiguationData":[TD([[subQ11,-1.0]])],"derivedFrom":subQ9}),1.0]])]});}
            var Q61;
            {var subQ0=sQuery(id+"F9.wireOp",EDGE,"E18.0.0.6");var subQ1=sQuery(id+"F9.wireOp",EDGE,"E16.0.1.0");var subQ2=makeQuery(id+"F9.imprint","INTERSECT",VERTEX,{"disambiguationData":[OD(2.0)],"derivedFrom":[subQ1,subQ0]});Q61=makeQuery(id+"F9.imprint","IMPRINT",FACE,{"disambiguationData":[TD([[makeQuery(id+"F9.imprint","IMPRINT",EDGE,{"disambiguationData":[TD([[subQ2,-1.0]])],"derivedFrom":subQ1}),-1.0]])]});}
            var Q62;
            {var subQ0=sQuery(id+"F9.wireOp",EDGE,"E17.0.0.9");var subQ1=sQuery(id+"F9.wireOp",EDGE,"E14.0.3.0");var subQ2=makeQuery(id+"F9.imprint","INTERSECT",VERTEX,{"disambiguationData":[OD(1.0)],"derivedFrom":[subQ1,subQ0]});Q62=makeQuery(id+"F9.imprint","IMPRINT",FACE,{"disambiguationData":[TD([[makeQuery(id+"F9.imprint","IMPRINT",EDGE,{"disambiguationData":[TD([[subQ2,-1.0]])],"derivedFrom":subQ1}),-1.0]])]});}
            var Q63;
            {var subQ0=sQuery(id+"F9.wireOp",EDGE,"E18.0.0.7");var subQ1=sQuery(id+"F9.wireOp",EDGE,"E14.0.3.0");var subQ2=makeQuery(id+"F9.imprint","INTERSECT",VERTEX,{"disambiguationData":[OD(1.0)],"derivedFrom":[subQ1,subQ0]});Q63=makeQuery(id+"F9.imprint","IMPRINT",FACE,{"disambiguationData":[TD([[makeQuery(id+"F9.imprint","IMPRINT",EDGE,{"disambiguationData":[TD([[subQ2,-1.0]])],"derivedFrom":subQ1}),-1.0]])]});}
            var Q64;
            {var subQ0=sQuery(id+"F9.wireOp",EDGE,"E17.0.0.8");var subQ1=sQuery(id+"F9.wireOp",EDGE,"E14.0.3.0");var subQ2=makeQuery(id+"F9.imprint","INTERSECT",VERTEX,{"disambiguationData":[OD(1.0)],"derivedFrom":[subQ1,subQ0]});Q64=makeQuery(id+"F9.imprint","IMPRINT",FACE,{"disambiguationData":[TD([[makeQuery(id+"F9.imprint","IMPRINT",EDGE,{"disambiguationData":[TD([[subQ2,-1.0]])],"derivedFrom":subQ1}),-1.0]])]});}
            extrude(context, id + "F15", {"entities" : qUnion([Q0, Q1, Q2, Q3, Q4, Q5, Q6, Q7, Q8, Q9, Q10, Q11, Q12, Q13, Q14, Q15, Q16, Q17, Q18, Q19, Q20, Q21, Q22, Q23, Q24, Q25, Q26, Q27, Q28, Q29, Q30, Q31, Q32, Q33, Q34, Q35, Q36, Q37, Q38, Q39, Q40, Q41, Q42, Q43, Q44, Q45, Q46, Q47, Q48, Q49, Q50, Q51, Q52, Q53, Q54, Q55, Q56, Q57, Q58, Q59, Q60, Q61, Q62, Q63, Q64]), "depth" : 25.4 * mm});
        }
        {
            var Q0;
            {var subQ0=sQuery(id+"F6.wireOp",EDGE,"E11.0.6.0");var subQ1=sQuery(id+"F6.wireOp",EDGE,"E9");var subQ2=makeQuery(id+"F6.imprint","INTERSECT",VERTEX,{"disambiguationData":[OD(1.0)],"derivedFrom":[subQ1,subQ0]});Q0=makeQuery(id+"F6.imprint","IMPRINT",FACE,{"disambiguationData":[TD([[makeQuery(id+"F6.imprint","IMPRINT",EDGE,{"disambiguationData":[TD([[subQ2,-1.0]])],"derivedFrom":subQ1}),1.0]])]});}
            var Q1;
            {var subQ0=sQuery(id+"F6.wireOp",EDGE,"E11.0.6.0");var subQ1=sQuery(id+"F6.wireOp",EDGE,"E9");var subQ2=makeQuery(id+"F6.imprint","INTERSECT",VERTEX,{"disambiguationData":[OD(1.0)],"derivedFrom":[subQ1,subQ0]});Q1=makeQuery(id+"F6.imprint","IMPRINT",FACE,{"disambiguationData":[TD([[makeQuery(id+"F6.imprint","IMPRINT",EDGE,{"disambiguationData":[TD([[subQ2,-1.0]])],"derivedFrom":subQ1}),-1.0]])]});}
            var Q2;
            {var subQ0=sQuery(id+"F6.wireOp",EDGE,"E11.0.6.0");var subQ1=sQuery(id+"F6.wireOp",EDGE,"E11.0.1.0");var subQ2=makeQuery(id+"F6.imprint","INTERSECT",VERTEX,{"disambiguationData":[OD(1.0)],"derivedFrom":[subQ1,subQ0]});Q2=makeQuery(id+"F6.imprint","IMPRINT",FACE,{"disambiguationData":[TD([[makeQuery(id+"F6.imprint","IMPRINT",EDGE,{"disambiguationData":[TD([[subQ2,-1.0]])],"derivedFrom":subQ1}),-1.0]])]});}
            var Q3;
            {var subQ0=sQuery(id+"F6.wireOp",EDGE,"E11.0.6.0");var subQ1=sQuery(id+"F6.wireOp",EDGE,"E11.0.2.0");var subQ2=makeQuery(id+"F6.imprint","INTERSECT",VERTEX,{"disambiguationData":[OD(1.0)],"derivedFrom":[subQ1,subQ0]});Q3=makeQuery(id+"F6.imprint","IMPRINT",FACE,{"disambiguationData":[TD([[makeQuery(id+"F6.imprint","IMPRINT",EDGE,{"disambiguationData":[TD([[subQ2,-1.0]])],"derivedFrom":subQ1}),-1.0]])]});}
            var Q4;
            {var subQ0=sQuery(id+"F6.wireOp",EDGE,"E11.0.6.0");var subQ1=sQuery(id+"F6.wireOp",EDGE,"E11.0.3.0");var subQ2=makeQuery(id+"F6.imprint","INTERSECT",VERTEX,{"disambiguationData":[OD(1.0)],"derivedFrom":[subQ1,subQ0]});Q4=makeQuery(id+"F6.imprint","IMPRINT",FACE,{"disambiguationData":[TD([[makeQuery(id+"F6.imprint","IMPRINT",EDGE,{"disambiguationData":[TD([[subQ2,-1.0]])],"derivedFrom":subQ1}),-1.0]])]});}
            extrude(context, id + "F16", {"entities" : qUnion([Q0, Q1, Q2, Q3, Q4]), "depth" : 25.4 * mm});
        }
        {
            var Q0;
            Q0=qCreatedBy(makeId("Right.planeOp"),FACE);
            var sketch = newSketch(context, id + "F17", { "sketchPlane" : qUnion([Q0])});
            skLineSegment(sketch, "E20.bottom", {"start": v(-4184.38, 1150.1) * mm, "end": v(-3168.38, 1150.1) * mm});
            skLineSegment(sketch, "E20.top", {"start": v(-4184.38, 997.7) * mm, "end": v(-3168.38, 997.7) * mm});
            skLineSegment(sketch, "E20.left", {"start": v(-4184.38, 1150.1) * mm, "end": v(-4184.38, 997.7) * mm});
            skLineSegment(sketch, "E20.right", {"start": v(-3168.38, 1150.1) * mm, "end": v(-3168.38, 997.7) * mm});
            skLineSegment(sketch, "E21", {"start": v(-4184.38, 997.7) * mm, "end": v(-4184.38, 1048.5) * mm});
            skLineSegment(sketch, "E22", {"start": v(-3676.38, 1150.1) * mm, "end": v(-3676.38, 1124.7) * mm});
            skFitSpline(sketch, "E23", {"points": [v(-4184.38, 1048.5) * mm, v(-3676.38, 1124.7) * mm, v(-3168.38, 1048.5) * mm], "startDerivative": vector(1016, 304.8) * mm, "endDerivative": vector(1016, -304.8) * mm});
            skFitSpline(sketch, "E24", {"points": [v(-4184.38, 997.7) * mm, v(-3676.38, 1099.3) * mm, v(-3168.38, 997.7) * mm], "startDerivative": vector(1016, 304.09) * mm, "endDerivative": vector(1016, -304.09) * mm});
            skLineSegment(sketch, "E25.bottom", {"start": v(-4184.38, 1150.1) * mm, "end": v(-4235.18, 1150.1) * mm});
            skLineSegment(sketch, "E25.top", {"start": v(-4184.38, 997.7) * mm, "end": v(-4235.18, 997.7) * mm});
            skLineSegment(sketch, "E25.right", {"start": v(-4235.18, 1150.1) * mm, "end": v(-4235.18, 997.7) * mm});
            skLineSegment(sketch, "E26.bottom", {"start": v(-3168.38, 1150.1) * mm, "end": v(-3117.58, 1150.1) * mm});
            skLineSegment(sketch, "E26.top", {"start": v(-3168.38, 997.7) * mm, "end": v(-3117.58, 997.7) * mm});
            skLineSegment(sketch, "E26.right", {"start": v(-3117.58, 1150.1) * mm, "end": v(-3117.58, 997.7) * mm});
            skLineSegment(sketch, "E27", {"start": v(-3168.38, 1048.5) * mm, "end": v(-3117.58, 1048.5) * mm});
            skCircle(sketch, "E28", {"center": v(-6242.8, 467.04) * mm, "radius": 609.6 * mm});
            skCircle(sketch, "E29", {"center": v(-6242.8, 467.04) * mm, "radius": 558.8 * mm});
            skCircle(sketch, "E30", {"center": v(-6242.8, 467.04) * mm, "radius": 508 * mm});
            skCircle(sketch, "E31", {"center": v(-6242.8, 467.04) * mm, "radius": 457.2 * mm});
            skCircle(sketch, "E32", {"center": v(-6242.8, 467.04) * mm, "radius": 406.4 * mm});
            skEllipse(sketch, "E33", {"center": v(-6446.77, 1852.72) * mm, "majorRadius": 609.6 * mm, "minorRadius": 330.2 * mm, "majorAxis": v(1, 0)});
            skEllipse(sketch, "E34", {"center": v(-6446.77, 1852.72) * mm, "majorRadius": 558.8 * mm, "minorRadius": 304.8 * mm, "majorAxis": v(1, 0)});
            skEllipse(sketch, "E35", {"center": v(-6446.77, 1852.72) * mm, "majorRadius": 508 * mm, "minorRadius": 279.4 * mm, "majorAxis": v(1, 0)});
            skEllipse(sketch, "E36", {"center": v(-6446.77, 1852.72) * mm, "majorRadius": 457.2 * mm, "minorRadius": 254 * mm, "majorAxis": v(1, 0)});
            skLineSegment(sketch, "E37", {"start": v(-7056.37, 1852.72) * mm, "end": v(-5837.17, 1852.72) * mm});
            skEllipse(sketch, "E38", {"center": v(-6446.77, 1852.72) * mm, "majorRadius": 406.4 * mm, "minorRadius": 228.6 * mm, "majorAxis": v(1, 0)});
            skLineSegment(sketch, "E39", {"start": v(-6242.8, 467.04) * mm, "end": v(-5421.86, 467.04) * mm});
            skLineSegment(sketch, "E40", {"start": v(-5421.86, 467.04) * mm, "end": v(-7369.86, 467.04) * mm});
            skEllipse(sketch, "E41", {"center": v(-6446.77, 1852.72) * mm, "majorRadius": 355.6 * mm, "minorRadius": 203.2 * mm, "majorAxis": v(1, 0)});
            skCircle(sketch, "E42", {"center": v(-6242.8, 467.04) * mm, "radius": 355.6 * mm});
            skSolve(sketch);
        }
        {
            var Q0;
            {var subQ3=sQuery(id+"F17.wireOp",EDGE,"E25.bottom");Q0=makeQuery(id+"F17.imprint","IMPRINT",FACE,{"disambiguationData":[TD([[makeQuery(id+"F17.imprint","IMPRINT",EDGE,{"derivedFrom":subQ3}),1.0]])]});}
            var Q1;
            {var subQ3=sQuery(id+"F17.wireOp",EDGE,"E26.bottom");Q1=makeQuery(id+"F17.imprint","IMPRINT",FACE,{"disambiguationData":[TD([[makeQuery(id+"F17.imprint","IMPRINT",EDGE,{"derivedFrom":subQ3}),-1.0]])]});}
            var Q2;
            {var subQ3=sQuery(id+"F17.wireOp",EDGE,"E22");Q2=makeQuery(id+"F17.imprint","IMPRINT",FACE,{"disambiguationData":[TD([[makeQuery(id+"F17.imprint","IMPRINT",EDGE,{"derivedFrom":subQ3}),-1.0]])]});}
            var Q3;
            {var subQ3=sQuery(id+"F17.wireOp",EDGE,"E22");Q3=makeQuery(id+"F17.imprint","IMPRINT",FACE,{"disambiguationData":[TD([[makeQuery(id+"F17.imprint","IMPRINT",EDGE,{"derivedFrom":subQ3}),1.0]])]});}
            extrude(context, id + "F18", {"entities" : qUnion([Q0, Q1, Q2, Q3]), "depth" : 25.4 * mm});
        }
        {
            var Q0;
            Q0=makeQuery(id+"F17.imprint","IMPRINT",FACE,{"disambiguationData":[TD([[makeQuery(id+"F17.imprint","IMPRINT",EDGE,{"derivedFrom":sQuery(id+"F17.wireOp",EDGE,"E20.top")}),1.0]])]});
            extrude(context, id + "F19", {"entities" : qUnion([Q0]), "depth" : 25.4 * mm});
        }
        {
            var Q0;
            {var subQ0=sQuery(id+"F17.wireOp",EDGE,"E24");Q0=makeQuery(id+"F17.imprint","IMPRINT",FACE,{"disambiguationData":[TD([[makeQuery(id+"F17.imprint","IMPRINT",EDGE,{"derivedFrom":subQ0}),1.0]])]});}
            var Q1;
            {var subQ0=sQuery(id+"F17.wireOp",EDGE,"E26.top");Q1=makeQuery(id+"F17.imprint","IMPRINT",FACE,{"disambiguationData":[TD([[makeQuery(id+"F17.imprint","IMPRINT",EDGE,{"derivedFrom":subQ0}),1.0]])]});}
            extrude(context, id + "F20", {"entities" : qUnion([Q0, Q1]), "depth" : 25.4 * mm});
        }
        {
            var Q0;
            {var subQ0=sQuery(id+"F17.wireOp",EDGE,"E40");var subQ1=sQuery(id+"F17.wireOp",EDGE,"E28");var subQ2=makeQuery(id+"F17.imprint","INTERSECT",VERTEX,{"disambiguationData":[OD(0.0)],"derivedFrom":[subQ1,subQ0]});Q0=makeQuery(id+"F17.imprint","IMPRINT",FACE,{"disambiguationData":[TD([[makeQuery(id+"F17.imprint","IMPRINT",EDGE,{"disambiguationData":[TD([[subQ2,1.0]])],"derivedFrom":subQ1}),1.0]])]});}
            var Q1;
            {var subQ0=sQuery(id+"F17.wireOp",EDGE,"E40");var subQ1=sQuery(id+"F17.wireOp",EDGE,"E29");var subQ2=makeQuery(id+"F17.imprint","INTERSECT",VERTEX,{"disambiguationData":[OD(0.0)],"derivedFrom":[subQ1,subQ0]});Q1=makeQuery(id+"F17.imprint","IMPRINT",FACE,{"disambiguationData":[TD([[makeQuery(id+"F17.imprint","IMPRINT",EDGE,{"disambiguationData":[TD([[subQ2,-1.0]])],"derivedFrom":subQ1}),1.0]])]});}
            var Q2;
            {var subQ0=sQuery(id+"F17.wireOp",EDGE,"E40");var subQ1=sQuery(id+"F17.wireOp",EDGE,"E30");var subQ2=makeQuery(id+"F17.imprint","INTERSECT",VERTEX,{"disambiguationData":[OD(0.0)],"derivedFrom":[subQ1,subQ0]});Q2=makeQuery(id+"F17.imprint","IMPRINT",FACE,{"disambiguationData":[TD([[makeQuery(id+"F17.imprint","IMPRINT",EDGE,{"disambiguationData":[TD([[subQ2,1.0]])],"derivedFrom":subQ1}),1.0]])]});}
            var Q3;
            {var subQ0=sQuery(id+"F17.wireOp",EDGE,"E40");var subQ1=sQuery(id+"F17.wireOp",EDGE,"E31");var subQ2=makeQuery(id+"F17.imprint","INTERSECT",VERTEX,{"disambiguationData":[OD(0.0)],"derivedFrom":[subQ1,subQ0]});Q3=makeQuery(id+"F17.imprint","IMPRINT",FACE,{"disambiguationData":[TD([[makeQuery(id+"F17.imprint","IMPRINT",EDGE,{"disambiguationData":[TD([[subQ2,-1.0]])],"derivedFrom":subQ1}),1.0]])]});}
            var Q4;
            {var subQ0=sQuery(id+"F17.wireOp",EDGE,"E37");var subQ1=sQuery(id+"F17.wireOp",EDGE,"E35");var subQ2=makeQuery(id+"F17.imprint","INTERSECT",VERTEX,{"disambiguationData":[OD(0.0)],"derivedFrom":[subQ1,subQ0]});Q4=makeQuery(id+"F17.imprint","IMPRINT",FACE,{"disambiguationData":[TD([[makeQuery(id+"F17.imprint","IMPRINT",EDGE,{"disambiguationData":[TD([[subQ2,-1.0]])],"derivedFrom":subQ1}),1.0]])]});}
            var Q5;
            {var subQ0=sQuery(id+"F17.wireOp",EDGE,"E37");var subQ1=sQuery(id+"F17.wireOp",EDGE,"E33");var subQ2=makeQuery(id+"F17.imprint","INTERSECT",VERTEX,{"disambiguationData":[OD(0.0)],"derivedFrom":[subQ1,subQ0]});Q5=makeQuery(id+"F17.imprint","IMPRINT",FACE,{"disambiguationData":[TD([[makeQuery(id+"F17.imprint","IMPRINT",EDGE,{"disambiguationData":[TD([[subQ2,-1.0]])],"derivedFrom":subQ1}),1.0]])]});}
            var Q6;
            {var subQ0=sQuery(id+"F17.wireOp",EDGE,"E37");var subQ1=sQuery(id+"F17.wireOp",EDGE,"E34");var subQ2=makeQuery(id+"F17.imprint","INTERSECT",VERTEX,{"disambiguationData":[OD(0.0)],"derivedFrom":[subQ1,subQ0]});Q6=makeQuery(id+"F17.imprint","IMPRINT",FACE,{"disambiguationData":[TD([[makeQuery(id+"F17.imprint","IMPRINT",EDGE,{"disambiguationData":[TD([[subQ2,1.0]])],"derivedFrom":subQ1}),1.0]])]});}
            var Q7;
            {var subQ0=sQuery(id+"F17.wireOp",EDGE,"E37");var subQ1=sQuery(id+"F17.wireOp",EDGE,"E36");var subQ2=makeQuery(id+"F17.imprint","INTERSECT",VERTEX,{"disambiguationData":[OD(0.0)],"derivedFrom":[subQ1,subQ0]});Q7=makeQuery(id+"F17.imprint","IMPRINT",FACE,{"disambiguationData":[TD([[makeQuery(id+"F17.imprint","IMPRINT",EDGE,{"disambiguationData":[TD([[subQ2,1.0]])],"derivedFrom":subQ1}),1.0]])]});}
            var Q8;
            {var subQ0=sQuery(id+"F17.wireOp",EDGE,"E40");var subQ1=sQuery(id+"F17.wireOp",EDGE,"E32");var subQ2=makeQuery(id+"F17.imprint","INTERSECT",VERTEX,{"disambiguationData":[OD(0.0)],"derivedFrom":[subQ1,subQ0]});Q8=makeQuery(id+"F17.imprint","IMPRINT",FACE,{"disambiguationData":[TD([[makeQuery(id+"F17.imprint","IMPRINT",EDGE,{"disambiguationData":[TD([[subQ2,1.0]])],"derivedFrom":subQ1}),1.0]])]});}
            var Q9;
            {var subQ0=sQuery(id+"F17.wireOp",EDGE,"E38");var subQ1=sQuery(id+"F17.wireOp",EDGE,"E37");var subQ2=makeQuery(id+"F17.imprint","INTERSECT",VERTEX,{"disambiguationData":[OD(0.0)],"derivedFrom":[subQ1,subQ0]});Q9=makeQuery(id+"F17.imprint","IMPRINT",FACE,{"disambiguationData":[TD([[makeQuery(id+"F17.imprint","IMPRINT",EDGE,{"disambiguationData":[TD([[subQ2,-1.0]])],"derivedFrom":subQ1}),-1.0]])]});}
            extrude(context, id + "F21", {"entities" : qUnion([Q0, Q1, Q2, Q3, Q4, Q5, Q6, Q7, Q8, Q9]), "depth" : 11.9 * mm});
        }
        {
            var Q0;
            Q0=qCreatedBy(makeId("Right.planeOp"),FACE);
            var sketch = newSketch(context, id + "F22", { "sketchPlane" : qUnion([Q0])});
            skLineSegment(sketch, "E43.bottom", {"start": v(-6818.9, 2956.89) * mm, "end": v(-5802.9, 2956.89) * mm});
            skLineSegment(sketch, "E43.top", {"start": v(-6818.9, 2296.49) * mm, "end": v(-5802.9, 2296.49) * mm});
            skLineSegment(sketch, "E43.left", {"start": v(-6818.9, 2956.89) * mm, "end": v(-6818.9, 2296.49) * mm});
            skLineSegment(sketch, "E43.right", {"start": v(-5802.9, 2956.89) * mm, "end": v(-5802.9, 2296.49) * mm});
            skPoint(sketch, "E44.2.internal.snap0", {"position": v(-6310.9, 2296.49) * mm});
            skFitSpline(sketch, "E44", {"points": [v(-6818.9, 2455.08) * mm, v(-6776.17, 2416.03) * mm, v(-6310.9, 2316.1) * mm, v(-5846.94, 2410.57) * mm, v(-5802.9, 2448.9) * mm], "startDerivative": vector(278.44, 92) * mm, "endDerivative": vector(293.1, -77.25) * mm});
            skLineSegment(sketch, "E45", {"start": v(-6818.9, 2455.08) * mm, "end": v(-5802.9, 2448.9) * mm});
            skFitSpline(sketch, "E46.MirrorCS", {"points": [v(-6818.9, 2455.08) * mm, v(-6775.7, 2493.6) * mm, v(-6309.25, 2587.87) * mm, v(-5846.47, 2487.77) * mm, v(-5802.9, 2448.9) * mm], "startDerivative": vector(277.3, -95.38) * mm, "endDerivative": vector(294.02, 73.68) * mm});
            skFitSpline(sketch, "E47", {"points": [v(-6818.9, 2499.15) * mm, v(-6806.48, 2515.36) * mm, v(-6694.52, 2570.18) * mm, v(-6309.24, 2601.07) * mm, v(-5903.88, 2552.42) * mm, v(-5808.7, 2495.07) * mm, v(-5802.9, 2485.75) * mm], "startDerivative": vector(68.1, 217.62) * mm, "endDerivative": vector(88.91, -154.43) * mm});
            skLineSegment(sketch, "E48.bottom", {"start": v(-6975.52, 2954.8) * mm, "end": v(-7991.52, 2954.8) * mm});
            skLineSegment(sketch, "E48.top", {"start": v(-6975.52, 2294.4) * mm, "end": v(-7991.52, 2294.4) * mm});
            skLineSegment(sketch, "E48.left", {"start": v(-6975.52, 2954.8) * mm, "end": v(-6975.52, 2294.4) * mm});
            skLineSegment(sketch, "E48.right", {"start": v(-7991.52, 2954.8) * mm, "end": v(-7991.52, 2294.4) * mm});
            skLineSegment(sketch, "E49", {"start": v(-7991.52, 2294.4) * mm, "end": v(-7991.52, 2497.6) * mm});
            skLineSegment(sketch, "E50", {"start": v(-7991.52, 2497.6) * mm, "end": v(-7940.72, 2497.6) * mm});
            skLineSegment(sketch, "E51", {"start": v(-7483.52, 2954.8) * mm, "end": v(-7483.52, 2294.4) * mm, "construction": true});
            skFitSpline(sketch, "E52", {"points": [v(-7940.72, 2497.6) * mm, v(-7800.4, 2376.59) * mm, v(-7483.52, 2344.18) * mm], "startDerivative": vector(153.31, -299.47) * mm, "endDerivative": vector(769.92, -22.4) * mm});
            skLineSegment(sketch, "E53", {"start": v(-7991.52, 2624.6) * mm, "end": v(-6975.52, 2624.6) * mm, "construction": true});
            skFitSpline(sketch, "E54", {"points": [v(-7940.72, 2497.6) * mm, v(-7969.36, 2557.36) * mm, v(-7991.52, 2624.6) * mm], "startDerivative": vector(-88.86, 158.1) * mm, "endDerivative": vector(-45.89, 176.22) * mm});
            skFitSpline(sketch, "E55", {"points": [v(-7940.72, 2624.6) * mm, v(-7878.3, 2486.12) * mm, v(-7764.74, 2396.58) * mm, v(-7521.24, 2366) * mm, v(-7483.52, 2366) * mm], "startDerivative": vector(207.81, -551.36) * mm, "endDerivative": vector(204.1, 4.3) * mm});
            skFitSpline(sketch, "E56.MirrorCS", {"points": [v(-7026.32, 2624.6) * mm, v(-7088.74, 2486.12) * mm, v(-7202.3, 2396.58) * mm, v(-7445.8, 2366) * mm, v(-7483.52, 2366) * mm], "startDerivative": vector(-207.81, -551.36) * mm, "endDerivative": vector(-204.1, 4.3) * mm});
            skFitSpline(sketch, "E57.MirrorCS", {"points": [v(-7026.32, 2497.6) * mm, v(-7166.63, 2376.59) * mm, v(-7483.52, 2344.18) * mm], "startDerivative": vector(-153.31, -299.47) * mm, "endDerivative": vector(-769.92, -22.4) * mm});
            skLineSegment(sketch, "E58.MirrorCS", {"start": v(-6975.52, 2497.6) * mm, "end": v(-7026.32, 2497.6) * mm});
            skFitSpline(sketch, "E59.MirrorCS", {"points": [v(-7026.32, 2497.6) * mm, v(-6997.68, 2557.36) * mm, v(-6975.52, 2624.6) * mm], "startDerivative": vector(88.86, 158.1) * mm, "endDerivative": vector(45.89, 176.22) * mm});
            skLineSegment(sketch, "E60", {"start": v(-7940.72, 2624.6) * mm, "end": v(-7991.52, 2624.6) * mm});
            skLineSegment(sketch, "E61", {"start": v(-7026.32, 2624.6) * mm, "end": v(-6975.52, 2624.6) * mm});
            skSolve(sketch);
        }
        {
            var Q0;
            {var subQ1=sQuery(id+"F22.wireOp",EDGE,"E48.top");Q0=makeQuery(id+"F22.imprint","IMPRINT",FACE,{"disambiguationData":[TD([[makeQuery(id+"F22.imprint","IMPRINT",EDGE,{"derivedFrom":subQ1}),-1.0]])]});}
            extrude(context, id + "F23", {"entities" : qUnion([Q0]), "depth" : 2133.6 * mm});
        }
        {
            var Q0;
            Q0=makeQuery(id+"F22.imprint","IMPRINT",FACE,{"disambiguationData":[TD([[makeQuery(id+"F22.imprint","IMPRINT",EDGE,{"derivedFrom":sQuery(id+"F22.wireOp",EDGE,"E52")}),1.0]])]});
            extrude(context, id + "F24", {"entities" : qUnion([Q0]), "depth" : 2133.6 * mm});
        }
        {
            var Q0;
            Q0=qCreatedBy(makeId("Right.planeOp"),FACE);
            var sketch = newSketch(context, id + "F25", { "sketchPlane" : qUnion([Q0])});
            skLineSegment(sketch, "E62.bottom", {"start": v(-640.98, 1301.28) * mm, "end": v(578.22, 1301.28) * mm});
            skLineSegment(sketch, "E62.top", {"start": v(-640.98, -1137.12) * mm, "end": v(578.22, -1137.12) * mm});
            skLineSegment(sketch, "E62.left", {"start": v(-640.98, 1301.28) * mm, "end": v(-640.98, -1137.12) * mm});
            skLineSegment(sketch, "E62.right", {"start": v(578.22, 1301.28) * mm, "end": v(578.22, -1137.12) * mm});
            skPoint(sketch, "E62.middle", {"position": v(-31.38, 82.08) * mm});
            skEllipse(sketch, "E63", {"center": v(-31.38, 82.08) * mm, "majorRadius": 558.8 * mm, "minorRadius": 330.2 * mm, "majorAxis": v(1, 0)});
            skEllipse(sketch, "E64", {"center": v(-31.38, 82.08) * mm, "majorRadius": 508 * mm, "minorRadius": 203.2 * mm, "majorAxis": v(1, 0)});
            skEllipse(sketch, "E65", {"center": v(-31.38, 82.08) * mm, "majorRadius": 508 * mm, "minorRadius": 317.5 * mm, "majorAxis": v(1, 0)});
            skLineSegment(sketch, "E66", {"start": v(-590.18, 82.08) * mm, "end": v(527.42, 82.08) * mm, "construction": true});
            skLineSegment(sketch, "E67.bottom", {"start": v(540.12, -247.78) * mm, "end": v(-602.88, -247.78) * mm});
            skLineSegment(sketch, "E67.top", {"start": v(540.12, -146.18) * mm, "end": v(-602.88, -146.18) * mm});
            skLineSegment(sketch, "E67.left", {"start": v(540.12, -247.78) * mm, "end": v(540.12, -146.18) * mm});
            skLineSegment(sketch, "E67.right", {"start": v(-602.88, -247.78) * mm, "end": v(-602.88, -146.18) * mm});
            skPoint(sketch, "E67.middle", {"position": v(-31.38, -196.98) * mm});
            skLineSegment(sketch, "E68", {"start": v(476.62, 82.08) * mm, "end": v(527.42, 82.08) * mm});
            skCircle(sketch, "E69", {"center": v(502.02, 82.08) * mm, "radius": 25.4 * mm});
            skLineSegment(sketch, "E70", {"start": v(-539.38, 82.08) * mm, "end": v(-590.18, 82.08) * mm});
            skLineSegment(sketch, "E71", {"start": v(-31.38, -247.78) * mm, "end": v(-31.38, 507.68) * mm});
            skCircle(sketch, "E72.MirrorC", {"center": v(-564.78, 82.08) * mm, "radius": 25.4 * mm});
            skSolve(sketch);
        }
        {
            var Q0;
            {var subQ0=sQuery(id+"F25.wireOp",EDGE,"E65");var subQ5=sQuery(id+"F25.wireOp",EDGE,"E67.top");var subQ7=makeQuery(id+"F25.imprint","INTERSECT",VERTEX,{"disambiguationData":[OD(1.0)],"derivedFrom":[subQ0,subQ5]});Q0=makeQuery(id+"F25.imprint","IMPRINT",FACE,{"disambiguationData":[TD([[makeQuery(id+"F25.imprint","IMPRINT",EDGE,{"disambiguationData":[TD([[subQ7,-1.0]])],"derivedFrom":subQ5}),-1.0]])]});}
            var Q1;
            {var subQ2=sQuery(id+"F25.wireOp",EDGE,"E63");var subQ4=sQuery(id+"F25.wireOp",EDGE,"E67.top");var subQ5=makeQuery(id+"F25.imprint","INTERSECT",VERTEX,{"disambiguationData":[OD(1.0)],"derivedFrom":[subQ2,subQ4]});Q1=makeQuery(id+"F25.imprint","IMPRINT",FACE,{"disambiguationData":[TD([[makeQuery(id+"F25.imprint","IMPRINT",EDGE,{"disambiguationData":[TD([[subQ5,-1.0]])],"derivedFrom":subQ4}),-1.0]])]});}
            var Q2;
            {var subQ0=sQuery(id+"F25.wireOp",EDGE,"E65");var subQ5=sQuery(id+"F25.wireOp",EDGE,"E67.top");var subQ6=makeQuery(id+"F25.imprint","INTERSECT",VERTEX,{"disambiguationData":[OD(0.0)],"derivedFrom":[subQ0,subQ5]});Q2=makeQuery(id+"F25.imprint","IMPRINT",FACE,{"disambiguationData":[TD([[makeQuery(id+"F25.imprint","IMPRINT",EDGE,{"disambiguationData":[TD([[subQ6,1.0]])],"derivedFrom":subQ5}),-1.0]])]});}
            var Q3;
            {var subQ2=sQuery(id+"F25.wireOp",EDGE,"E63");var subQ4=sQuery(id+"F25.wireOp",EDGE,"E67.top");var subQ5=makeQuery(id+"F25.imprint","INTERSECT",VERTEX,{"disambiguationData":[OD(0.0)],"derivedFrom":[subQ2,subQ4]});Q3=makeQuery(id+"F25.imprint","IMPRINT",FACE,{"disambiguationData":[TD([[makeQuery(id+"F25.imprint","IMPRINT",EDGE,{"disambiguationData":[TD([[subQ5,1.0]])],"derivedFrom":subQ4}),-1.0]])]});}
            extrude(context, id + "F26", {"entities" : qUnion([Q0, Q1, Q2, Q3]), "depth" : 2133.6 * mm});
        }
        {
            var Q0;
            {var subQ2=sQuery(id+"F25.wireOp",EDGE,"E63");var subQ4=sQuery(id+"F25.wireOp",EDGE,"E71");var subQ5=makeQuery(id+"F25.imprint","INTERSECT",VERTEX,{"derivedFrom":[subQ2,subQ4]});Q0=makeQuery(id+"F25.imprint","IMPRINT",FACE,{"disambiguationData":[TD([[makeQuery(id+"F25.imprint","IMPRINT",EDGE,{"disambiguationData":[TD([[subQ5,1.0]])],"derivedFrom":subQ4}),1.0]])]});}
            var Q1;
            {var subQ0=sQuery(id+"F25.wireOp",EDGE,"E70");Q1=makeQuery(id+"F25.imprint","IMPRINT",FACE,{"disambiguationData":[TD([[makeQuery(id+"F25.imprint","IMPRINT",EDGE,{"derivedFrom":subQ0}),-1.0]])]});}
            var Q2;
            {var subQ0=sQuery(id+"F25.wireOp",EDGE,"E70");Q2=makeQuery(id+"F25.imprint","IMPRINT",FACE,{"disambiguationData":[TD([[makeQuery(id+"F25.imprint","IMPRINT",EDGE,{"derivedFrom":subQ0}),1.0]])]});}
            extrude(context, id + "F27", {"entities" : qUnion([Q0, Q1, Q2]), "depth" : 2133.6 * mm});
        }
        {
            var Q0;
            {var subQ0=sQuery(id+"F25.wireOp",EDGE,"E68");Q0=makeQuery(id+"F25.imprint","IMPRINT",FACE,{"disambiguationData":[TD([[makeQuery(id+"F25.imprint","IMPRINT",EDGE,{"derivedFrom":subQ0}),-1.0]])]});}
            var Q1;
            {var subQ0=sQuery(id+"F25.wireOp",EDGE,"E68");Q1=makeQuery(id+"F25.imprint","IMPRINT",FACE,{"disambiguationData":[TD([[makeQuery(id+"F25.imprint","IMPRINT",EDGE,{"derivedFrom":subQ0}),1.0]])]});}
            var Q2;
            {var subQ2=sQuery(id+"F25.wireOp",EDGE,"E63");var subQ4=sQuery(id+"F25.wireOp",EDGE,"E71");var subQ5=makeQuery(id+"F25.imprint","INTERSECT",VERTEX,{"derivedFrom":[subQ2,subQ4]});Q2=makeQuery(id+"F25.imprint","IMPRINT",FACE,{"disambiguationData":[TD([[makeQuery(id+"F25.imprint","IMPRINT",EDGE,{"disambiguationData":[TD([[subQ5,1.0]])],"derivedFrom":subQ4}),-1.0]])]});}
            extrude(context, id + "F28", {"entities" : qUnion([Q0, Q1, Q2]), "depth" : 2133.6 * mm});
        }
        {
            var Q0;
            Q0=makeQuery(id+"F26.opExtrude","SWEPT_BODY",BODY,{"disambiguationData":[OSD([sQuery(id+"F25.wireOp",EDGE,"E63"),sQuery(id+"F25.wireOp",EDGE,"E64"),sQuery(id+"F25.wireOp",EDGE,"E67.top"),sQuery(id+"F25.wireOp",EDGE,"E69"),sQuery(id+"F25.wireOp",EDGE,"E72.MirrorC")])]});
            transform(context, id + "F29", {"entities" : qUnion([Q0]), "transformType" : TransformType.TRANSLATION_3D, "dx" : 0 * mm, "dy" : 0 * mm, "dz" : -20.32 * mm, "makeCopy" : false});
        }
        {
            var Q0;
            Q0=makeQuery(id+"F28.opExtrude","SWEPT_BODY",BODY,{"disambiguationData":[OSD([sQuery(id+"F25.wireOp",EDGE,"E63"),sQuery(id+"F25.wireOp",EDGE,"E65"),sQuery(id+"F25.wireOp",EDGE,"E69"),sQuery(id+"F25.wireOp",EDGE,"E71")])]});
            transform(context, id + "F30", {"entities" : qUnion([Q0]), "transformType" : TransformType.TRANSLATION_3D, "dx" : 0 * mm, "dy" : 0 * mm, "dz" : 60.96 * mm, "makeCopy" : false});
        }
        {
            var Q0;
            Q0=qCreatedBy(makeId("Front.planeOp"),FACE);
            var sketch = newSketch(context, id + "F31", { "sketchPlane" : qUnion([Q0])});
            skEllipticalArc(sketch, "E73", {});
            skLineSegment(sketch, "E74", {"start": v(0, 4628.2) * mm, "end": v(3112.55, 4628.2) * mm});
            skLineSegment(sketch, "E75", {"start": v(3112.55, 4628.2) * mm, "end": v(-1068.44, 4628.2) * mm});
            skFitSpline(sketch, "E76.0", {"points": [v(634.8, 4619.53) * mm, v(635.1, 4628.2) * mm, v(634.8, 4636.88) * mm, v(633.56, 4648.34) * mm, v(630.55, 4662.37) * mm, v(624.79, 4678.4) * mm, v(617.18, 4693.5) * mm, v(607.99, 4707.64) * mm, v(597.4, 4720.87) * mm, v(585.57, 4733.28) * mm, v(572.58, 4744.98) * mm, v(558.48, 4756.04) * mm, v(543.3, 4766.54) * mm, v(527.03, 4776.53) * mm, v(509.72, 4786.06) * mm, v(491.34, 4795.15) * mm, v(475.16, 4802.37) * mm, v(461.7, 4807.95) * mm, v(451.33, 4812.03) * mm, v(442.48, 4815.35) * mm, v(435.26, 4817.95) * mm, v(429.8, 4819.88) * mm, v(424.26, 4821.78) * mm, v(416.82, 4824.27) * mm, v(407.4, 4827.31) * mm, v(395.89, 4830.85) * mm, v(380.3, 4835.4) * mm, v(360.35, 4840.8) * mm, v(335.7, 4846.83) * mm, v(310.4, 4852.4) * mm, v(275.82, 4859.2) * mm, v(231.14, 4866.53) * mm, v(184.8, 4872.3) * mm, v(146.88, 4875.97) * mm, v(118.08, 4878.23) * mm, v(88.95, 4880) * mm, v(64.44, 4881.05) * mm, v(44.7, 4881.65) * mm, v(29.85, 4881.97) * mm, v(17.43, 4882.13) * mm, v(7.48, 4882.2) * mm, v(0, 4882.21) * mm, v(-7.48, 4882.2) * mm, v(-17.43, 4882.13) * mm, v(-29.85, 4881.97) * mm, v(-44.7, 4881.65) * mm, v(-64.44, 4881.05) * mm, v(-88.95, 4880) * mm, v(-118.08, 4878.23) * mm, v(-146.88, 4875.97) * mm, v(-184.8, 4872.3) * mm, v(-231.14, 4866.53) * mm, v(-275.82, 4859.2) * mm, v(-310.4, 4852.4) * mm, v(-335.7, 4846.83) * mm, v(-360.35, 4840.8) * mm, v(-380.3, 4835.4) * mm, v(-395.89, 4830.85) * mm, v(-407.4, 4827.31) * mm, v(-416.82, 4824.27) * mm, v(-424.26, 4821.78) * mm, v(-429.8, 4819.88) * mm, v(-435.26, 4817.95) * mm, v(-442.48, 4815.35) * mm, v(-451.33, 4812.03) * mm, v(-461.7, 4807.95) * mm, v(-475.16, 4802.37) * mm, v(-491.34, 4795.15) * mm, v(-509.72, 4786.06) * mm, v(-527.03, 4776.53) * mm, v(-543.3, 4766.54) * mm, v(-558.48, 4756.04) * mm, v(-572.58, 4744.98) * mm, v(-585.57, 4733.28) * mm, v(-597.4, 4720.87) * mm, v(-607.99, 4707.64) * mm, v(-617.18, 4693.5) * mm, v(-624.79, 4678.4) * mm, v(-630.55, 4662.37) * mm, v(-633.56, 4648.34) * mm, v(-634.8, 4636.88) * mm, v(-635.1, 4628.2) * mm, v(-634.8, 4619.53) * mm, v(-633.56, 4608.07) * mm, v(-630.55, 4594.05) * mm, v(-624.79, 4578) * mm, v(-617.18, 4562.9) * mm, v(-607.99, 4548.77) * mm, v(-597.4, 4535.54) * mm, v(-585.57, 4523.13) * mm, v(-572.58, 4511.44) * mm, v(-558.48, 4500.38) * mm, v(-543.3, 4489.88) * mm, v(-527.03, 4479.89) * mm, v(-509.72, 4470.36) * mm, v(-491.34, 4461.27) * mm, v(-475.16, 4454.04) * mm, v(-461.7, 4448.47) * mm, v(-451.33, 4444.39) * mm, v(-442.48, 4441.07) * mm, v(-435.26, 4438.47) * mm, v(-429.8, 4436.54) * mm, v(-424.26, 4434.64) * mm, v(-416.82, 4432.14) * mm, v(-407.4, 4429.1) * mm, v(-395.89, 4425.57) * mm, v(-380.3, 4421.01) * mm, v(-360.35, 4415.6) * mm, v(-335.7, 4409.58) * mm, v(-310.4, 4404.02) * mm, v(-275.82, 4397.22) * mm, v(-231.14, 4389.88) * mm, v(-184.8, 4384.1) * mm, v(-146.88, 4380.45) * mm, v(-118.08, 4378.19) * mm, v(-88.95, 4376.42) * mm, v(-64.44, 4375.36) * mm, v(-44.7, 4374.76) * mm, v(-29.85, 4374.44) * mm, v(-17.43, 4374.28) * mm, v(-7.48, 4374.22) * mm, v(0, 4374.2) * mm, v(7.48, 4374.22) * mm, v(17.43, 4374.28) * mm, v(29.85, 4374.44) * mm, v(44.7, 4374.76) * mm, v(64.44, 4375.36) * mm, v(88.95, 4376.42) * mm, v(118.08, 4378.19) * mm, v(146.88, 4380.45) * mm, v(184.8, 4384.1) * mm, v(231.14, 4389.88) * mm, v(275.82, 4397.22) * mm, v(310.4, 4404.02) * mm, v(335.7, 4409.58) * mm, v(360.35, 4415.6) * mm, v(380.3, 4421.01) * mm, v(395.89, 4425.57) * mm, v(407.4, 4429.1) * mm, v(416.82, 4432.14) * mm, v(424.26, 4434.64) * mm, v(429.8, 4436.54) * mm, v(435.26, 4438.47) * mm, v(442.48, 4441.07) * mm, v(451.33, 4444.39) * mm, v(461.7, 4448.47) * mm, v(475.16, 4454.04) * mm, v(491.34, 4461.27) * mm, v(509.72, 4470.36) * mm, v(527.03, 4479.89) * mm, v(543.3, 4489.88) * mm, v(558.48, 4500.38) * mm, v(572.58, 4511.44) * mm, v(585.57, 4523.13) * mm, v(597.4, 4535.54) * mm, v(607.99, 4548.77) * mm, v(617.18, 4562.9) * mm, v(624.79, 4578) * mm, v(630.55, 4594.05) * mm, v(633.56, 4608.07) * mm, v(634.8, 4619.53) * mm, v(635.1, 4628.2) * mm, v(634.8, 4636.88) * mm]});
            skEllipticalArc(sketch, "E77.0.1.0", {});
            skEllipticalArc(sketch, "E77.0.2.0", {});
            skEllipticalArc(sketch, "E77.0.3.0", {});
            skEllipticalArc(sketch, "E77.0.4.0", {});
            skEllipticalArc(sketch, "E77.0.5.0", {});
            skEllipticalArc(sketch, "E77.0.6.0", {});
            skEllipticalArc(sketch, "E77.0.7.0", {});
            skEllipticalArc(sketch, "E77.0.8.0", {});
            skEllipticalArc(sketch, "E77.0.9.0", {});
            skLineSegment(sketch, "E77.direction1", {"start": v(-584.2, 4628.2) * mm, "end": v(-503.88, 4668.43) * mm, "construction": true});
            skLineSegment(sketch, "E77.direction2", {"start": v(-584.2, 4628.2) * mm, "end": v(-584.2, 4679) * mm, "construction": true});
            skLineSegment(sketch, "E78", {"start": v(584.2, 5085.4) * mm, "end": v(584.2, 4628.2) * mm});
            skLineSegment(sketch, "E79", {"start": v(-584.2, 5085.4) * mm, "end": v(-584.2, 4628.2) * mm});
            skEllipticalArc(sketch, "E80", {});
            skEllipticalArc(sketch, "E81.0.1.0", {});
            skEllipticalArc(sketch, "E81.0.2.0", {});
            skEllipticalArc(sketch, "E81.0.3.0", {});
            skEllipticalArc(sketch, "E81.0.4.0", {});
            skEllipticalArc(sketch, "E81.0.5.0", {});
            skEllipticalArc(sketch, "E81.0.6.0", {});
            skEllipticalArc(sketch, "E81.0.7.0", {});
            skLineSegment(sketch, "E81.direction1", {"start": v(1176.28, 4628.2) * mm, "end": v(1201.68, 4628.2) * mm, "construction": true});
            skLineSegment(sketch, "E81.direction2", {"start": v(1176.28, 4628.2) * mm, "end": v(1176.28, 4704.4) * mm, "construction": true});
            skLineSegment(sketch, "E82.bottom", {"start": v(2419.3, 4348.8) * mm, "end": v(1203.26, 4348.8) * mm});
            skLineSegment(sketch, "E82.top", {"start": v(2419.3, 5060) * mm, "end": v(1203.26, 5060) * mm});
            skLineSegment(sketch, "E82.left", {"start": v(2419.3, 4348.8) * mm, "end": v(2419.3, 5060) * mm});
            skLineSegment(sketch, "E82.right", {"start": v(1203.26, 4348.8) * mm, "end": v(1203.26, 5060) * mm});
            skLineSegment(sketch, "E83", {"start": v(1203.26, 4993.15) * mm, "end": v(1230.29, 4993.15) * mm});
            skLineSegment(sketch, "E84.0.1.0", {"start": v(1203.26, 4916.95) * mm, "end": v(1230.29, 4916.95) * mm});
            skLineSegment(sketch, "E84.0.2.0", {"start": v(1203.26, 4840.75) * mm, "end": v(1230.29, 4840.75) * mm});
            skLineSegment(sketch, "E84.0.3.0", {"start": v(1203.26, 4764.55) * mm, "end": v(1230.29, 4764.55) * mm});
            skLineSegment(sketch, "E84.0.4.0", {"start": v(1203.26, 4688.35) * mm, "end": v(1230.29, 4688.35) * mm});
            skLineSegment(sketch, "E84.0.5.0", {"start": v(1203.26, 4612.15) * mm, "end": v(1230.29, 4612.15) * mm});
            skLineSegment(sketch, "E84.0.6.0", {"start": v(1203.26, 4535.95) * mm, "end": v(1230.29, 4535.95) * mm});
            skLineSegment(sketch, "E84.direction1", {"start": v(1203.26, 4993.15) * mm, "end": v(1228.66, 4993.15) * mm, "construction": true});
            skLineSegment(sketch, "E84.direction2", {"start": v(1203.26, 4993.15) * mm, "end": v(1203.26, 4916.95) * mm, "construction": true});
            skLineSegment(sketch, "E85", {"start": v(1811.28, 8913.73) * mm, "end": v(1811.28, 3953.27) * mm, "construction": true});
            skLineSegment(sketch, "E86.MirrorCS", {"start": v(2419.3, 4535.95) * mm, "end": v(2392.27, 4535.95) * mm});
            skLineSegment(sketch, "E87.MirrorCS", {"start": v(2419.3, 4612.15) * mm, "end": v(2392.27, 4612.15) * mm});
            skLineSegment(sketch, "E88.MirrorCS", {"start": v(2419.3, 4688.35) * mm, "end": v(2392.27, 4688.35) * mm});
            skLineSegment(sketch, "E89.MirrorCS", {"start": v(2419.3, 4764.55) * mm, "end": v(2392.27, 4764.55) * mm});
            skLineSegment(sketch, "E90.MirrorCS", {"start": v(2419.3, 4840.75) * mm, "end": v(2392.27, 4840.75) * mm});
            skLineSegment(sketch, "E91.MirrorCS", {"start": v(2419.3, 4916.95) * mm, "end": v(2392.27, 4916.95) * mm});
            skLineSegment(sketch, "E92.MirrorCS", {"start": v(2419.3, 4993.15) * mm, "end": v(2393.9, 4993.15) * mm});
            skEllipticalArc(sketch, "E93", {});
            skLineSegment(sketch, "E94", {"start": v(1176.28, 5726.19) * mm, "end": v(2574.86, 5726.19) * mm});
            skEllipticalArc(sketch, "E95.0.1.0", {});
            skEllipticalArc(sketch, "E95.0.2.0", {});
            skEllipticalArc(sketch, "E95.0.3.0", {});
            skEllipticalArc(sketch, "E95.0.4.0", {});
            skEllipticalArc(sketch, "E95.0.5.0", {});
            skEllipticalArc(sketch, "E95.0.6.0", {});
            skEllipticalArc(sketch, "E95.0.7.0", {});
            skLineSegment(sketch, "E95.direction1", {"start": v(1176.28, 5726.19) * mm, "end": v(1201.68, 5726.19) * mm, "construction": true});
            skLineSegment(sketch, "E95.direction2", {"start": v(1176.28, 5726.19) * mm, "end": v(1176.28, 5764.29) * mm, "construction": true});
            skLineSegment(sketch, "E96.bottom", {"start": v(2419.3, 6246.89) * mm, "end": v(1203.26, 6246.89) * mm});
            skLineSegment(sketch, "E96.top", {"start": v(2419.3, 5738.89) * mm, "end": v(1203.26, 5738.89) * mm});
            skLineSegment(sketch, "E96.left", {"start": v(2419.3, 6246.89) * mm, "end": v(2419.3, 5738.89) * mm});
            skLineSegment(sketch, "E96.right", {"start": v(1203.26, 6246.89) * mm, "end": v(1203.26, 5738.89) * mm});
            skLineSegment(sketch, "E97", {"start": v(1203.26, 5859.51) * mm, "end": v(1230.34, 5859.51) * mm});
            skLineSegment(sketch, "E98", {"start": v(1203.26, 5897.61) * mm, "end": v(1230.34, 5897.61) * mm});
            skLineSegment(sketch, "E99.MirrorCS", {"start": v(2419.3, 5897.61) * mm, "end": v(2392.21, 5897.61) * mm});
            skLineSegment(sketch, "E100.MirrorCS", {"start": v(2419.3, 5859.51) * mm, "end": v(2392.21, 5859.51) * mm});
            skEllipticalArc(sketch, "E101", {});
            skLineSegment(sketch, "E102", {"start": v(1176.28, 8286.5) * mm, "end": v(2561.11, 8286.5) * mm});
            skEllipticalArc(sketch, "E103.0.1.0", {});
            skEllipticalArc(sketch, "E103.0.2.0", {});
            skEllipticalArc(sketch, "E103.0.3.0", {});
            skEllipticalArc(sketch, "E103.0.4.0", {});
            skEllipticalArc(sketch, "E103.0.5.0", {});
            skEllipticalArc(sketch, "E103.0.6.0", {});
            skEllipticalArc(sketch, "E103.0.7.0", {});
            skLineSegment(sketch, "E103.direction1", {"start": v(1176.28, 8286.5) * mm, "end": v(1201.68, 8286.5) * mm, "construction": true});
            skLineSegment(sketch, "E103.direction2", {"start": v(1176.28, 8286.5) * mm, "end": v(1176.28, 8324.6) * mm, "construction": true});
            skLineSegment(sketch, "E104.bottom", {"start": v(2419.3, 9062.2) * mm, "end": v(1203.26, 9062.2) * mm});
            skLineSegment(sketch, "E104.top", {"start": v(2419.3, 8306.22) * mm, "end": v(1203.26, 8306.22) * mm});
            skLineSegment(sketch, "E104.left", {"start": v(2419.3, 9062.2) * mm, "end": v(2419.3, 8306.22) * mm});
            skLineSegment(sketch, "E104.right", {"start": v(1203.26, 9062.2) * mm, "end": v(1203.26, 8306.22) * mm});
            skPoint(sketch, "E104.middle", {"position": v(1811.28, 8684.2) * mm});
            skLineSegment(sketch, "E105", {"start": v(1203.26, 8456.46) * mm, "end": v(1221.78, 8456.46) * mm});
            skLineSegment(sketch, "E106", {"start": v(1203.26, 8494.56) * mm, "end": v(1221.78, 8494.56) * mm});
            skLineSegment(sketch, "E107.MirrorCS", {"start": v(2419.3, 8456.46) * mm, "end": v(2400.78, 8456.46) * mm});
            skLineSegment(sketch, "E108.MirrorCS", {"start": v(2419.3, 8494.56) * mm, "end": v(2400.78, 8494.56) * mm});
            const initialGuessF31  = {"E73": [0, 4.628207683563232, 1, 0, 0.5842, 0.2032, 3.141592653589793, 0], "E77.0.1.0": [0, 4.679007683563232, 1, 0, 0.5842, 0.2032, 3.141592653589793, 0], "E77.0.2.0": [0, 4.729807683563232, 1, 0, 0.5842, 0.2032, 3.141592653589793, 0], "E77.0.3.0": [0, 4.780607683563232, 1, 0, 0.5842, 0.2032, 3.141592653589793, 0], "E77.0.4.0": [0, 4.831407683563231, 1, 0, 0.5842, 0.2032, 3.141592653589793, 0], "E77.0.5.0": [0, 4.882207683563231, 1, 0, 0.5842, 0.2032, 3.141592653589793, 0], "E77.0.6.0": [0, 4.933007683563231, 1, 0, 0.5842, 0.2032, 3.141592653589793, 0], "E77.0.7.0": [0, 4.983807683563231, 1, 0, 0.5842, 0.2032, 3.141592653589793, 0], "E77.0.8.0": [0, 5.03460768356323, 1, 0, 0.5842, 0.2032, 3.141592653589793, 0], "E77.0.9.0": [0, 5.08540768356323, 1, 0, 0.5842, 0.2032, 3.141592653589793, 0], "E80": [1.8112781047821045, 4.628207683563232, 1, 0, 0.635, 0.2286, 3.141592653589793, 0], "E81.0.1.0": [1.8112781047821045, 4.7044076835632325, 1, 0, 0.635, 0.2286, 3.141592653589793, 0], "E81.0.2.0": [1.8112781047821045, 4.7806076835632325, 1, 0, 0.635, 0.2286, 3.141592653589793, 0], "E81.0.3.0": [1.8112781047821045, 4.856807683563233, 1, 0, 0.635, 0.2286, 3.141592653589793, 0], "E81.0.4.0": [1.8112781047821045, 4.933007683563233, 1, 0, 0.635, 0.2286, 3.141592653589793, 0], "E81.0.5.0": [1.8112781047821045, 5.009207683563233, 1, 0, 0.635, 0.2286, 3.141592653589793, 0], "E81.0.6.0": [1.8112781047821045, 5.085407683563233, 1, 0, 0.635, 0.2286, 3.141592653589793, 0], "E81.0.7.0": [1.8112781047821045, 5.161607683563233, 1, 0, 0.635, 0.2286, 3.141592653589793, 0], "E93": [1.8112781047821045, 5.726189136505127, 1, 0, 0.635, 0.3302, 0, 3.141592653589793], "E95.0.1.0": [1.8112781047821045, 5.764289136505127, 1, 0, 0.635, 0.3302, 0, 3.141592653589793], "E95.0.2.0": [1.8112781047821045, 5.802389136505127, 1, 0, 0.635, 0.3302, 0, 3.141592653589793], "E95.0.3.0": [1.8112781047821045, 5.840489136505127, 1, 0, 0.635, 0.3302, 0, 3.141592653589793], "E95.0.4.0": [1.8112781047821045, 5.878589136505127, 1, 0, 0.635, 0.3302, 0, 3.141592653589793], "E95.0.5.0": [1.8112781047821045, 5.916689136505127, 1, 0, 0.635, 0.3302, 0, 3.141592653589793], "E95.0.6.0": [1.8112781047821045, 5.954789136505127, 1, 0, 0.635, 0.3302, 0, 3.141592653589793], "E95.0.7.0": [1.8112781047821045, 5.992889136505127, 1, 0, 0.635, 0.3302, 0, 3.141592653589793], "E101": [1.8112781047821045, 8.286508560180664, 1, 0, 0.635, 0.4572, 0, 3.141592653589793], "E103.0.1.0": [1.8112781047821045, 8.324608560180664, 1, 0, 0.635, 0.4572, 0, 3.141592653589793], "E103.0.2.0": [1.8112781047821045, 8.362708560180664, 1, 0, 0.635, 0.4572, 0, 3.141592653589793], "E103.0.3.0": [1.8112781047821045, 8.400808560180664, 1, 0, 0.635, 0.4572, 0, 3.141592653589793], "E103.0.4.0": [1.8112781047821045, 8.438908560180664, 1, 0, 0.635, 0.4572, 0, 3.141592653589793], "E103.0.5.0": [1.8112781047821045, 8.477008560180664, 1, 0, 0.635, 0.4572, 0, 3.141592653589793], "E103.0.6.0": [1.8112781047821045, 8.515108560180664, 1, 0, 0.635, 0.4572, 0, 3.141592653589793], "E103.0.7.0": [1.8112781047821045, 8.553208560180664, 1, 0, 0.635, 0.4572, 0, 3.141592653589793]};
            skSetInitialGuess(sketch, initialGuessF31);
            skSolve(sketch);
        }
        {
            var Q0;
            {var subQ0=sQuery(id+"F31.wireOp",EDGE,"E84.0.1.0");Q0=makeQuery(id+"F31.imprint","IMPRINT",FACE,{"disambiguationData":[TD([[makeQuery(id+"F31.imprint","IMPRINT",EDGE,{"derivedFrom":subQ0}),-1.0]])]});}
            var Q1;
            {var subQ0=sQuery(id+"F31.wireOp",EDGE,"E90.MirrorCS");Q1=makeQuery(id+"F31.imprint","IMPRINT",FACE,{"disambiguationData":[TD([[makeQuery(id+"F31.imprint","IMPRINT",EDGE,{"derivedFrom":subQ0}),-1.0]])]});}
            var Q2;
            {var subQ0=sQuery(id+"F31.wireOp",EDGE,"E84.0.2.0");Q2=makeQuery(id+"F31.imprint","IMPRINT",FACE,{"disambiguationData":[TD([[makeQuery(id+"F31.imprint","IMPRINT",EDGE,{"derivedFrom":subQ0}),1.0]])]});}
            extrude(context, id + "F32", {"entities" : qUnion([Q0, Q1, Q2]), "depth" : 2133.6 * mm});
        }
        {
            var Q0;
            {var subQ0=sQuery(id+"F31.wireOp",EDGE,"E97");Q0=makeQuery(id+"F31.imprint","IMPRINT",FACE,{"disambiguationData":[TD([[makeQuery(id+"F31.imprint","IMPRINT",EDGE,{"derivedFrom":subQ0}),1.0]])]});}
            var Q1;
            {var subQ0=sQuery(id+"F31.wireOp",EDGE,"E99.MirrorCS");Q1=makeQuery(id+"F31.imprint","IMPRINT",FACE,{"disambiguationData":[TD([[makeQuery(id+"F31.imprint","IMPRINT",EDGE,{"derivedFrom":subQ0}),1.0]])]});}
            var Q2;
            {var subQ3=sQuery(id+"F31.wireOp",EDGE,"E98");Q2=makeQuery(id+"F31.imprint","IMPRINT",FACE,{"disambiguationData":[TD([[makeQuery(id+"F31.imprint","IMPRINT",EDGE,{"derivedFrom":subQ3}),-1.0]])]});}
            extrude(context, id + "F33", {"entities" : qUnion([Q0, Q1, Q2]), "depth" : 2133.6 * mm});
        }
        {
            var Q0;
            {var subQ0=sQuery(id+"F31.wireOp",EDGE,"E105");Q0=makeQuery(id+"F31.imprint","IMPRINT",FACE,{"disambiguationData":[TD([[makeQuery(id+"F31.imprint","IMPRINT",EDGE,{"derivedFrom":subQ0}),1.0]])]});}
            var Q1;
            {var subQ3=sQuery(id+"F31.wireOp",EDGE,"E106");Q1=makeQuery(id+"F31.imprint","IMPRINT",FACE,{"disambiguationData":[TD([[makeQuery(id+"F31.imprint","IMPRINT",EDGE,{"derivedFrom":subQ3}),-1.0]])]});}
            extrude(context, id + "F34", {"entities" : qUnion([Q0, Q1]), "depth" : 2133.6 * mm});
        }
        {
            var Q0;
            Q0=qCreatedBy(makeId("Front.planeOp"),FACE);
            var sketch = newSketch(context, id + "F35", { "sketchPlane" : qUnion([Q0])});
            skLineSegment(sketch, "E109", {"start": v(5767.48, 7656.79) * mm, "end": v(5767.48, 2990.75) * mm, "construction": true});
            skLineSegment(sketch, "E110", {"start": v(4611.76, 4172.35) * mm, "end": v(7250.96, 4172.35) * mm, "construction": true});
            skLineSegment(sketch, "E111", {"start": v(4422.01, 6250.94) * mm, "end": v(7621.82, 6250.94) * mm, "construction": true});
            skEllipticalArc(sketch, "E112", {});
            skEllipticalArc(sketch, "E113.0.1.0", {});
            skEllipticalArc(sketch, "E113.0.2.0", {});
            skEllipticalArc(sketch, "E113.0.3.0", {});
            skEllipticalArc(sketch, "E113.0.4.0", {});
            skLineSegment(sketch, "E113.direction1", {"start": v(5183.28, 4172.35) * mm, "end": v(5208.68, 4172.35) * mm, "construction": true});
            skLineSegment(sketch, "E113.direction2", {"start": v(5183.28, 4172.35) * mm, "end": v(5183.28, 4248.55) * mm, "construction": true});
            skLineSegment(sketch, "E114.bottom", {"start": v(6300.88, 4770.7) * mm, "end": v(5234.08, 4770.7) * mm});
            skLineSegment(sketch, "E114.top", {"start": v(6300.88, 4103.45) * mm, "end": v(5234.08, 4103.45) * mm});
            skLineSegment(sketch, "E114.left", {"start": v(6300.88, 4770.7) * mm, "end": v(6300.88, 4103.45) * mm});
            skLineSegment(sketch, "E114.right", {"start": v(5234.08, 4770.7) * mm, "end": v(5234.08, 4103.45) * mm});
            skPoint(sketch, "E114.middle", {"position": v(5767.48, 4437.07) * mm});
            skLineSegment(sketch, "E115", {"start": v(5234.08, 4699.14) * mm, "end": v(5259.48, 4699.14) * mm});
            skLineSegment(sketch, "E116", {"start": v(5259.48, 4699.14) * mm, "end": v(5259.48, 4172.35) * mm});
            skLineSegment(sketch, "E117", {"start": v(5259.48, 4361.44) * mm, "end": v(5234.08, 4361.44) * mm});
            skLineSegment(sketch, "E118", {"start": v(5259.48, 4437.64) * mm, "end": v(5234.08, 4437.64) * mm});
            skEllipticalArc(sketch, "E119", {});
            skLineSegment(sketch, "E120.bottom", {"start": v(6300.88, 7393.94) * mm, "end": v(5234.08, 7393.94) * mm});
            skLineSegment(sketch, "E120.top", {"start": v(6300.88, 5107.94) * mm, "end": v(5234.08, 5107.94) * mm});
            skLineSegment(sketch, "E120.left", {"start": v(6300.88, 7393.94) * mm, "end": v(6300.88, 5107.94) * mm});
            skLineSegment(sketch, "E120.right", {"start": v(5234.08, 7393.94) * mm, "end": v(5234.08, 5107.94) * mm});
            skEllipticalArc(sketch, "E121.trimOffspring", {});
            skEllipticalArc(sketch, "E122.0.1.0", {});
            skEllipticalArc(sketch, "E122.0.2.0", {});
            skEllipticalArc(sketch, "E122.0.3.0", {});
            skEllipticalArc(sketch, "E122.0.4.0", {});
            skLineSegment(sketch, "E122.direction1", {"start": v(5234.08, 6406.33) * mm, "end": v(5259.48, 6406.33) * mm, "construction": true});
            skLineSegment(sketch, "E122.direction2", {"start": v(5234.08, 6406.33) * mm, "end": v(5234.08, 6431.73) * mm, "construction": true});
            skLineSegment(sketch, "E123", {"start": v(5234.08, 6756.61) * mm, "end": v(5259.48, 6756.61) * mm});
            skLineSegment(sketch, "E124", {"start": v(5259.48, 6756.61) * mm, "end": v(5259.48, 6276.86) * mm});
            skLineSegment(sketch, "E125", {"start": v(5259.48, 6489.88) * mm, "end": v(5234.08, 6489.88) * mm});
            skLineSegment(sketch, "E126", {"start": v(5259.48, 6464.48) * mm, "end": v(5234.08, 6464.48) * mm});
            skLineSegment(sketch, "E127", {"start": v(5259.48, 6515.28) * mm, "end": v(5234.08, 6515.28) * mm});
            skLineSegment(sketch, "E128.MirrorCS", {"start": v(6275.48, 4361.44) * mm, "end": v(6300.88, 4361.44) * mm});
            skLineSegment(sketch, "E129.MirrorCS", {"start": v(6275.48, 4437.64) * mm, "end": v(6300.88, 4437.64) * mm});
            skLineSegment(sketch, "E130.MirrorCS", {"start": v(6275.48, 6515.28) * mm, "end": v(6300.88, 6515.28) * mm});
            skLineSegment(sketch, "E131.MirrorCS", {"start": v(6275.48, 6464.48) * mm, "end": v(6300.88, 6464.48) * mm});
            skLineSegment(sketch, "E132.MirrorCS", {"start": v(6275.48, 6489.88) * mm, "end": v(6300.88, 6489.88) * mm});
            const initialGuessF35  = {"E112": [5.767484664916992, 4.172353267669678, 1, 0, 0.5842, 0.2286, 0, 3.141592653589793], "E113.0.1.0": [5.767484664916992, 4.248553267669678, 1, 0, 0.5842, 0.2286, 0, 3.141592653589793], "E113.0.2.0": [5.767484664916992, 4.324753267669678, 1, 0, 0.5842, 0.2286, 0, 3.141592653589793], "E113.0.3.0": [5.767484664916992, 4.400953267669678, 1, 0, 0.5842, 0.2286, 0, 3.141592653589793], "E113.0.4.0": [5.767484664916992, 4.477153267669678, 1, 0, 0.5842, 0.2286, 0, 3.141592653589793], "E119": [5.767484664916992, 6.250938415527344, 1, 0, 0.5842, 0.381, 3.141592653589793, 0], "E121.trimOffspring": [5.767484664916992, 6.250938415527344, 1, 0, 0.5842, 0.381, 0.4201114781424766, 2.7214811754473165], "E122.0.1.0": [5.767484664916992, 6.276338415527344, 1, 0, 0.5842, 0.381, 0.4201114781424766, 2.7214811754473165], "E122.0.2.0": [5.767484664916992, 6.301738415527344, 1, 0, 0.5842, 0.381, 0.4201114781424766, 2.7214811754473165], "E122.0.3.0": [5.767484664916992, 6.327138415527345, 1, 0, 0.5842, 0.381, 0.4201114781424766, 2.7214811754473165], "E122.0.4.0": [5.767484664916992, 6.352538415527345, 1, 0, 0.5842, 0.381, 0.4201114781424766, 2.7214811754473165]};
            skSetInitialGuess(sketch, initialGuessF35);
            skSolve(sketch);
        }
        {
            var Q0;
            {var subQ0=sQuery(id+"F35.wireOp",EDGE,"E122.0.3.0");var subQ1=sQuery(id+"F35.wireOp",EDGE,"E120.left");var subQ2=makeQuery(id+"F35.imprint","INTERSECT",VERTEX,{"derivedFrom":[subQ1,subQ0]});Q0=makeQuery(id+"F35.imprint","IMPRINT",FACE,{"disambiguationData":[TD([[makeQuery(id+"F35.imprint","IMPRINT",EDGE,{"disambiguationData":[TD([[subQ2,1.0]])],"derivedFrom":subQ1}),-1.0]])]});}
            var Q1;
            {var subQ0=sQuery(id+"F35.wireOp",EDGE,"E122.0.3.0");var subQ1=sQuery(id+"F35.wireOp",EDGE,"E120.left");var subQ2=makeQuery(id+"F35.imprint","INTERSECT",VERTEX,{"derivedFrom":[subQ1,subQ0]});Q1=makeQuery(id+"F35.imprint","IMPRINT",FACE,{"disambiguationData":[TD([[makeQuery(id+"F35.imprint","IMPRINT",EDGE,{"disambiguationData":[TD([[subQ2,-1.0]])],"derivedFrom":subQ1}),-1.0]])]});}
            var Q2;
            {var subQ0=sQuery(id+"F35.wireOp",EDGE,"E122.0.3.0");var subQ1=makeQuery(id+"F35.imprint","INTERSECT",VERTEX,{"derivedFrom":[subQ0,sQuery(id+"F35.wireOp",EDGE,"E130.MirrorCS")]});Q2=makeQuery(id+"F35.imprint","IMPRINT",FACE,{"disambiguationData":[TD([[makeQuery(id+"F35.imprint","IMPRINT",EDGE,{"disambiguationData":[TD([[subQ1,1.0]])],"derivedFrom":subQ0}),1.0]])]});}
            var Q3;
            {var subQ1=sQuery(id+"F35.wireOp",EDGE,"E122.0.3.0");var subQ3=sQuery(id+"F35.wireOp",EDGE,"E125");var subQ4=makeQuery(id+"F35.imprint","INTERSECT",VERTEX,{"derivedFrom":[subQ1,subQ3]});Q3=makeQuery(id+"F35.imprint","IMPRINT",FACE,{"disambiguationData":[TD([[makeQuery(id+"F35.imprint","IMPRINT",EDGE,{"disambiguationData":[TD([[subQ4,1.0]])],"derivedFrom":subQ1}),1.0]])]});}
            var Q4;
            {var subQ1=sQuery(id+"F35.wireOp",EDGE,"E120.right");var subQ5=sQuery(id+"F35.wireOp",EDGE,"E122.0.4.0");var subQ6=makeQuery(id+"F35.imprint","INTERSECT",VERTEX,{"derivedFrom":[subQ1,subQ5]});Q4=makeQuery(id+"F35.imprint","IMPRINT",FACE,{"disambiguationData":[TD([[makeQuery(id+"F35.imprint","IMPRINT",EDGE,{"disambiguationData":[TD([[subQ6,-1.0]])],"derivedFrom":subQ1}),1.0]])]});}
            var Q5;
            {var subQ0=sQuery(id+"F35.wireOp",EDGE,"E122.0.4.0");var subQ1=sQuery(id+"F35.wireOp",EDGE,"E120.right");var subQ2=makeQuery(id+"F35.imprint","INTERSECT",VERTEX,{"derivedFrom":[subQ1,subQ0]});Q5=makeQuery(id+"F35.imprint","IMPRINT",FACE,{"disambiguationData":[TD([[makeQuery(id+"F35.imprint","IMPRINT",EDGE,{"disambiguationData":[TD([[subQ2,1.0]])],"derivedFrom":subQ1}),1.0]])]});}
            var Q6;
            {var subQ5=sQuery(id+"F35.wireOp",EDGE,"E117");Q6=makeQuery(id+"F35.imprint","IMPRINT",FACE,{"disambiguationData":[TD([[makeQuery(id+"F35.imprint","IMPRINT",EDGE,{"derivedFrom":subQ5}),-1.0]])]});}
            var Q7;
            {var subQ0=sQuery(id+"F35.wireOp",EDGE,"E118");Q7=makeQuery(id+"F35.imprint","IMPRINT",FACE,{"disambiguationData":[TD([[makeQuery(id+"F35.imprint","IMPRINT",EDGE,{"derivedFrom":subQ0}),1.0]])]});}
            var Q8;
            {var subQ4=sQuery(id+"F35.wireOp",EDGE,"E128.MirrorCS");Q8=makeQuery(id+"F35.imprint","IMPRINT",FACE,{"disambiguationData":[TD([[makeQuery(id+"F35.imprint","IMPRINT",EDGE,{"derivedFrom":subQ4}),1.0]])]});}
            var Q9;
            {var subQ0=sQuery(id+"F35.wireOp",EDGE,"E129.MirrorCS");Q9=makeQuery(id+"F35.imprint","IMPRINT",FACE,{"disambiguationData":[TD([[makeQuery(id+"F35.imprint","IMPRINT",EDGE,{"derivedFrom":subQ0}),-1.0]])]});}
            extrude(context, id + "F36", {"entities" : qUnion([Q0, Q1, Q2, Q3, Q4, Q5, Q6, Q7, Q8, Q9]), "depth" : 1219.2 * mm});
        }
    });
